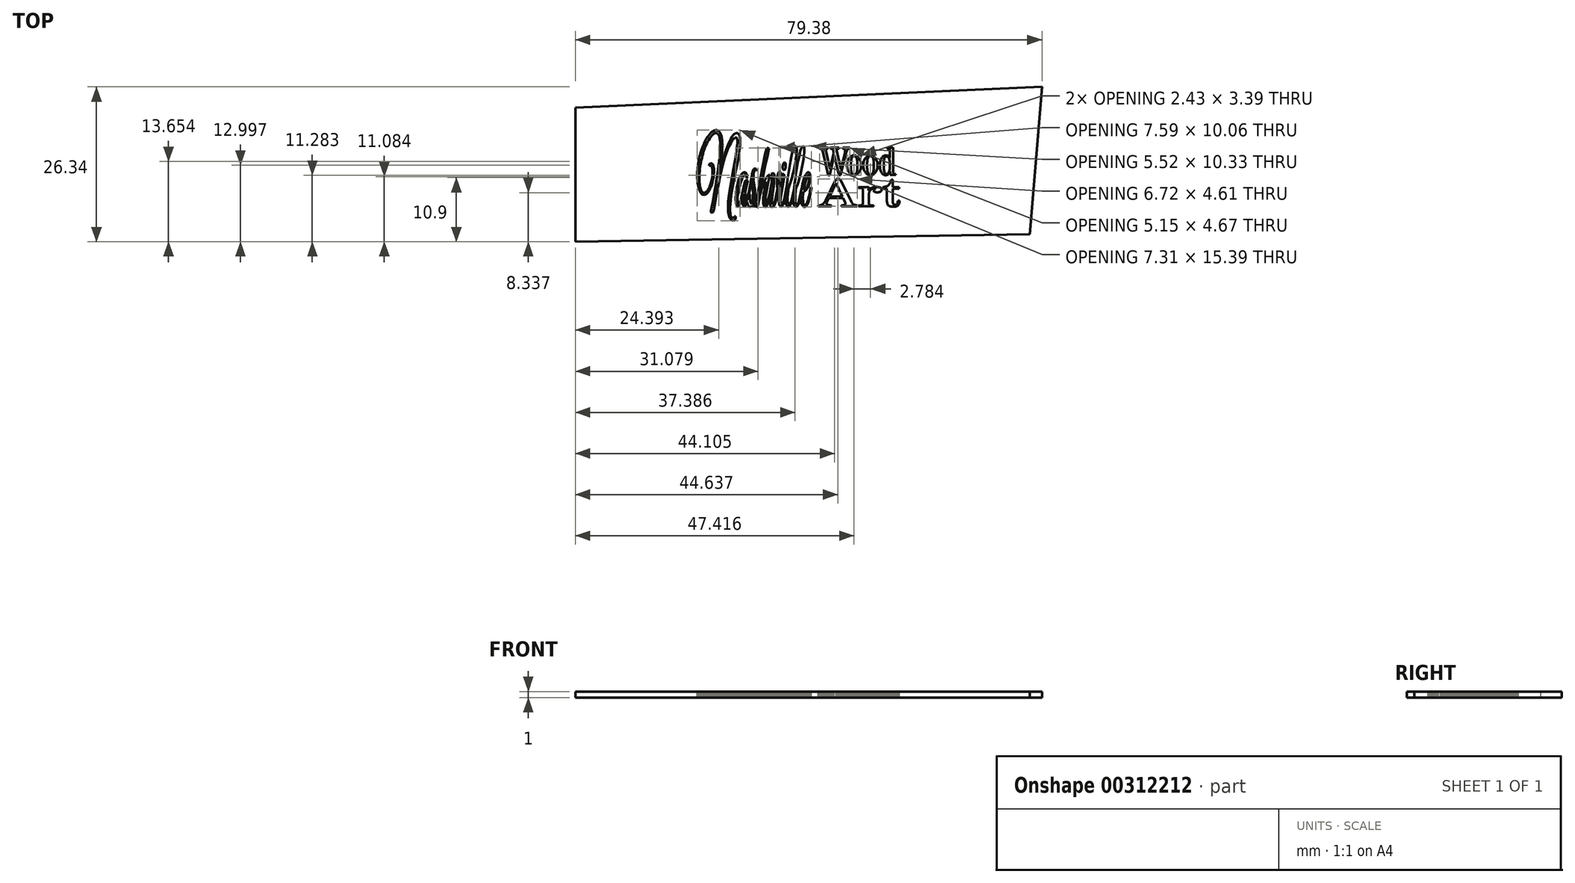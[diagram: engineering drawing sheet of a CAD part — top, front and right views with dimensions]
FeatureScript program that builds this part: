
annotation { "Feature Type Name" : "Feature", "Feature Type Description" : "" }
export const myFeature = defineFeature(function(context is Context, id is Id, definition is map)
    precondition{}
    {
        {
            var Q0;
            Q0=qCreatedBy(makeId("Top.planeOp"),FACE);
            var sketch = newSketch(context, id + "F0", { "sketchPlane" : qUnion([Q0])});
            skLineSegment(sketch, "E0", {"start": v(-39.28, -11.2) * mm, "end": v(-39.32, -11.42) * mm});
            skLineSegment(sketch, "E1", {"start": v(-39.32, -11.42) * mm, "end": v(-39.34, -11.62) * mm});
            skLineSegment(sketch, "E2", {"start": v(-39.34, -11.62) * mm, "end": v(-39.35, -11.79) * mm});
            skLineSegment(sketch, "E3", {"start": v(-39.35, -11.79) * mm, "end": v(-39.35, -11.92) * mm});
            skLineSegment(sketch, "E4", {"start": v(-39.35, -11.92) * mm, "end": v(-39.33, -12.03) * mm});
            skLineSegment(sketch, "E5", {"start": v(-39.33, -12.03) * mm, "end": v(-39.3, -12.1) * mm});
            skLineSegment(sketch, "E6", {"start": v(-39.3, -12.1) * mm, "end": v(-39.28, -12.11) * mm});
            skLineSegment(sketch, "E7", {"start": v(-39.28, -12.11) * mm, "end": v(-39.26, -12.12) * mm});
            skLineSegment(sketch, "E8", {"start": v(-39.26, -12.12) * mm, "end": v(-39.23, -12.12) * mm});
            skLineSegment(sketch, "E9", {"start": v(-39.23, -12.12) * mm, "end": v(-39.2, -12.1) * mm});
            skLineSegment(sketch, "E10", {"start": v(-39.2, -12.1) * mm, "end": v(-38.9, -11.92) * mm});
            skLineSegment(sketch, "E11", {"start": v(-38.9, -11.92) * mm, "end": v(4.95, -11.48) * mm});
            skLineSegment(sketch, "E12", {"start": v(4.95, -11.48) * mm, "end": v(7.55, -11.36) * mm});
            skLineSegment(sketch, "E13", {"start": v(7.55, -11.36) * mm, "end": v(8.8, -11.31) * mm});
            skLineSegment(sketch, "E14", {"start": v(8.8, -11.31) * mm, "end": v(10.27, -11.27) * mm});
            skLineSegment(sketch, "E15", {"start": v(10.27, -11.27) * mm, "end": v(11.78, -11.24) * mm});
            skLineSegment(sketch, "E16", {"start": v(11.78, -11.24) * mm, "end": v(13.15, -11.22) * mm});
            skLineSegment(sketch, "E17", {"start": v(13.15, -11.22) * mm, "end": v(14.14, -11.22) * mm});
            skLineSegment(sketch, "E18", {"start": v(14.14, -11.22) * mm, "end": v(14.54, -11.2) * mm});
            skLineSegment(sketch, "E19", {"start": v(14.54, -11.2) * mm, "end": v(14.89, -11.2) * mm});
            skLineSegment(sketch, "E20", {"start": v(14.89, -11.2) * mm, "end": v(15.18, -11.17) * mm});
            skLineSegment(sketch, "E21", {"start": v(15.18, -11.17) * mm, "end": v(15.42, -11.14) * mm});
            skLineSegment(sketch, "E22", {"start": v(15.42, -11.14) * mm, "end": v(15.62, -11.1) * mm});
            skLineSegment(sketch, "E23", {"start": v(15.62, -11.1) * mm, "end": v(15.78, -11.04) * mm});
            skLineSegment(sketch, "E24", {"start": v(15.78, -11.04) * mm, "end": v(15.85, -11) * mm});
            skLineSegment(sketch, "E25", {"start": v(15.85, -11) * mm, "end": v(15.9, -10.96) * mm});
            skLineSegment(sketch, "E26", {"start": v(15.9, -10.96) * mm, "end": v(15.95, -10.92) * mm});
            skLineSegment(sketch, "E27", {"start": v(15.95, -10.92) * mm, "end": v(16, -10.87) * mm});
            skLineSegment(sketch, "E28", {"start": v(16, -10.87) * mm, "end": v(16.03, -10.82) * mm});
            skLineSegment(sketch, "E29", {"start": v(16.03, -10.82) * mm, "end": v(16.06, -10.76) * mm});
            skLineSegment(sketch, "E30", {"start": v(16.06, -10.76) * mm, "end": v(16.1, -10.62) * mm});
            skLineSegment(sketch, "E31", {"start": v(16.1, -10.62) * mm, "end": v(16.14, -10.46) * mm});
            skLineSegment(sketch, "E32", {"start": v(16.14, -10.46) * mm, "end": v(16.15, -10.28) * mm});
            skLineSegment(sketch, "E33", {"start": v(16.15, -10.28) * mm, "end": v(16.16, -9.82) * mm});
            skLineSegment(sketch, "E34", {"start": v(16.16, -9.82) * mm, "end": v(16.16, -9.4) * mm});
            skLineSegment(sketch, "E35", {"start": v(16.16, -9.4) * mm, "end": v(16.2, -9.08) * mm});
            skLineSegment(sketch, "E36", {"start": v(16.2, -9.08) * mm, "end": v(16.21, -8.93) * mm});
            skLineSegment(sketch, "E37", {"start": v(16.21, -8.93) * mm, "end": v(16.24, -8.8) * mm});
            skLineSegment(sketch, "E38", {"start": v(16.24, -8.8) * mm, "end": v(16.28, -8.68) * mm});
            skLineSegment(sketch, "E39", {"start": v(16.28, -8.68) * mm, "end": v(16.33, -8.57) * mm});
            skLineSegment(sketch, "E40", {"start": v(16.33, -8.57) * mm, "end": v(16.38, -8.47) * mm});
            skLineSegment(sketch, "E41", {"start": v(16.38, -8.47) * mm, "end": v(16.45, -8.38) * mm});
            skLineSegment(sketch, "E42", {"start": v(16.45, -8.38) * mm, "end": v(16.52, -8.29) * mm});
            skLineSegment(sketch, "E43", {"start": v(16.52, -8.29) * mm, "end": v(16.61, -8.2) * mm});
            skLineSegment(sketch, "E44", {"start": v(16.61, -8.2) * mm, "end": v(16.72, -8.12) * mm});
            skLineSegment(sketch, "E45", {"start": v(16.72, -8.12) * mm, "end": v(16.83, -8.04) * mm});
            skLineSegment(sketch, "E46", {"start": v(16.83, -8.04) * mm, "end": v(17.1, -7.86) * mm});
            skLineSegment(sketch, "E47", {"start": v(17.1, -7.86) * mm, "end": v(17.31, -7.73) * mm});
            skLineSegment(sketch, "E48", {"start": v(17.31, -7.73) * mm, "end": v(17.5, -7.57) * mm});
            skLineSegment(sketch, "E49", {"start": v(17.5, -7.57) * mm, "end": v(17.69, -7.39) * mm});
            skLineSegment(sketch, "E50", {"start": v(17.69, -7.39) * mm, "end": v(17.85, -7.2) * mm});
            skLineSegment(sketch, "E51", {"start": v(17.85, -7.2) * mm, "end": v(18, -7) * mm});
            skLineSegment(sketch, "E52", {"start": v(18, -7) * mm, "end": v(18.1, -6.78) * mm});
            skLineSegment(sketch, "E53", {"start": v(18.1, -6.78) * mm, "end": v(18.2, -6.57) * mm});
            skLineSegment(sketch, "E54", {"start": v(18.2, -6.57) * mm, "end": v(18.26, -6.35) * mm});
            skLineSegment(sketch, "E55", {"start": v(18.26, -6.35) * mm, "end": v(18.32, -6.13) * mm});
            skLineSegment(sketch, "E56", {"start": v(18.32, -6.13) * mm, "end": v(18.37, -5.93) * mm});
            skLineSegment(sketch, "E57", {"start": v(18.37, -5.93) * mm, "end": v(18.44, -5.74) * mm});
            skLineSegment(sketch, "E58", {"start": v(18.44, -5.74) * mm, "end": v(18.52, -5.58) * mm});
            skLineSegment(sketch, "E59", {"start": v(18.52, -5.58) * mm, "end": v(18.6, -5.43) * mm});
            skLineSegment(sketch, "E60", {"start": v(18.6, -5.43) * mm, "end": v(18.7, -5.3) * mm});
            skLineSegment(sketch, "E61", {"start": v(18.7, -5.3) * mm, "end": v(18.83, -5.18) * mm});
            skLineSegment(sketch, "E62", {"start": v(18.83, -5.18) * mm, "end": v(18.97, -5.07) * mm});
            skLineSegment(sketch, "E63", {"start": v(18.97, -5.07) * mm, "end": v(19.14, -4.97) * mm});
            skLineSegment(sketch, "E64", {"start": v(19.14, -4.97) * mm, "end": v(19.33, -4.88) * mm});
            skLineSegment(sketch, "E65", {"start": v(19.33, -4.88) * mm, "end": v(19.55, -4.8) * mm});
            skLineSegment(sketch, "E66", {"start": v(19.55, -4.8) * mm, "end": v(19.8, -4.71) * mm});
            skLineSegment(sketch, "E67", {"start": v(19.8, -4.71) * mm, "end": v(20.09, -4.63) * mm});
            skLineSegment(sketch, "E68", {"start": v(20.09, -4.63) * mm, "end": v(20.41, -4.55) * mm});
            skLineSegment(sketch, "E69", {"start": v(20.41, -4.55) * mm, "end": v(21.18, -4.38) * mm});
            skLineSegment(sketch, "E70", {"start": v(21.18, -4.38) * mm, "end": v(21.6, -4.29) * mm});
            skLineSegment(sketch, "E71", {"start": v(21.6, -4.29) * mm, "end": v(22.03, -4.17) * mm});
            skLineSegment(sketch, "E72", {"start": v(22.03, -4.17) * mm, "end": v(22.46, -4.03) * mm});
            skLineSegment(sketch, "E73", {"start": v(22.46, -4.03) * mm, "end": v(22.89, -3.88) * mm});
            skLineSegment(sketch, "E74", {"start": v(22.89, -3.88) * mm, "end": v(23.3, -3.71) * mm});
            skLineSegment(sketch, "E75", {"start": v(23.3, -3.71) * mm, "end": v(23.67, -3.54) * mm});
            skLineSegment(sketch, "E76", {"start": v(23.67, -3.54) * mm, "end": v(24, -3.38) * mm});
            skLineSegment(sketch, "E77", {"start": v(24, -3.38) * mm, "end": v(24.26, -3.21) * mm});
            skLineSegment(sketch, "E78", {"start": v(24.26, -3.21) * mm, "end": v(24.5, -3.06) * mm});
            skLineSegment(sketch, "E79", {"start": v(24.5, -3.06) * mm, "end": v(24.74, -2.91) * mm});
            skLineSegment(sketch, "E80", {"start": v(24.74, -2.91) * mm, "end": v(24.98, -2.78) * mm});
            skLineSegment(sketch, "E81", {"start": v(24.98, -2.78) * mm, "end": v(25.2, -2.67) * mm});
            skLineSegment(sketch, "E82", {"start": v(25.2, -2.67) * mm, "end": v(25.4, -2.57) * mm});
            skLineSegment(sketch, "E83", {"start": v(25.4, -2.57) * mm, "end": v(25.58, -2.5) * mm});
            skLineSegment(sketch, "E84", {"start": v(25.58, -2.5) * mm, "end": v(25.73, -2.45) * mm});
            skLineSegment(sketch, "E85", {"start": v(25.73, -2.45) * mm, "end": v(25.84, -2.44) * mm});
            skLineSegment(sketch, "E86", {"start": v(25.84, -2.44) * mm, "end": v(25.9, -2.43) * mm});
            skLineSegment(sketch, "E87", {"start": v(25.9, -2.43) * mm, "end": v(25.96, -2.4) * mm});
            skLineSegment(sketch, "E88", {"start": v(25.96, -2.4) * mm, "end": v(26.13, -2.32) * mm});
            skLineSegment(sketch, "E89", {"start": v(26.13, -2.32) * mm, "end": v(26.33, -2.19) * mm});
            skLineSegment(sketch, "E90", {"start": v(26.33, -2.19) * mm, "end": v(26.57, -2) * mm});
            skLineSegment(sketch, "E91", {"start": v(26.57, -2) * mm, "end": v(26.84, -1.8) * mm});
            skLineSegment(sketch, "E92", {"start": v(26.84, -1.8) * mm, "end": v(27.12, -1.54) * mm});
            skLineSegment(sketch, "E93", {"start": v(27.12, -1.54) * mm, "end": v(27.41, -1.27) * mm});
            skLineSegment(sketch, "E94", {"start": v(27.41, -1.27) * mm, "end": v(27.7, -0.98) * mm});
            skLineSegment(sketch, "E95", {"start": v(27.7, -0.98) * mm, "end": v(28.08, -0.6) * mm});
            skLineSegment(sketch, "E96", {"start": v(28.08, -0.6) * mm, "end": v(28.41, -0.3) * mm});
            skLineSegment(sketch, "E97", {"start": v(28.41, -0.3) * mm, "end": v(28.73, -0.05) * mm});
            skLineSegment(sketch, "E98", {"start": v(28.73, -0.05) * mm, "end": v(28.87, 0.06) * mm});
            skLineSegment(sketch, "E99", {"start": v(28.87, 0.06) * mm, "end": v(29.02, 0.15) * mm});
            skLineSegment(sketch, "E100", {"start": v(29.02, 0.15) * mm, "end": v(29.15, 0.23) * mm});
            skLineSegment(sketch, "E101", {"start": v(29.15, 0.23) * mm, "end": v(29.29, 0.3) * mm});
            skLineSegment(sketch, "E102", {"start": v(29.29, 0.3) * mm, "end": v(29.42, 0.36) * mm});
            skLineSegment(sketch, "E103", {"start": v(29.42, 0.36) * mm, "end": v(29.55, 0.4) * mm});
            skLineSegment(sketch, "E104", {"start": v(29.55, 0.4) * mm, "end": v(29.68, 0.44) * mm});
            skLineSegment(sketch, "E105", {"start": v(29.68, 0.44) * mm, "end": v(29.8, 0.47) * mm});
            skLineSegment(sketch, "E106", {"start": v(29.8, 0.47) * mm, "end": v(29.93, 0.48) * mm});
            skLineSegment(sketch, "E107", {"start": v(29.93, 0.48) * mm, "end": v(30.06, 0.49) * mm});
            skLineSegment(sketch, "E108", {"start": v(30.06, 0.49) * mm, "end": v(30.3, 0.5) * mm});
            skLineSegment(sketch, "E109", {"start": v(30.3, 0.5) * mm, "end": v(30.52, 0.55) * mm});
            skLineSegment(sketch, "E110", {"start": v(30.52, 0.55) * mm, "end": v(30.75, 0.62) * mm});
            skLineSegment(sketch, "E111", {"start": v(30.75, 0.62) * mm, "end": v(30.98, 0.73) * mm});
            skLineSegment(sketch, "E112", {"start": v(30.98, 0.73) * mm, "end": v(31.2, 0.86) * mm});
            skLineSegment(sketch, "E113", {"start": v(31.2, 0.86) * mm, "end": v(31.42, 1.03) * mm});
            skLineSegment(sketch, "E114", {"start": v(31.42, 1.03) * mm, "end": v(31.64, 1.23) * mm});
            skLineSegment(sketch, "E115", {"start": v(31.64, 1.23) * mm, "end": v(31.86, 1.46) * mm});
            skLineSegment(sketch, "E116", {"start": v(31.86, 1.46) * mm, "end": v(32.07, 1.68) * mm});
            skLineSegment(sketch, "E117", {"start": v(32.07, 1.68) * mm, "end": v(32.29, 1.87) * mm});
            skLineSegment(sketch, "E118", {"start": v(32.29, 1.87) * mm, "end": v(32.5, 2.04) * mm});
            skLineSegment(sketch, "E119", {"start": v(32.5, 2.04) * mm, "end": v(32.73, 2.18) * mm});
            skLineSegment(sketch, "E120", {"start": v(32.73, 2.18) * mm, "end": v(32.95, 2.29) * mm});
            skLineSegment(sketch, "E121", {"start": v(32.95, 2.29) * mm, "end": v(33.17, 2.37) * mm});
            skLineSegment(sketch, "E122", {"start": v(33.17, 2.37) * mm, "end": v(33.38, 2.42) * mm});
            skLineSegment(sketch, "E123", {"start": v(33.38, 2.42) * mm, "end": v(33.49, 2.43) * mm});
            skLineSegment(sketch, "E124", {"start": v(33.49, 2.43) * mm, "end": v(33.59, 2.43) * mm});
            skLineSegment(sketch, "E125", {"start": v(33.59, 2.43) * mm, "end": v(33.7, 2.44) * mm});
            skLineSegment(sketch, "E126", {"start": v(33.7, 2.44) * mm, "end": v(33.81, 2.47) * mm});
            skLineSegment(sketch, "E127", {"start": v(33.81, 2.47) * mm, "end": v(33.94, 2.5) * mm});
            skLineSegment(sketch, "E128", {"start": v(33.94, 2.5) * mm, "end": v(34.07, 2.56) * mm});
            skLineSegment(sketch, "E129", {"start": v(34.07, 2.56) * mm, "end": v(34.21, 2.63) * mm});
            skLineSegment(sketch, "E130", {"start": v(34.21, 2.63) * mm, "end": v(34.36, 2.71) * mm});
            skLineSegment(sketch, "E131", {"start": v(34.36, 2.71) * mm, "end": v(34.66, 2.92) * mm});
            skLineSegment(sketch, "E132", {"start": v(34.66, 2.92) * mm, "end": v(34.99, 3.16) * mm});
            skLineSegment(sketch, "E133", {"start": v(34.99, 3.16) * mm, "end": v(35.32, 3.44) * mm});
            skLineSegment(sketch, "E134", {"start": v(35.32, 3.44) * mm, "end": v(35.66, 3.76) * mm});
            skLineSegment(sketch, "E135", {"start": v(35.66, 3.76) * mm, "end": v(36, 4.1) * mm});
            skLineSegment(sketch, "E136", {"start": v(36, 4.1) * mm, "end": v(36.32, 4.45) * mm});
            skLineSegment(sketch, "E137", {"start": v(36.32, 4.45) * mm, "end": v(36.64, 4.83) * mm});
            skLineSegment(sketch, "E138", {"start": v(36.64, 4.83) * mm, "end": v(36.93, 5.2) * mm});
            skLineSegment(sketch, "E139", {"start": v(36.93, 5.2) * mm, "end": v(37.2, 5.58) * mm});
            skLineSegment(sketch, "E140", {"start": v(37.2, 5.58) * mm, "end": v(37.44, 5.96) * mm});
            skLineSegment(sketch, "E141", {"start": v(37.44, 5.96) * mm, "end": v(37.65, 6.32) * mm});
            skLineSegment(sketch, "E142", {"start": v(37.65, 6.32) * mm, "end": v(37.73, 6.5) * mm});
            skLineSegment(sketch, "E143", {"start": v(37.73, 6.5) * mm, "end": v(37.8, 6.66) * mm});
            skLineSegment(sketch, "E144", {"start": v(37.8, 6.66) * mm, "end": v(37.87, 6.83) * mm});
            skLineSegment(sketch, "E145", {"start": v(37.87, 6.83) * mm, "end": v(37.92, 6.98) * mm});
            skLineSegment(sketch, "E146", {"start": v(37.92, 6.98) * mm, "end": v(38.1, 7.66) * mm});
            skLineSegment(sketch, "E147", {"start": v(38.1, 7.66) * mm, "end": v(38.17, 7.94) * mm});
            skLineSegment(sketch, "E148", {"start": v(38.17, 7.94) * mm, "end": v(38.21, 8.19) * mm});
            skLineSegment(sketch, "E149", {"start": v(38.21, 8.19) * mm, "end": v(38.24, 8.4) * mm});
            skLineSegment(sketch, "E150", {"start": v(38.24, 8.4) * mm, "end": v(38.24, 8.58) * mm});
            skLineSegment(sketch, "E151", {"start": v(38.24, 8.58) * mm, "end": v(38.23, 8.74) * mm});
            skLineSegment(sketch, "E152", {"start": v(38.23, 8.74) * mm, "end": v(38.2, 8.87) * mm});
            skLineSegment(sketch, "E153", {"start": v(38.2, 8.87) * mm, "end": v(38.17, 8.93) * mm});
            skLineSegment(sketch, "E154", {"start": v(38.17, 8.93) * mm, "end": v(38.14, 8.98) * mm});
            skLineSegment(sketch, "E155", {"start": v(38.14, 8.98) * mm, "end": v(38.1, 9.03) * mm});
            skLineSegment(sketch, "E156", {"start": v(38.1, 9.03) * mm, "end": v(38.05, 9.07) * mm});
            skLineSegment(sketch, "E157", {"start": v(38.05, 9.07) * mm, "end": v(37.95, 9.13) * mm});
            skLineSegment(sketch, "E158", {"start": v(37.95, 9.13) * mm, "end": v(37.81, 9.18) * mm});
            skLineSegment(sketch, "E159", {"start": v(37.81, 9.18) * mm, "end": v(37.66, 9.22) * mm});
            skLineSegment(sketch, "E160", {"start": v(37.66, 9.22) * mm, "end": v(37.47, 9.24) * mm});
            skLineSegment(sketch, "E161", {"start": v(37.47, 9.24) * mm, "end": v(37.26, 9.25) * mm});
            skLineSegment(sketch, "E162", {"start": v(37.26, 9.25) * mm, "end": v(37.02, 9.26) * mm});
            skLineSegment(sketch, "E163", {"start": v(37.02, 9.26) * mm, "end": v(36.76, 9.25) * mm});
            skLineSegment(sketch, "E164", {"start": v(36.76, 9.25) * mm, "end": v(36.49, 9.22) * mm});
            skLineSegment(sketch, "E165", {"start": v(36.49, 9.22) * mm, "end": v(36.22, 9.18) * mm});
            skLineSegment(sketch, "E166", {"start": v(36.22, 9.18) * mm, "end": v(35.96, 9.12) * mm});
            skLineSegment(sketch, "E167", {"start": v(35.96, 9.12) * mm, "end": v(35.7, 9.05) * mm});
            skLineSegment(sketch, "E168", {"start": v(35.7, 9.05) * mm, "end": v(35.48, 8.97) * mm});
            skLineSegment(sketch, "E169", {"start": v(35.48, 8.97) * mm, "end": v(35.29, 8.89) * mm});
            skLineSegment(sketch, "E170", {"start": v(35.29, 8.89) * mm, "end": v(35.13, 8.8) * mm});
            skLineSegment(sketch, "E171", {"start": v(35.13, 8.8) * mm, "end": v(34.46, 8.33) * mm});
            skLineSegment(sketch, "E172", {"start": v(34.46, 8.33) * mm, "end": v(14.46, 7.62) * mm});
            skLineSegment(sketch, "E173", {"start": v(14.46, 7.62) * mm, "end": v(-16.17, 7.68) * mm});
            skLineSegment(sketch, "E174", {"start": v(-16.17, 7.68) * mm, "end": v(-17.7, 7.93) * mm});
            skLineSegment(sketch, "E175", {"start": v(-17.7, 7.93) * mm, "end": v(-18.22, 8.01) * mm});
            skLineSegment(sketch, "E176", {"start": v(-18.22, 8.01) * mm, "end": v(-18.6, 8.06) * mm});
            skLineSegment(sketch, "E177", {"start": v(-18.6, 8.06) * mm, "end": v(-18.75, 8.07) * mm});
            skLineSegment(sketch, "E178", {"start": v(-18.75, 8.07) * mm, "end": v(-18.88, 8.06) * mm});
            skLineSegment(sketch, "E179", {"start": v(-18.88, 8.06) * mm, "end": v(-18.98, 8.04) * mm});
            skLineSegment(sketch, "E180", {"start": v(-18.98, 8.04) * mm, "end": v(-19.06, 8.01) * mm});
            skLineSegment(sketch, "E181", {"start": v(-19.06, 8.01) * mm, "end": v(-19.12, 7.97) * mm});
            skLineSegment(sketch, "E182", {"start": v(-19.12, 7.97) * mm, "end": v(-19.17, 7.9) * mm});
            skLineSegment(sketch, "E183", {"start": v(-19.17, 7.9) * mm, "end": v(-19.2, 7.82) * mm});
            skLineSegment(sketch, "E184", {"start": v(-19.2, 7.82) * mm, "end": v(-19.23, 7.72) * mm});
            skLineSegment(sketch, "E185", {"start": v(-19.23, 7.72) * mm, "end": v(-19.24, 7.6) * mm});
            skLineSegment(sketch, "E186", {"start": v(-19.24, 7.6) * mm, "end": v(-19.25, 7.45) * mm});
            skLineSegment(sketch, "E187", {"start": v(-19.25, 7.45) * mm, "end": v(-19.25, 7.1) * mm});
            skLineSegment(sketch, "E188", {"start": v(-19.25, 7.1) * mm, "end": v(-19.26, 6.86) * mm});
            skLineSegment(sketch, "E189", {"start": v(-19.26, 6.86) * mm, "end": v(-19.28, 6.65) * mm});
            skLineSegment(sketch, "E190", {"start": v(-19.28, 6.65) * mm, "end": v(-19.32, 6.47) * mm});
            skLineSegment(sketch, "E191", {"start": v(-19.32, 6.47) * mm, "end": v(-19.36, 6.3) * mm});
            skLineSegment(sketch, "E192", {"start": v(-19.36, 6.3) * mm, "end": v(-19.42, 6.18) * mm});
            skLineSegment(sketch, "E193", {"start": v(-19.42, 6.18) * mm, "end": v(-19.5, 6.08) * mm});
            skLineSegment(sketch, "E194", {"start": v(-19.5, 6.08) * mm, "end": v(-19.53, 6.04) * mm});
            skLineSegment(sketch, "E195", {"start": v(-19.53, 6.04) * mm, "end": v(-19.57, 6.02) * mm});
            skLineSegment(sketch, "E196", {"start": v(-19.57, 6.02) * mm, "end": v(-19.61, 6) * mm});
            skLineSegment(sketch, "E197", {"start": v(-19.61, 6) * mm, "end": v(-19.66, 6) * mm});
            skLineSegment(sketch, "E198", {"start": v(-19.66, 6) * mm, "end": v(-20.06, 5.98) * mm});
            skLineSegment(sketch, "E199", {"start": v(-20.06, 5.98) * mm, "end": v(-23.64, 5.99) * mm});
            skLineSegment(sketch, "E200", {"start": v(-23.64, 5.99) * mm, "end": v(-25.21, 5.98) * mm});
            skLineSegment(sketch, "E201", {"start": v(-25.21, 5.98) * mm, "end": v(-26.86, 5.94) * mm});
            skLineSegment(sketch, "E202", {"start": v(-26.86, 5.94) * mm, "end": v(-28.38, 5.88) * mm});
            skLineSegment(sketch, "E203", {"start": v(-28.38, 5.88) * mm, "end": v(-29.03, 5.84) * mm});
            skLineSegment(sketch, "E204", {"start": v(-29.03, 5.84) * mm, "end": v(-29.58, 5.8) * mm});
            skLineSegment(sketch, "E205", {"start": v(-29.58, 5.8) * mm, "end": v(-30.36, 5.73) * mm});
            skLineSegment(sketch, "E206", {"start": v(-30.36, 5.73) * mm, "end": v(-30.95, 5.67) * mm});
            skLineSegment(sketch, "E207", {"start": v(-30.95, 5.67) * mm, "end": v(-31.2, 5.63) * mm});
            skLineSegment(sketch, "E208", {"start": v(-31.2, 5.63) * mm, "end": v(-31.4, 5.58) * mm});
            skLineSegment(sketch, "E209", {"start": v(-31.4, 5.58) * mm, "end": v(-31.57, 5.53) * mm});
            skLineSegment(sketch, "E210", {"start": v(-31.57, 5.53) * mm, "end": v(-31.72, 5.46) * mm});
            skLineSegment(sketch, "E211", {"start": v(-31.72, 5.46) * mm, "end": v(-31.85, 5.38) * mm});
            skLineSegment(sketch, "E212", {"start": v(-31.85, 5.38) * mm, "end": v(-31.97, 5.28) * mm});
            skLineSegment(sketch, "E213", {"start": v(-31.97, 5.28) * mm, "end": v(-32.07, 5.17) * mm});
            skLineSegment(sketch, "E214", {"start": v(-32.07, 5.17) * mm, "end": v(-32.17, 5.03) * mm});
            skLineSegment(sketch, "E215", {"start": v(-32.17, 5.03) * mm, "end": v(-32.26, 4.88) * mm});
            skLineSegment(sketch, "E216", {"start": v(-32.26, 4.88) * mm, "end": v(-32.35, 4.7) * mm});
            skLineSegment(sketch, "E217", {"start": v(-32.35, 4.7) * mm, "end": v(-32.56, 4.24) * mm});
            skLineSegment(sketch, "E218", {"start": v(-32.56, 4.24) * mm, "end": v(-32.7, 3.93) * mm});
            skLineSegment(sketch, "E219", {"start": v(-32.7, 3.93) * mm, "end": v(-32.82, 3.58) * mm});
            skLineSegment(sketch, "E220", {"start": v(-32.82, 3.58) * mm, "end": v(-32.95, 3.2) * mm});
            skLineSegment(sketch, "E221", {"start": v(-32.95, 3.2) * mm, "end": v(-33.07, 2.79) * mm});
            skLineSegment(sketch, "E222", {"start": v(-33.07, 2.79) * mm, "end": v(-33.17, 2.37) * mm});
            skLineSegment(sketch, "E223", {"start": v(-33.17, 2.37) * mm, "end": v(-33.27, 1.96) * mm});
            skLineSegment(sketch, "E224", {"start": v(-33.27, 1.96) * mm, "end": v(-33.35, 1.57) * mm});
            skLineSegment(sketch, "E225", {"start": v(-33.35, 1.57) * mm, "end": v(-33.4, 1.2) * mm});
            skLineSegment(sketch, "E226", {"start": v(-33.4, 1.2) * mm, "end": v(-33.47, 0.77) * mm});
            skLineSegment(sketch, "E227", {"start": v(-33.47, 0.77) * mm, "end": v(-33.56, 0.37) * mm});
            skLineSegment(sketch, "E228", {"start": v(-33.56, 0.37) * mm, "end": v(-33.66, 0.01) * mm});
            skLineSegment(sketch, "E229", {"start": v(-33.66, 0.01) * mm, "end": v(-33.72, -0.16) * mm});
            skLineSegment(sketch, "E230", {"start": v(-33.72, -0.16) * mm, "end": v(-33.8, -0.32) * mm});
            skLineSegment(sketch, "E231", {"start": v(-33.8, -0.32) * mm, "end": v(-33.86, -0.47) * mm});
            skLineSegment(sketch, "E232", {"start": v(-33.86, -0.47) * mm, "end": v(-33.94, -0.62) * mm});
            skLineSegment(sketch, "E233", {"start": v(-33.94, -0.62) * mm, "end": v(-34.03, -0.77) * mm});
            skLineSegment(sketch, "E234", {"start": v(-34.03, -0.77) * mm, "end": v(-34.12, -0.91) * mm});
            skLineSegment(sketch, "E235", {"start": v(-34.12, -0.91) * mm, "end": v(-34.32, -1.19) * mm});
            skLineSegment(sketch, "E236", {"start": v(-34.32, -1.19) * mm, "end": v(-34.56, -1.46) * mm});
            skLineSegment(sketch, "E237", {"start": v(-34.56, -1.46) * mm, "end": v(-34.75, -1.67) * mm});
            skLineSegment(sketch, "E238", {"start": v(-34.75, -1.67) * mm, "end": v(-34.92, -1.9) * mm});
            skLineSegment(sketch, "E239", {"start": v(-34.92, -1.9) * mm, "end": v(-35.08, -2.13) * mm});
            skLineSegment(sketch, "E240", {"start": v(-35.08, -2.13) * mm, "end": v(-35.22, -2.36) * mm});
            skLineSegment(sketch, "E241", {"start": v(-35.22, -2.36) * mm, "end": v(-35.33, -2.6) * mm});
            skLineSegment(sketch, "E242", {"start": v(-35.33, -2.6) * mm, "end": v(-35.42, -2.8) * mm});
            skLineSegment(sketch, "E243", {"start": v(-35.42, -2.8) * mm, "end": v(-35.48, -3) * mm});
            skLineSegment(sketch, "E244", {"start": v(-35.48, -3) * mm, "end": v(-35.49, -3.1) * mm});
            skLineSegment(sketch, "E245", {"start": v(-35.49, -3.1) * mm, "end": v(-35.5, -3.17) * mm});
            skLineSegment(sketch, "E246", {"start": v(-35.5, -3.17) * mm, "end": v(-35.51, -3.34) * mm});
            skLineSegment(sketch, "E247", {"start": v(-35.51, -3.34) * mm, "end": v(-35.56, -3.55) * mm});
            skLineSegment(sketch, "E248", {"start": v(-35.56, -3.55) * mm, "end": v(-35.63, -3.79) * mm});
            skLineSegment(sketch, "E249", {"start": v(-35.63, -3.79) * mm, "end": v(-35.73, -4.04) * mm});
            skLineSegment(sketch, "E250", {"start": v(-35.73, -4.04) * mm, "end": v(-35.85, -4.3) * mm});
            skLineSegment(sketch, "E251", {"start": v(-35.85, -4.3) * mm, "end": v(-35.98, -4.57) * mm});
            skLineSegment(sketch, "E252", {"start": v(-35.98, -4.57) * mm, "end": v(-36.14, -4.84) * mm});
            skLineSegment(sketch, "E253", {"start": v(-36.14, -4.84) * mm, "end": v(-36.3, -5.1) * mm});
            skLineSegment(sketch, "E254", {"start": v(-36.3, -5.1) * mm, "end": v(-36.47, -5.36) * mm});
            skLineSegment(sketch, "E255", {"start": v(-36.47, -5.36) * mm, "end": v(-36.65, -5.66) * mm});
            skLineSegment(sketch, "E256", {"start": v(-36.65, -5.66) * mm, "end": v(-36.84, -6) * mm});
            skLineSegment(sketch, "E257", {"start": v(-36.84, -6) * mm, "end": v(-37.02, -6.34) * mm});
            skLineSegment(sketch, "E258", {"start": v(-37.02, -6.34) * mm, "end": v(-37.2, -6.7) * mm});
            skLineSegment(sketch, "E259", {"start": v(-37.2, -6.7) * mm, "end": v(-37.37, -7.04) * mm});
            skLineSegment(sketch, "E260", {"start": v(-37.37, -7.04) * mm, "end": v(-37.52, -7.38) * mm});
            skLineSegment(sketch, "E261", {"start": v(-37.52, -7.38) * mm, "end": v(-37.65, -7.68) * mm});
            skLineSegment(sketch, "E262", {"start": v(-37.65, -7.68) * mm, "end": v(-37.76, -7.98) * mm});
            skLineSegment(sketch, "E263", {"start": v(-37.76, -7.98) * mm, "end": v(-37.9, -8.27) * mm});
            skLineSegment(sketch, "E264", {"start": v(-37.9, -8.27) * mm, "end": v(-38.16, -8.83) * mm});
            skLineSegment(sketch, "E265", {"start": v(-38.16, -8.83) * mm, "end": v(-38.3, -9.08) * mm});
            skLineSegment(sketch, "E266", {"start": v(-38.3, -9.08) * mm, "end": v(-38.42, -9.3) * mm});
            skLineSegment(sketch, "E267", {"start": v(-38.42, -9.3) * mm, "end": v(-38.53, -9.47) * mm});
            skLineSegment(sketch, "E268", {"start": v(-38.53, -9.47) * mm, "end": v(-38.63, -9.6) * mm});
            skLineSegment(sketch, "E269", {"start": v(-38.63, -9.6) * mm, "end": v(-38.72, -9.73) * mm});
            skLineSegment(sketch, "E270", {"start": v(-38.72, -9.73) * mm, "end": v(-38.81, -9.89) * mm});
            skLineSegment(sketch, "E271", {"start": v(-38.81, -9.89) * mm, "end": v(-38.9, -10.08) * mm});
            skLineSegment(sketch, "E272", {"start": v(-38.9, -10.08) * mm, "end": v(-39, -10.28) * mm});
            skLineSegment(sketch, "E273", {"start": v(-39, -10.28) * mm, "end": v(-39.08, -10.5) * mm});
            skLineSegment(sketch, "E274", {"start": v(-39.08, -10.5) * mm, "end": v(-39.16, -10.74) * mm});
            skLineSegment(sketch, "E275", {"start": v(-39.16, -10.74) * mm, "end": v(-39.22, -10.97) * mm});
            skLineSegment(sketch, "E276", {"start": v(-39.22, -10.97) * mm, "end": v(-39.28, -11.2) * mm});
            skLineSegment(sketch, "E277", {"start": v(-35.66, -10.48) * mm, "end": v(-8.7, -10.32) * mm});
            skLineSegment(sketch, "E278", {"start": v(-8.7, -10.32) * mm, "end": v(13.4, -9.88) * mm});
            skLineSegment(sketch, "E279", {"start": v(13.4, -9.88) * mm, "end": v(13.98, -9.7) * mm});
            skLineSegment(sketch, "E280", {"start": v(13.98, -9.7) * mm, "end": v(14.04, -9.68) * mm});
            skLineSegment(sketch, "E281", {"start": v(14.04, -9.68) * mm, "end": v(14.1, -9.65) * mm});
            skLineSegment(sketch, "E282", {"start": v(14.1, -9.65) * mm, "end": v(14.22, -9.56) * mm});
            skLineSegment(sketch, "E283", {"start": v(14.22, -9.56) * mm, "end": v(14.33, -9.45) * mm});
            skLineSegment(sketch, "E284", {"start": v(14.33, -9.45) * mm, "end": v(14.44, -9.3) * mm});
            skLineSegment(sketch, "E285", {"start": v(14.44, -9.3) * mm, "end": v(14.54, -9.15) * mm});
            skLineSegment(sketch, "E286", {"start": v(14.54, -9.15) * mm, "end": v(14.63, -8.97) * mm});
            skLineSegment(sketch, "E287", {"start": v(14.63, -8.97) * mm, "end": v(14.7, -8.78) * mm});
            skLineSegment(sketch, "E288", {"start": v(14.7, -8.78) * mm, "end": v(14.75, -8.6) * mm});
            skLineSegment(sketch, "E289", {"start": v(14.75, -8.6) * mm, "end": v(14.77, -8.49) * mm});
            skLineSegment(sketch, "E290", {"start": v(14.77, -8.49) * mm, "end": v(14.8, -8.38) * mm});
            skLineSegment(sketch, "E291", {"start": v(14.8, -8.38) * mm, "end": v(14.9, -8.16) * mm});
            skLineSegment(sketch, "E292", {"start": v(14.9, -8.16) * mm, "end": v(15.03, -7.92) * mm});
            skLineSegment(sketch, "E293", {"start": v(15.03, -7.92) * mm, "end": v(15.2, -7.68) * mm});
            skLineSegment(sketch, "E294", {"start": v(15.2, -7.68) * mm, "end": v(15.38, -7.45) * mm});
            skLineSegment(sketch, "E295", {"start": v(15.38, -7.45) * mm, "end": v(15.58, -7.22) * mm});
            skLineSegment(sketch, "E296", {"start": v(15.58, -7.22) * mm, "end": v(15.8, -7) * mm});
            skLineSegment(sketch, "E297", {"start": v(15.8, -7) * mm, "end": v(16.03, -6.82) * mm});
            skLineSegment(sketch, "E298", {"start": v(16.03, -6.82) * mm, "end": v(16.25, -6.64) * mm});
            skLineSegment(sketch, "E299", {"start": v(16.25, -6.64) * mm, "end": v(16.46, -6.44) * mm});
            skLineSegment(sketch, "E300", {"start": v(16.46, -6.44) * mm, "end": v(16.65, -6.25) * mm});
            skLineSegment(sketch, "E301", {"start": v(16.65, -6.25) * mm, "end": v(16.8, -6.05) * mm});
            skLineSegment(sketch, "E302", {"start": v(16.8, -6.05) * mm, "end": v(16.94, -5.87) * mm});
            skLineSegment(sketch, "E303", {"start": v(16.94, -5.87) * mm, "end": v(17.04, -5.7) * mm});
            skLineSegment(sketch, "E304", {"start": v(17.04, -5.7) * mm, "end": v(17.1, -5.53) * mm});
            skLineSegment(sketch, "E305", {"start": v(17.1, -5.53) * mm, "end": v(17.13, -5.46) * mm});
            skLineSegment(sketch, "E306", {"start": v(17.13, -5.46) * mm, "end": v(17.13, -5.4) * mm});
            skLineSegment(sketch, "E307", {"start": v(17.13, -5.4) * mm, "end": v(17.15, -5.23) * mm});
            skLineSegment(sketch, "E308", {"start": v(17.15, -5.23) * mm, "end": v(17.2, -5.05) * mm});
            skLineSegment(sketch, "E309", {"start": v(17.2, -5.05) * mm, "end": v(17.27, -4.88) * mm});
            skLineSegment(sketch, "E310", {"start": v(17.27, -4.88) * mm, "end": v(17.37, -4.7) * mm});
            skLineSegment(sketch, "E311", {"start": v(17.37, -4.7) * mm, "end": v(17.5, -4.53) * mm});
            skLineSegment(sketch, "E312", {"start": v(17.5, -4.53) * mm, "end": v(17.64, -4.37) * mm});
            skLineSegment(sketch, "E313", {"start": v(17.64, -4.37) * mm, "end": v(17.81, -4.2) * mm});
            skLineSegment(sketch, "E314", {"start": v(17.81, -4.2) * mm, "end": v(18, -4.05) * mm});
            skLineSegment(sketch, "E315", {"start": v(18, -4.05) * mm, "end": v(18.21, -3.9) * mm});
            skLineSegment(sketch, "E316", {"start": v(18.21, -3.9) * mm, "end": v(18.44, -3.77) * mm});
            skLineSegment(sketch, "E317", {"start": v(18.44, -3.77) * mm, "end": v(18.68, -3.64) * mm});
            skLineSegment(sketch, "E318", {"start": v(18.68, -3.64) * mm, "end": v(18.94, -3.53) * mm});
            skLineSegment(sketch, "E319", {"start": v(18.94, -3.53) * mm, "end": v(19.2, -3.43) * mm});
            skLineSegment(sketch, "E320", {"start": v(19.2, -3.43) * mm, "end": v(19.48, -3.34) * mm});
            skLineSegment(sketch, "E321", {"start": v(19.48, -3.34) * mm, "end": v(19.77, -3.27) * mm});
            skLineSegment(sketch, "E322", {"start": v(19.77, -3.27) * mm, "end": v(20.06, -3.21) * mm});
            skLineSegment(sketch, "E323", {"start": v(20.06, -3.21) * mm, "end": v(20.4, -3.14) * mm});
            skLineSegment(sketch, "E324", {"start": v(20.4, -3.14) * mm, "end": v(20.8, -3.03) * mm});
            skLineSegment(sketch, "E325", {"start": v(20.8, -3.03) * mm, "end": v(21.23, -2.89) * mm});
            skLineSegment(sketch, "E326", {"start": v(21.23, -2.89) * mm, "end": v(21.7, -2.71) * mm});
            skLineSegment(sketch, "E327", {"start": v(21.7, -2.71) * mm, "end": v(22.2, -2.5) * mm});
            skLineSegment(sketch, "E328", {"start": v(22.2, -2.5) * mm, "end": v(22.72, -2.28) * mm});
            skLineSegment(sketch, "E329", {"start": v(22.72, -2.28) * mm, "end": v(23.26, -2.03) * mm});
            skLineSegment(sketch, "E330", {"start": v(23.26, -2.03) * mm, "end": v(23.8, -1.77) * mm});
            skLineSegment(sketch, "E331", {"start": v(23.8, -1.77) * mm, "end": v(24.33, -1.5) * mm});
            skLineSegment(sketch, "E332", {"start": v(24.33, -1.5) * mm, "end": v(24.85, -1.22) * mm});
            skLineSegment(sketch, "E333", {"start": v(24.85, -1.22) * mm, "end": v(25.34, -0.94) * mm});
            skLineSegment(sketch, "E334", {"start": v(25.34, -0.94) * mm, "end": v(25.81, -0.66) * mm});
            skLineSegment(sketch, "E335", {"start": v(25.81, -0.66) * mm, "end": v(26.24, -0.39) * mm});
            skLineSegment(sketch, "E336", {"start": v(26.24, -0.39) * mm, "end": v(26.63, -0.12) * mm});
            skLineSegment(sketch, "E337", {"start": v(26.63, -0.12) * mm, "end": v(26.96, 0.13) * mm});
            skLineSegment(sketch, "E338", {"start": v(26.96, 0.13) * mm, "end": v(27.23, 0.36) * mm});
            skLineSegment(sketch, "E339", {"start": v(27.23, 0.36) * mm, "end": v(27.42, 0.53) * mm});
            skLineSegment(sketch, "E340", {"start": v(27.42, 0.53) * mm, "end": v(27.65, 0.7) * mm});
            skLineSegment(sketch, "E341", {"start": v(27.65, 0.7) * mm, "end": v(27.9, 0.86) * mm});
            skLineSegment(sketch, "E342", {"start": v(27.9, 0.86) * mm, "end": v(28.17, 1.02) * mm});
            skLineSegment(sketch, "E343", {"start": v(28.17, 1.02) * mm, "end": v(28.45, 1.17) * mm});
            skLineSegment(sketch, "E344", {"start": v(28.45, 1.17) * mm, "end": v(28.73, 1.3) * mm});
            skLineSegment(sketch, "E345", {"start": v(28.73, 1.3) * mm, "end": v(29, 1.4) * mm});
            skLineSegment(sketch, "E346", {"start": v(29, 1.4) * mm, "end": v(29.25, 1.48) * mm});
            skLineSegment(sketch, "E347", {"start": v(29.25, 1.48) * mm, "end": v(29.5, 1.57) * mm});
            skLineSegment(sketch, "E348", {"start": v(29.5, 1.57) * mm, "end": v(29.78, 1.69) * mm});
            skLineSegment(sketch, "E349", {"start": v(29.78, 1.69) * mm, "end": v(30.07, 1.83) * mm});
            skLineSegment(sketch, "E350", {"start": v(30.07, 1.83) * mm, "end": v(30.36, 2) * mm});
            skLineSegment(sketch, "E351", {"start": v(30.36, 2) * mm, "end": v(30.65, 2.18) * mm});
            skLineSegment(sketch, "E352", {"start": v(30.65, 2.18) * mm, "end": v(30.92, 2.37) * mm});
            skLineSegment(sketch, "E353", {"start": v(30.92, 2.37) * mm, "end": v(31.17, 2.57) * mm});
            skLineSegment(sketch, "E354", {"start": v(31.17, 2.57) * mm, "end": v(31.39, 2.77) * mm});
            skLineSegment(sketch, "E355", {"start": v(31.39, 2.77) * mm, "end": v(31.6, 2.97) * mm});
            skLineSegment(sketch, "E356", {"start": v(31.6, 2.97) * mm, "end": v(31.83, 3.15) * mm});
            skLineSegment(sketch, "E357", {"start": v(31.83, 3.15) * mm, "end": v(32.06, 3.32) * mm});
            skLineSegment(sketch, "E358", {"start": v(32.06, 3.32) * mm, "end": v(32.3, 3.46) * mm});
            skLineSegment(sketch, "E359", {"start": v(32.3, 3.46) * mm, "end": v(32.53, 3.57) * mm});
            skLineSegment(sketch, "E360", {"start": v(32.53, 3.57) * mm, "end": v(32.76, 3.66) * mm});
            skLineSegment(sketch, "E361", {"start": v(32.76, 3.66) * mm, "end": v(32.96, 3.72) * mm});
            skLineSegment(sketch, "E362", {"start": v(32.96, 3.72) * mm, "end": v(33.06, 3.73) * mm});
            skLineSegment(sketch, "E363", {"start": v(33.06, 3.73) * mm, "end": v(33.15, 3.73) * mm});
            skLineSegment(sketch, "E364", {"start": v(33.15, 3.73) * mm, "end": v(33.25, 3.74) * mm});
            skLineSegment(sketch, "E365", {"start": v(33.25, 3.74) * mm, "end": v(33.37, 3.76) * mm});
            skLineSegment(sketch, "E366", {"start": v(33.37, 3.76) * mm, "end": v(33.48, 3.8) * mm});
            skLineSegment(sketch, "E367", {"start": v(33.48, 3.8) * mm, "end": v(33.6, 3.83) * mm});
            skLineSegment(sketch, "E368", {"start": v(33.6, 3.83) * mm, "end": v(33.72, 3.9) * mm});
            skLineSegment(sketch, "E369", {"start": v(33.72, 3.9) * mm, "end": v(33.84, 3.97) * mm});
            skLineSegment(sketch, "E370", {"start": v(33.84, 3.97) * mm, "end": v(33.97, 4.05) * mm});
            skLineSegment(sketch, "E371", {"start": v(33.97, 4.05) * mm, "end": v(34.1, 4.15) * mm});
            skLineSegment(sketch, "E372", {"start": v(34.1, 4.15) * mm, "end": v(34.25, 4.27) * mm});
            skLineSegment(sketch, "E373", {"start": v(34.25, 4.27) * mm, "end": v(34.4, 4.4) * mm});
            skLineSegment(sketch, "E374", {"start": v(34.4, 4.4) * mm, "end": v(34.7, 4.72) * mm});
            skLineSegment(sketch, "E375", {"start": v(34.7, 4.72) * mm, "end": v(35.06, 5.1) * mm});
            skLineSegment(sketch, "E376", {"start": v(35.06, 5.1) * mm, "end": v(35.44, 5.56) * mm});
            skLineSegment(sketch, "E377", {"start": v(35.44, 5.56) * mm, "end": v(35.72, 5.9) * mm});
            skLineSegment(sketch, "E378", {"start": v(35.72, 5.9) * mm, "end": v(35.97, 6.23) * mm});
            skLineSegment(sketch, "E379", {"start": v(35.97, 6.23) * mm, "end": v(36.18, 6.53) * mm});
            skLineSegment(sketch, "E380", {"start": v(36.18, 6.53) * mm, "end": v(36.36, 6.8) * mm});
            skLineSegment(sketch, "E381", {"start": v(36.36, 6.8) * mm, "end": v(36.5, 7.04) * mm});
            skLineSegment(sketch, "E382", {"start": v(36.5, 7.04) * mm, "end": v(36.6, 7.25) * mm});
            skLineSegment(sketch, "E383", {"start": v(36.6, 7.25) * mm, "end": v(36.68, 7.43) * mm});
            skLineSegment(sketch, "E384", {"start": v(36.68, 7.43) * mm, "end": v(36.71, 7.57) * mm});
            skLineSegment(sketch, "E385", {"start": v(36.71, 7.57) * mm, "end": v(36.72, 7.63) * mm});
            skLineSegment(sketch, "E386", {"start": v(36.72, 7.63) * mm, "end": v(36.71, 7.68) * mm});
            skLineSegment(sketch, "E387", {"start": v(36.71, 7.68) * mm, "end": v(36.7, 7.73) * mm});
            skLineSegment(sketch, "E388", {"start": v(36.7, 7.73) * mm, "end": v(36.67, 7.76) * mm});
            skLineSegment(sketch, "E389", {"start": v(36.67, 7.76) * mm, "end": v(36.64, 7.79) * mm});
            skLineSegment(sketch, "E390", {"start": v(36.64, 7.79) * mm, "end": v(36.6, 7.8) * mm});
            skLineSegment(sketch, "E391", {"start": v(36.6, 7.8) * mm, "end": v(36.55, 7.81) * mm});
            skLineSegment(sketch, "E392", {"start": v(36.55, 7.81) * mm, "end": v(36.5, 7.8) * mm});
            skLineSegment(sketch, "E393", {"start": v(36.5, 7.8) * mm, "end": v(36.35, 7.77) * mm});
            skLineSegment(sketch, "E394", {"start": v(36.35, 7.77) * mm, "end": v(36.17, 7.7) * mm});
            skLineSegment(sketch, "E395", {"start": v(36.17, 7.7) * mm, "end": v(35.95, 7.58) * mm});
            skLineSegment(sketch, "E396", {"start": v(35.95, 7.58) * mm, "end": v(35.7, 7.42) * mm});
            skLineSegment(sketch, "E397", {"start": v(35.7, 7.42) * mm, "end": v(34.83, 6.86) * mm});
            skLineSegment(sketch, "E398", {"start": v(34.83, 6.86) * mm, "end": v(23.8, 6.32) * mm});
            skLineSegment(sketch, "E399", {"start": v(23.8, 6.32) * mm, "end": v(-12.6, 6.32) * mm});
            skLineSegment(sketch, "E400", {"start": v(-12.6, 6.32) * mm, "end": v(-14.78, 6.53) * mm});
            skLineSegment(sketch, "E401", {"start": v(-14.78, 6.53) * mm, "end": v(-15.54, 6.6) * mm});
            skLineSegment(sketch, "E402", {"start": v(-15.54, 6.6) * mm, "end": v(-15.85, 6.62) * mm});
            skLineSegment(sketch, "E403", {"start": v(-15.85, 6.62) * mm, "end": v(-16.12, 6.62) * mm});
            skLineSegment(sketch, "E404", {"start": v(-16.12, 6.62) * mm, "end": v(-16.36, 6.62) * mm});
            skLineSegment(sketch, "E405", {"start": v(-16.36, 6.62) * mm, "end": v(-16.56, 6.6) * mm});
            skLineSegment(sketch, "E406", {"start": v(-16.56, 6.6) * mm, "end": v(-16.73, 6.56) * mm});
            skLineSegment(sketch, "E407", {"start": v(-16.73, 6.56) * mm, "end": v(-16.88, 6.5) * mm});
            skLineSegment(sketch, "E408", {"start": v(-16.88, 6.5) * mm, "end": v(-17, 6.43) * mm});
            skLineSegment(sketch, "E409", {"start": v(-17, 6.43) * mm, "end": v(-17.1, 6.33) * mm});
            skLineSegment(sketch, "E410", {"start": v(-17.1, 6.33) * mm, "end": v(-17.18, 6.22) * mm});
            skLineSegment(sketch, "E411", {"start": v(-17.18, 6.22) * mm, "end": v(-17.24, 6.07) * mm});
            skLineSegment(sketch, "E412", {"start": v(-17.24, 6.07) * mm, "end": v(-17.3, 5.9) * mm});
            skLineSegment(sketch, "E413", {"start": v(-17.3, 5.9) * mm, "end": v(-17.35, 5.7) * mm});
            skLineSegment(sketch, "E414", {"start": v(-17.35, 5.7) * mm, "end": v(-17.43, 5.23) * mm});
            skLineSegment(sketch, "E415", {"start": v(-17.43, 5.23) * mm, "end": v(-17.47, 5.02) * mm});
            skLineSegment(sketch, "E416", {"start": v(-17.47, 5.02) * mm, "end": v(-17.53, 4.83) * mm});
            skLineSegment(sketch, "E417", {"start": v(-17.53, 4.83) * mm, "end": v(-17.6, 4.67) * mm});
            skLineSegment(sketch, "E418", {"start": v(-17.6, 4.67) * mm, "end": v(-17.62, 4.61) * mm});
            skLineSegment(sketch, "E419", {"start": v(-17.62, 4.61) * mm, "end": v(-17.66, 4.57) * mm});
            skLineSegment(sketch, "E420", {"start": v(-17.66, 4.57) * mm, "end": v(-17.81, 4.41) * mm});
            skLineSegment(sketch, "E421", {"start": v(-17.81, 4.41) * mm, "end": v(-27.54, 4.29) * mm});
            skLineSegment(sketch, "E422", {"start": v(-27.54, 4.29) * mm, "end": v(-29.16, 4.1) * mm});
            skLineSegment(sketch, "E423", {"start": v(-29.16, 4.1) * mm, "end": v(-29.48, 4.05) * mm});
            skLineSegment(sketch, "E424", {"start": v(-29.48, 4.05) * mm, "end": v(-29.77, 4) * mm});
            skLineSegment(sketch, "E425", {"start": v(-29.77, 4) * mm, "end": v(-30.03, 3.94) * mm});
            skLineSegment(sketch, "E426", {"start": v(-30.03, 3.94) * mm, "end": v(-30.27, 3.87) * mm});
            skLineSegment(sketch, "E427", {"start": v(-30.27, 3.87) * mm, "end": v(-30.48, 3.77) * mm});
            skLineSegment(sketch, "E428", {"start": v(-30.48, 3.77) * mm, "end": v(-30.57, 3.72) * mm});
            skLineSegment(sketch, "E429", {"start": v(-30.57, 3.72) * mm, "end": v(-30.66, 3.66) * mm});
            skLineSegment(sketch, "E430", {"start": v(-30.66, 3.66) * mm, "end": v(-30.75, 3.6) * mm});
            skLineSegment(sketch, "E431", {"start": v(-30.75, 3.6) * mm, "end": v(-30.83, 3.52) * mm});
            skLineSegment(sketch, "E432", {"start": v(-30.83, 3.52) * mm, "end": v(-30.9, 3.43) * mm});
            skLineSegment(sketch, "E433", {"start": v(-30.9, 3.43) * mm, "end": v(-30.98, 3.34) * mm});
            skLineSegment(sketch, "E434", {"start": v(-30.98, 3.34) * mm, "end": v(-31.13, 3.14) * mm});
            skLineSegment(sketch, "E435", {"start": v(-31.13, 3.14) * mm, "end": v(-31.26, 2.89) * mm});
            skLineSegment(sketch, "E436", {"start": v(-31.26, 2.89) * mm, "end": v(-31.39, 2.6) * mm});
            skLineSegment(sketch, "E437", {"start": v(-31.39, 2.6) * mm, "end": v(-31.52, 2.25) * mm});
            skLineSegment(sketch, "E438", {"start": v(-31.52, 2.25) * mm, "end": v(-31.64, 1.86) * mm});
            skLineSegment(sketch, "E439", {"start": v(-31.64, 1.86) * mm, "end": v(-31.78, 1.41) * mm});
            skLineSegment(sketch, "E440", {"start": v(-31.78, 1.41) * mm, "end": v(-32.07, 0.33) * mm});
            skLineSegment(sketch, "E441", {"start": v(-32.07, 0.33) * mm, "end": v(-32.18, -0.07) * mm});
            skLineSegment(sketch, "E442", {"start": v(-32.18, -0.07) * mm, "end": v(-32.31, -0.46) * mm});
            skLineSegment(sketch, "E443", {"start": v(-32.31, -0.46) * mm, "end": v(-32.45, -0.85) * mm});
            skLineSegment(sketch, "E444", {"start": v(-32.45, -0.85) * mm, "end": v(-32.6, -1.22) * mm});
            skLineSegment(sketch, "E445", {"start": v(-32.6, -1.22) * mm, "end": v(-32.75, -1.55) * mm});
            skLineSegment(sketch, "E446", {"start": v(-32.75, -1.55) * mm, "end": v(-32.9, -1.84) * mm});
            skLineSegment(sketch, "E447", {"start": v(-32.9, -1.84) * mm, "end": v(-33.05, -2.08) * mm});
            skLineSegment(sketch, "E448", {"start": v(-33.05, -2.08) * mm, "end": v(-33.12, -2.17) * mm});
            skLineSegment(sketch, "E449", {"start": v(-33.12, -2.17) * mm, "end": v(-33.19, -2.25) * mm});
            skLineSegment(sketch, "E450", {"start": v(-33.19, -2.25) * mm, "end": v(-33.32, -2.41) * mm});
            skLineSegment(sketch, "E451", {"start": v(-33.32, -2.41) * mm, "end": v(-33.45, -2.61) * mm});
            skLineSegment(sketch, "E452", {"start": v(-33.45, -2.61) * mm, "end": v(-33.6, -2.84) * mm});
            skLineSegment(sketch, "E453", {"start": v(-33.6, -2.84) * mm, "end": v(-33.73, -3.1) * mm});
            skLineSegment(sketch, "E454", {"start": v(-33.73, -3.1) * mm, "end": v(-33.85, -3.37) * mm});
            skLineSegment(sketch, "E455", {"start": v(-33.85, -3.37) * mm, "end": v(-33.97, -3.65) * mm});
            skLineSegment(sketch, "E456", {"start": v(-33.97, -3.65) * mm, "end": v(-34.07, -3.92) * mm});
            skLineSegment(sketch, "E457", {"start": v(-34.07, -3.92) * mm, "end": v(-34.15, -4.19) * mm});
            skLineSegment(sketch, "E458", {"start": v(-34.15, -4.19) * mm, "end": v(-34.23, -4.46) * mm});
            skLineSegment(sketch, "E459", {"start": v(-34.23, -4.46) * mm, "end": v(-34.34, -4.74) * mm});
            skLineSegment(sketch, "E460", {"start": v(-34.34, -4.74) * mm, "end": v(-34.46, -5.02) * mm});
            skLineSegment(sketch, "E461", {"start": v(-34.46, -5.02) * mm, "end": v(-34.59, -5.3) * mm});
            skLineSegment(sketch, "E462", {"start": v(-34.59, -5.3) * mm, "end": v(-34.73, -5.55) * mm});
            skLineSegment(sketch, "E463", {"start": v(-34.73, -5.55) * mm, "end": v(-34.87, -5.79) * mm});
            skLineSegment(sketch, "E464", {"start": v(-34.87, -5.79) * mm, "end": v(-35.02, -6) * mm});
            skLineSegment(sketch, "E465", {"start": v(-35.02, -6) * mm, "end": v(-35.16, -6.16) * mm});
            skLineSegment(sketch, "E466", {"start": v(-35.16, -6.16) * mm, "end": v(-35.29, -6.32) * mm});
            skLineSegment(sketch, "E467", {"start": v(-35.29, -6.32) * mm, "end": v(-35.42, -6.53) * mm});
            skLineSegment(sketch, "E468", {"start": v(-35.42, -6.53) * mm, "end": v(-35.56, -6.79) * mm});
            skLineSegment(sketch, "E469", {"start": v(-35.56, -6.79) * mm, "end": v(-35.7, -7.07) * mm});
            skLineSegment(sketch, "E470", {"start": v(-35.7, -7.07) * mm, "end": v(-35.83, -7.39) * mm});
            skLineSegment(sketch, "E471", {"start": v(-35.83, -7.39) * mm, "end": v(-35.97, -7.72) * mm});
            skLineSegment(sketch, "E472", {"start": v(-35.97, -7.72) * mm, "end": v(-36.1, -8.07) * mm});
            skLineSegment(sketch, "E473", {"start": v(-36.1, -8.07) * mm, "end": v(-36.21, -8.42) * mm});
            skLineSegment(sketch, "E474", {"start": v(-36.21, -8.42) * mm, "end": v(-36.32, -8.76) * mm});
            skLineSegment(sketch, "E475", {"start": v(-36.32, -8.76) * mm, "end": v(-36.41, -9.1) * mm});
            skLineSegment(sketch, "E476", {"start": v(-36.41, -9.1) * mm, "end": v(-36.49, -9.4) * mm});
            skLineSegment(sketch, "E477", {"start": v(-36.49, -9.4) * mm, "end": v(-36.54, -9.7) * mm});
            skLineSegment(sketch, "E478", {"start": v(-36.54, -9.7) * mm, "end": v(-36.58, -9.94) * mm});
            skLineSegment(sketch, "E479", {"start": v(-36.58, -9.94) * mm, "end": v(-36.6, -10.14) * mm});
            skLineSegment(sketch, "E480", {"start": v(-36.6, -10.14) * mm, "end": v(-36.59, -10.23) * mm});
            skLineSegment(sketch, "E481", {"start": v(-36.59, -10.23) * mm, "end": v(-36.57, -10.3) * mm});
            skLineSegment(sketch, "E482", {"start": v(-36.57, -10.3) * mm, "end": v(-36.55, -10.35) * mm});
            skLineSegment(sketch, "E483", {"start": v(-36.55, -10.35) * mm, "end": v(-36.53, -10.4) * mm});
            skLineSegment(sketch, "E484", {"start": v(-36.53, -10.4) * mm, "end": v(-36.49, -10.42) * mm});
            skLineSegment(sketch, "E485", {"start": v(-36.49, -10.42) * mm, "end": v(-36.44, -10.45) * mm});
            skLineSegment(sketch, "E486", {"start": v(-36.44, -10.45) * mm, "end": v(-36.3, -10.5) * mm});
            skLineSegment(sketch, "E487", {"start": v(-36.3, -10.5) * mm, "end": v(-36.16, -10.52) * mm});
            skLineSegment(sketch, "E488", {"start": v(-36.16, -10.52) * mm, "end": v(-36, -10.52) * mm});
            skLineSegment(sketch, "E489", {"start": v(-36, -10.52) * mm, "end": v(-35.66, -10.48) * mm});
            skLineSegment(sketch, "E490", {"start": v(-11.64, 3.76) * mm, "end": v(-11.65, 4.17) * mm});
            skLineSegment(sketch, "E491", {"start": v(-11.65, 4.17) * mm, "end": v(-11.67, 4.35) * mm});
            skLineSegment(sketch, "E492", {"start": v(-11.67, 4.35) * mm, "end": v(-11.69, 4.51) * mm});
            skLineSegment(sketch, "E493", {"start": v(-11.69, 4.51) * mm, "end": v(-11.72, 4.66) * mm});
            skLineSegment(sketch, "E494", {"start": v(-11.72, 4.66) * mm, "end": v(-11.75, 4.79) * mm});
            skLineSegment(sketch, "E495", {"start": v(-11.75, 4.79) * mm, "end": v(-11.79, 4.9) * mm});
            skLineSegment(sketch, "E496", {"start": v(-11.79, 4.9) * mm, "end": v(-11.83, 5) * mm});
            skLineSegment(sketch, "E497", {"start": v(-11.83, 5) * mm, "end": v(-11.88, 5.08) * mm});
            skLineSegment(sketch, "E498", {"start": v(-11.88, 5.08) * mm, "end": v(-11.94, 5.15) * mm});
            skLineSegment(sketch, "E499", {"start": v(-11.94, 5.15) * mm, "end": v(-12, 5.21) * mm});
            skLineSegment(sketch, "E500", {"start": v(-12, 5.21) * mm, "end": v(-12.05, 5.26) * mm});
            skLineSegment(sketch, "E501", {"start": v(-12.05, 5.26) * mm, "end": v(-12.11, 5.29) * mm});
            skLineSegment(sketch, "E502", {"start": v(-12.11, 5.29) * mm, "end": v(-12.18, 5.3) * mm});
            skLineSegment(sketch, "E503", {"start": v(-12.18, 5.3) * mm, "end": v(-12.25, 5.3) * mm});
            skLineSegment(sketch, "E504", {"start": v(-12.25, 5.3) * mm, "end": v(-12.32, 5.3) * mm});
            skLineSegment(sketch, "E505", {"start": v(-12.32, 5.3) * mm, "end": v(-12.4, 5.28) * mm});
            skLineSegment(sketch, "E506", {"start": v(-12.4, 5.28) * mm, "end": v(-12.46, 5.25) * mm});
            skLineSegment(sketch, "E507", {"start": v(-12.46, 5.25) * mm, "end": v(-12.54, 5.21) * mm});
            skLineSegment(sketch, "E508", {"start": v(-12.54, 5.21) * mm, "end": v(-12.61, 5.16) * mm});
            skLineSegment(sketch, "E509", {"start": v(-12.61, 5.16) * mm, "end": v(-12.76, 5.04) * mm});
            skLineSegment(sketch, "E510", {"start": v(-12.76, 5.04) * mm, "end": v(-12.9, 4.87) * mm});
            skLineSegment(sketch, "E511", {"start": v(-12.9, 4.87) * mm, "end": v(-13, 4.75) * mm});
            skLineSegment(sketch, "E512", {"start": v(-13, 4.75) * mm, "end": v(-13.09, 4.62) * mm});
            skLineSegment(sketch, "E513", {"start": v(-13.09, 4.62) * mm, "end": v(-13.27, 4.3) * mm});
            skLineSegment(sketch, "E514", {"start": v(-13.27, 4.3) * mm, "end": v(-13.45, 3.94) * mm});
            skLineSegment(sketch, "E515", {"start": v(-13.45, 3.94) * mm, "end": v(-13.64, 3.51) * mm});
            skLineSegment(sketch, "E516", {"start": v(-13.64, 3.51) * mm, "end": v(-13.82, 3.04) * mm});
            skLineSegment(sketch, "E517", {"start": v(-13.82, 3.04) * mm, "end": v(-14, 2.54) * mm});
            skLineSegment(sketch, "E518", {"start": v(-14, 2.54) * mm, "end": v(-14.18, 2.02) * mm});
            skLineSegment(sketch, "E519", {"start": v(-14.18, 2.02) * mm, "end": v(-14.36, 1.46) * mm});
            skLineSegment(sketch, "E520", {"start": v(-14.36, 1.46) * mm, "end": v(-14.59, 0.72) * mm});
            skLineSegment(sketch, "E521", {"start": v(-14.59, 0.72) * mm, "end": v(-14.8, -0.04) * mm});
            skLineSegment(sketch, "E522", {"start": v(-14.8, -0.04) * mm, "end": v(-15, -0.78) * mm});
            skLineSegment(sketch, "E523", {"start": v(-15, -0.78) * mm, "end": v(-15.17, -1.49) * mm});
            skLineSegment(sketch, "E524", {"start": v(-15.17, -1.49) * mm, "end": v(-15.3, -2.06) * mm});
            skLineSegment(sketch, "E525", {"start": v(-15.3, -2.06) * mm, "end": v(-15.35, -2.27) * mm});
            skLineSegment(sketch, "E526", {"start": v(-15.35, -2.27) * mm, "end": v(-15.36, -2.3) * mm});
            skLineSegment(sketch, "E527", {"start": v(-15.36, -2.3) * mm, "end": v(-15.36, -2.28) * mm});
            skLineSegment(sketch, "E528", {"start": v(-15.36, -2.28) * mm, "end": v(-15.2, -1.3) * mm});
            skLineSegment(sketch, "E529", {"start": v(-15.2, -1.3) * mm, "end": v(-15.04, -0.37) * mm});
            skLineSegment(sketch, "E530", {"start": v(-15.04, -0.37) * mm, "end": v(-14.89, 0.6) * mm});
            skLineSegment(sketch, "E531", {"start": v(-14.89, 0.6) * mm, "end": v(-14.82, 1.08) * mm});
            skLineSegment(sketch, "E532", {"start": v(-14.82, 1.08) * mm, "end": v(-14.77, 1.56) * mm});
            skLineSegment(sketch, "E533", {"start": v(-14.77, 1.56) * mm, "end": v(-14.72, 2.04) * mm});
            skLineSegment(sketch, "E534", {"start": v(-14.72, 2.04) * mm, "end": v(-14.7, 2.51) * mm});
            skLineSegment(sketch, "E535", {"start": v(-14.7, 2.51) * mm, "end": v(-14.68, 2.88) * mm});
            skLineSegment(sketch, "E536", {"start": v(-14.68, 2.88) * mm, "end": v(-14.68, 3.22) * mm});
            skLineSegment(sketch, "E537", {"start": v(-14.68, 3.22) * mm, "end": v(-14.69, 3.53) * mm});
            skLineSegment(sketch, "E538", {"start": v(-14.69, 3.53) * mm, "end": v(-14.7, 3.83) * mm});
            skLineSegment(sketch, "E539", {"start": v(-14.7, 3.83) * mm, "end": v(-14.72, 4.1) * mm});
            skLineSegment(sketch, "E540", {"start": v(-14.72, 4.1) * mm, "end": v(-14.76, 4.35) * mm});
            skLineSegment(sketch, "E541", {"start": v(-14.76, 4.35) * mm, "end": v(-14.8, 4.58) * mm});
            skLineSegment(sketch, "E542", {"start": v(-14.8, 4.58) * mm, "end": v(-14.85, 4.78) * mm});
            skLineSegment(sketch, "E543", {"start": v(-14.85, 4.78) * mm, "end": v(-14.9, 4.96) * mm});
            skLineSegment(sketch, "E544", {"start": v(-14.9, 4.96) * mm, "end": v(-14.96, 5.13) * mm});
            skLineSegment(sketch, "E545", {"start": v(-14.96, 5.13) * mm, "end": v(-15.03, 5.28) * mm});
            skLineSegment(sketch, "E546", {"start": v(-15.03, 5.28) * mm, "end": v(-15.1, 5.4) * mm});
            skLineSegment(sketch, "E547", {"start": v(-15.1, 5.4) * mm, "end": v(-15.18, 5.51) * mm});
            skLineSegment(sketch, "E548", {"start": v(-15.18, 5.51) * mm, "end": v(-15.26, 5.6) * mm});
            skLineSegment(sketch, "E549", {"start": v(-15.26, 5.6) * mm, "end": v(-15.35, 5.68) * mm});
            skLineSegment(sketch, "E550", {"start": v(-15.35, 5.68) * mm, "end": v(-15.44, 5.73) * mm});
            skLineSegment(sketch, "E551", {"start": v(-15.44, 5.73) * mm, "end": v(-15.54, 5.77) * mm});
            skLineSegment(sketch, "E552", {"start": v(-15.54, 5.77) * mm, "end": v(-15.63, 5.8) * mm});
            skLineSegment(sketch, "E553", {"start": v(-15.63, 5.8) * mm, "end": v(-15.73, 5.8) * mm});
            skLineSegment(sketch, "E554", {"start": v(-15.73, 5.8) * mm, "end": v(-15.84, 5.8) * mm});
            skLineSegment(sketch, "E555", {"start": v(-15.84, 5.8) * mm, "end": v(-15.94, 5.79) * mm});
            skLineSegment(sketch, "E556", {"start": v(-15.94, 5.79) * mm, "end": v(-16.04, 5.75) * mm});
            skLineSegment(sketch, "E557", {"start": v(-16.04, 5.75) * mm, "end": v(-16.15, 5.7) * mm});
            skLineSegment(sketch, "E558", {"start": v(-16.15, 5.7) * mm, "end": v(-16.26, 5.65) * mm});
            skLineSegment(sketch, "E559", {"start": v(-16.26, 5.65) * mm, "end": v(-16.37, 5.58) * mm});
            skLineSegment(sketch, "E560", {"start": v(-16.37, 5.58) * mm, "end": v(-16.48, 5.5) * mm});
            skLineSegment(sketch, "E561", {"start": v(-16.48, 5.5) * mm, "end": v(-16.58, 5.41) * mm});
            skLineSegment(sketch, "E562", {"start": v(-16.58, 5.41) * mm, "end": v(-16.69, 5.31) * mm});
            skLineSegment(sketch, "E563", {"start": v(-16.69, 5.31) * mm, "end": v(-16.89, 5.09) * mm});
            skLineSegment(sketch, "E564", {"start": v(-16.89, 5.09) * mm, "end": v(-17.09, 4.82) * mm});
            skLineSegment(sketch, "E565", {"start": v(-17.09, 4.82) * mm, "end": v(-17.22, 4.62) * mm});
            skLineSegment(sketch, "E566", {"start": v(-17.22, 4.62) * mm, "end": v(-17.35, 4.4) * mm});
            skLineSegment(sketch, "E567", {"start": v(-17.35, 4.4) * mm, "end": v(-17.48, 4.18) * mm});
            skLineSegment(sketch, "E568", {"start": v(-17.48, 4.18) * mm, "end": v(-17.6, 3.94) * mm});
            skLineSegment(sketch, "E569", {"start": v(-17.6, 3.94) * mm, "end": v(-17.73, 3.69) * mm});
            skLineSegment(sketch, "E570", {"start": v(-17.73, 3.69) * mm, "end": v(-17.85, 3.42) * mm});
            skLineSegment(sketch, "E571", {"start": v(-17.85, 3.42) * mm, "end": v(-18.08, 2.86) * mm});
            skLineSegment(sketch, "E572", {"start": v(-18.08, 2.86) * mm, "end": v(-18.2, 2.56) * mm});
            skLineSegment(sketch, "E573", {"start": v(-18.2, 2.56) * mm, "end": v(-18.3, 2.25) * mm});
            skLineSegment(sketch, "E574", {"start": v(-18.3, 2.25) * mm, "end": v(-18.4, 1.94) * mm});
            skLineSegment(sketch, "E575", {"start": v(-18.4, 1.94) * mm, "end": v(-18.48, 1.62) * mm});
            skLineSegment(sketch, "E576", {"start": v(-18.48, 1.62) * mm, "end": v(-18.56, 1.29) * mm});
            skLineSegment(sketch, "E577", {"start": v(-18.56, 1.29) * mm, "end": v(-18.64, 0.95) * mm});
            skLineSegment(sketch, "E578", {"start": v(-18.64, 0.95) * mm, "end": v(-18.7, 0.6) * mm});
            skLineSegment(sketch, "E579", {"start": v(-18.7, 0.6) * mm, "end": v(-18.77, 0.25) * mm});
            skLineSegment(sketch, "E580", {"start": v(-18.77, 0.25) * mm, "end": v(-18.83, -0.16) * mm});
            skLineSegment(sketch, "E581", {"start": v(-18.83, -0.16) * mm, "end": v(-18.87, -0.56) * mm});
            skLineSegment(sketch, "E582", {"start": v(-18.87, -0.56) * mm, "end": v(-18.9, -0.94) * mm});
            skLineSegment(sketch, "E583", {"start": v(-18.9, -0.94) * mm, "end": v(-18.93, -1.31) * mm});
            skLineSegment(sketch, "E584", {"start": v(-18.93, -1.31) * mm, "end": v(-18.95, -1.67) * mm});
            skLineSegment(sketch, "E585", {"start": v(-18.95, -1.67) * mm, "end": v(-18.95, -2) * mm});
            skLineSegment(sketch, "E586", {"start": v(-18.95, -2) * mm, "end": v(-18.95, -2.33) * mm});
            skLineSegment(sketch, "E587", {"start": v(-18.95, -2.33) * mm, "end": v(-18.93, -2.64) * mm});
            skLineSegment(sketch, "E588", {"start": v(-18.93, -2.64) * mm, "end": v(-18.9, -2.94) * mm});
            skLineSegment(sketch, "E589", {"start": v(-18.9, -2.94) * mm, "end": v(-18.88, -3.22) * mm});
            skLineSegment(sketch, "E590", {"start": v(-18.88, -3.22) * mm, "end": v(-18.84, -3.48) * mm});
            skLineSegment(sketch, "E591", {"start": v(-18.84, -3.48) * mm, "end": v(-18.8, -3.72) * mm});
            skLineSegment(sketch, "E592", {"start": v(-18.8, -3.72) * mm, "end": v(-18.74, -3.95) * mm});
            skLineSegment(sketch, "E593", {"start": v(-18.74, -3.95) * mm, "end": v(-18.68, -4.16) * mm});
            skLineSegment(sketch, "E594", {"start": v(-18.68, -4.16) * mm, "end": v(-18.62, -4.35) * mm});
            skLineSegment(sketch, "E595", {"start": v(-18.62, -4.35) * mm, "end": v(-18.54, -4.52) * mm});
            skLineSegment(sketch, "E596", {"start": v(-18.54, -4.52) * mm, "end": v(-18.47, -4.68) * mm});
            skLineSegment(sketch, "E597", {"start": v(-18.47, -4.68) * mm, "end": v(-18.39, -4.8) * mm});
            skLineSegment(sketch, "E598", {"start": v(-18.39, -4.8) * mm, "end": v(-18.3, -4.92) * mm});
            skLineSegment(sketch, "E599", {"start": v(-18.3, -4.92) * mm, "end": v(-18.22, -5.02) * mm});
            skLineSegment(sketch, "E600", {"start": v(-18.22, -5.02) * mm, "end": v(-18.13, -5.1) * mm});
            skLineSegment(sketch, "E601", {"start": v(-18.13, -5.1) * mm, "end": v(-18.04, -5.14) * mm});
            skLineSegment(sketch, "E602", {"start": v(-18.04, -5.14) * mm, "end": v(-17.94, -5.18) * mm});
            skLineSegment(sketch, "E603", {"start": v(-17.94, -5.18) * mm, "end": v(-17.84, -5.19) * mm});
            skLineSegment(sketch, "E604", {"start": v(-17.84, -5.19) * mm, "end": v(-17.72, -5.17) * mm});
            skLineSegment(sketch, "E605", {"start": v(-17.72, -5.17) * mm, "end": v(-17.6, -5.14) * mm});
            skLineSegment(sketch, "E606", {"start": v(-17.6, -5.14) * mm, "end": v(-17.5, -5.09) * mm});
            skLineSegment(sketch, "E607", {"start": v(-17.5, -5.09) * mm, "end": v(-17.38, -5.02) * mm});
            skLineSegment(sketch, "E608", {"start": v(-17.38, -5.02) * mm, "end": v(-17.27, -4.93) * mm});
            skLineSegment(sketch, "E609", {"start": v(-17.27, -4.93) * mm, "end": v(-17.17, -4.82) * mm});
            skLineSegment(sketch, "E610", {"start": v(-17.17, -4.82) * mm, "end": v(-17.07, -4.7) * mm});
            skLineSegment(sketch, "E611", {"start": v(-17.07, -4.7) * mm, "end": v(-16.98, -4.55) * mm});
            skLineSegment(sketch, "E612", {"start": v(-16.98, -4.55) * mm, "end": v(-16.89, -4.4) * mm});
            skLineSegment(sketch, "E613", {"start": v(-16.89, -4.4) * mm, "end": v(-16.8, -4.23) * mm});
            skLineSegment(sketch, "E614", {"start": v(-16.8, -4.23) * mm, "end": v(-16.72, -4.06) * mm});
            skLineSegment(sketch, "E615", {"start": v(-16.72, -4.06) * mm, "end": v(-16.64, -3.88) * mm});
            skLineSegment(sketch, "E616", {"start": v(-16.64, -3.88) * mm, "end": v(-16.5, -3.5) * mm});
            skLineSegment(sketch, "E617", {"start": v(-16.5, -3.5) * mm, "end": v(-16.38, -3.07) * mm});
            skLineSegment(sketch, "E618", {"start": v(-16.38, -3.07) * mm, "end": v(-16.28, -2.64) * mm});
            skLineSegment(sketch, "E619", {"start": v(-16.28, -2.64) * mm, "end": v(-16.2, -2.22) * mm});
            skLineSegment(sketch, "E620", {"start": v(-16.2, -2.22) * mm, "end": v(-16.15, -1.8) * mm});
            skLineSegment(sketch, "E621", {"start": v(-16.15, -1.8) * mm, "end": v(-16.12, -1.39) * mm});
            skLineSegment(sketch, "E622", {"start": v(-16.12, -1.39) * mm, "end": v(-16.11, -1) * mm});
            skLineSegment(sketch, "E623", {"start": v(-16.11, -1) * mm, "end": v(-16.13, -0.67) * mm});
            skLineSegment(sketch, "E624", {"start": v(-16.13, -0.67) * mm, "end": v(-16.15, -0.51) * mm});
            skLineSegment(sketch, "E625", {"start": v(-16.15, -0.51) * mm, "end": v(-16.18, -0.38) * mm});
            skLineSegment(sketch, "E626", {"start": v(-16.18, -0.38) * mm, "end": v(-16.22, -0.25) * mm});
            skLineSegment(sketch, "E627", {"start": v(-16.22, -0.25) * mm, "end": v(-16.26, -0.13) * mm});
            skLineSegment(sketch, "E628", {"start": v(-16.26, -0.13) * mm, "end": v(-16.3, -0.03) * mm});
            skLineSegment(sketch, "E629", {"start": v(-16.3, -0.03) * mm, "end": v(-16.36, 0.04) * mm});
            skLineSegment(sketch, "E630", {"start": v(-16.36, 0.04) * mm, "end": v(-16.43, 0.1) * mm});
            skLineSegment(sketch, "E631", {"start": v(-16.43, 0.1) * mm, "end": v(-16.5, 0.13) * mm});
            skLineSegment(sketch, "E632", {"start": v(-16.5, 0.13) * mm, "end": v(-16.58, 0.15) * mm});
            skLineSegment(sketch, "E633", {"start": v(-16.58, 0.15) * mm, "end": v(-16.67, 0.14) * mm});
            skLineSegment(sketch, "E634", {"start": v(-16.67, 0.14) * mm, "end": v(-16.77, 0.1) * mm});
            skLineSegment(sketch, "E635", {"start": v(-16.77, 0.1) * mm, "end": v(-16.87, 0.05) * mm});
            skLineSegment(sketch, "E636", {"start": v(-16.87, 0.05) * mm, "end": v(-16.9, 0.03) * mm});
            skLineSegment(sketch, "E637", {"start": v(-16.9, 0.03) * mm, "end": v(-16.91, 0) * mm});
            skLineSegment(sketch, "E638", {"start": v(-16.91, 0) * mm, "end": v(-16.94, -0.1) * mm});
            skLineSegment(sketch, "E639", {"start": v(-16.94, -0.1) * mm, "end": v(-16.94, -0.15) * mm});
            skLineSegment(sketch, "E640", {"start": v(-16.94, -0.15) * mm, "end": v(-16.92, -0.18) * mm});
            skLineSegment(sketch, "E641", {"start": v(-16.92, -0.18) * mm, "end": v(-16.9, -0.2) * mm});
            skLineSegment(sketch, "E642", {"start": v(-16.9, -0.2) * mm, "end": v(-16.86, -0.2) * mm});
            skLineSegment(sketch, "E643", {"start": v(-16.86, -0.2) * mm, "end": v(-16.76, -0.2) * mm});
            skLineSegment(sketch, "E644", {"start": v(-16.76, -0.2) * mm, "end": v(-16.68, -0.2) * mm});
            skLineSegment(sketch, "E645", {"start": v(-16.68, -0.2) * mm, "end": v(-16.6, -0.24) * mm});
            skLineSegment(sketch, "E646", {"start": v(-16.6, -0.24) * mm, "end": v(-16.53, -0.3) * mm});
            skLineSegment(sketch, "E647", {"start": v(-16.53, -0.3) * mm, "end": v(-16.48, -0.38) * mm});
            skLineSegment(sketch, "E648", {"start": v(-16.48, -0.38) * mm, "end": v(-16.43, -0.5) * mm});
            skLineSegment(sketch, "E649", {"start": v(-16.43, -0.5) * mm, "end": v(-16.4, -0.62) * mm});
            skLineSegment(sketch, "E650", {"start": v(-16.4, -0.62) * mm, "end": v(-16.37, -0.78) * mm});
            skLineSegment(sketch, "E651", {"start": v(-16.37, -0.78) * mm, "end": v(-16.35, -0.95) * mm});
            skLineSegment(sketch, "E652", {"start": v(-16.35, -0.95) * mm, "end": v(-16.34, -1.13) * mm});
            skLineSegment(sketch, "E653", {"start": v(-16.34, -1.13) * mm, "end": v(-16.34, -1.32) * mm});
            skLineSegment(sketch, "E654", {"start": v(-16.34, -1.32) * mm, "end": v(-16.34, -1.52) * mm});
            skLineSegment(sketch, "E655", {"start": v(-16.34, -1.52) * mm, "end": v(-16.38, -1.94) * mm});
            skLineSegment(sketch, "E656", {"start": v(-16.38, -1.94) * mm, "end": v(-16.45, -2.4) * mm});
            skLineSegment(sketch, "E657", {"start": v(-16.45, -2.4) * mm, "end": v(-16.54, -2.86) * mm});
            skLineSegment(sketch, "E658", {"start": v(-16.54, -2.86) * mm, "end": v(-16.66, -3.3) * mm});
            skLineSegment(sketch, "E659", {"start": v(-16.66, -3.3) * mm, "end": v(-16.73, -3.5) * mm});
            skLineSegment(sketch, "E660", {"start": v(-16.73, -3.5) * mm, "end": v(-16.8, -3.71) * mm});
            skLineSegment(sketch, "E661", {"start": v(-16.8, -3.71) * mm, "end": v(-16.89, -3.9) * mm});
            skLineSegment(sketch, "E662", {"start": v(-16.89, -3.9) * mm, "end": v(-16.98, -4.1) * mm});
            skLineSegment(sketch, "E663", {"start": v(-16.98, -4.1) * mm, "end": v(-17.07, -4.27) * mm});
            skLineSegment(sketch, "E664", {"start": v(-17.07, -4.27) * mm, "end": v(-17.16, -4.42) * mm});
            skLineSegment(sketch, "E665", {"start": v(-17.16, -4.42) * mm, "end": v(-17.26, -4.55) * mm});
            skLineSegment(sketch, "E666", {"start": v(-17.26, -4.55) * mm, "end": v(-17.37, -4.66) * mm});
            skLineSegment(sketch, "E667", {"start": v(-17.37, -4.66) * mm, "end": v(-17.48, -4.75) * mm});
            skLineSegment(sketch, "E668", {"start": v(-17.48, -4.75) * mm, "end": v(-17.59, -4.81) * mm});
            skLineSegment(sketch, "E669", {"start": v(-17.59, -4.81) * mm, "end": v(-17.7, -4.86) * mm});
            skLineSegment(sketch, "E670", {"start": v(-17.7, -4.86) * mm, "end": v(-17.82, -4.88) * mm});
            skLineSegment(sketch, "E671", {"start": v(-17.82, -4.88) * mm, "end": v(-17.93, -4.85) * mm});
            skLineSegment(sketch, "E672", {"start": v(-17.93, -4.85) * mm, "end": v(-18.04, -4.8) * mm});
            skLineSegment(sketch, "E673", {"start": v(-18.04, -4.8) * mm, "end": v(-18.13, -4.72) * mm});
            skLineSegment(sketch, "E674", {"start": v(-18.13, -4.72) * mm, "end": v(-18.21, -4.61) * mm});
            skLineSegment(sketch, "E675", {"start": v(-18.21, -4.61) * mm, "end": v(-18.29, -4.48) * mm});
            skLineSegment(sketch, "E676", {"start": v(-18.29, -4.48) * mm, "end": v(-18.36, -4.31) * mm});
            skLineSegment(sketch, "E677", {"start": v(-18.36, -4.31) * mm, "end": v(-18.42, -4.12) * mm});
            skLineSegment(sketch, "E678", {"start": v(-18.42, -4.12) * mm, "end": v(-18.47, -3.9) * mm});
            skLineSegment(sketch, "E679", {"start": v(-18.47, -3.9) * mm, "end": v(-18.5, -3.65) * mm});
            skLineSegment(sketch, "E680", {"start": v(-18.5, -3.65) * mm, "end": v(-18.54, -3.39) * mm});
            skLineSegment(sketch, "E681", {"start": v(-18.54, -3.39) * mm, "end": v(-18.57, -3.11) * mm});
            skLineSegment(sketch, "E682", {"start": v(-18.57, -3.11) * mm, "end": v(-18.58, -2.82) * mm});
            skLineSegment(sketch, "E683", {"start": v(-18.58, -2.82) * mm, "end": v(-18.59, -2.52) * mm});
            skLineSegment(sketch, "E684", {"start": v(-18.59, -2.52) * mm, "end": v(-18.59, -2.2) * mm});
            skLineSegment(sketch, "E685", {"start": v(-18.59, -2.2) * mm, "end": v(-18.58, -1.86) * mm});
            skLineSegment(sketch, "E686", {"start": v(-18.58, -1.86) * mm, "end": v(-18.56, -1.5) * mm});
            skLineSegment(sketch, "E687", {"start": v(-18.56, -1.5) * mm, "end": v(-18.53, -1.14) * mm});
            skLineSegment(sketch, "E688", {"start": v(-18.53, -1.14) * mm, "end": v(-18.5, -0.78) * mm});
            skLineSegment(sketch, "E689", {"start": v(-18.5, -0.78) * mm, "end": v(-18.45, -0.41) * mm});
            skLineSegment(sketch, "E690", {"start": v(-18.45, -0.41) * mm, "end": v(-18.4, -0.05) * mm});
            skLineSegment(sketch, "E691", {"start": v(-18.4, -0.05) * mm, "end": v(-18.33, 0.32) * mm});
            skLineSegment(sketch, "E692", {"start": v(-18.33, 0.32) * mm, "end": v(-18.25, 0.7) * mm});
            skLineSegment(sketch, "E693", {"start": v(-18.25, 0.7) * mm, "end": v(-18.17, 1.07) * mm});
            skLineSegment(sketch, "E694", {"start": v(-18.17, 1.07) * mm, "end": v(-18.08, 1.45) * mm});
            skLineSegment(sketch, "E695", {"start": v(-18.08, 1.45) * mm, "end": v(-17.98, 1.82) * mm});
            skLineSegment(sketch, "E696", {"start": v(-17.98, 1.82) * mm, "end": v(-17.87, 2.18) * mm});
            skLineSegment(sketch, "E697", {"start": v(-17.87, 2.18) * mm, "end": v(-17.75, 2.53) * mm});
            skLineSegment(sketch, "E698", {"start": v(-17.75, 2.53) * mm, "end": v(-17.62, 2.87) * mm});
            skLineSegment(sketch, "E699", {"start": v(-17.62, 2.87) * mm, "end": v(-17.49, 3.2) * mm});
            skLineSegment(sketch, "E700", {"start": v(-17.49, 3.2) * mm, "end": v(-17.34, 3.52) * mm});
            skLineSegment(sketch, "E701", {"start": v(-17.34, 3.52) * mm, "end": v(-17.19, 3.82) * mm});
            skLineSegment(sketch, "E702", {"start": v(-17.19, 3.82) * mm, "end": v(-17.02, 4.12) * mm});
            skLineSegment(sketch, "E703", {"start": v(-17.02, 4.12) * mm, "end": v(-16.82, 4.43) * mm});
            skLineSegment(sketch, "E704", {"start": v(-16.82, 4.43) * mm, "end": v(-16.62, 4.7) * mm});
            skLineSegment(sketch, "E705", {"start": v(-16.62, 4.7) * mm, "end": v(-16.42, 4.93) * mm});
            skLineSegment(sketch, "E706", {"start": v(-16.42, 4.93) * mm, "end": v(-16.32, 5.03) * mm});
            skLineSegment(sketch, "E707", {"start": v(-16.32, 5.03) * mm, "end": v(-16.22, 5.12) * mm});
            skLineSegment(sketch, "E708", {"start": v(-16.22, 5.12) * mm, "end": v(-16.13, 5.19) * mm});
            skLineSegment(sketch, "E709", {"start": v(-16.13, 5.19) * mm, "end": v(-16.03, 5.25) * mm});
            skLineSegment(sketch, "E710", {"start": v(-16.03, 5.25) * mm, "end": v(-15.94, 5.3) * mm});
            skLineSegment(sketch, "E711", {"start": v(-15.94, 5.3) * mm, "end": v(-15.85, 5.32) * mm});
            skLineSegment(sketch, "E712", {"start": v(-15.85, 5.32) * mm, "end": v(-15.77, 5.33) * mm});
            skLineSegment(sketch, "E713", {"start": v(-15.77, 5.33) * mm, "end": v(-15.68, 5.33) * mm});
            skLineSegment(sketch, "E714", {"start": v(-15.68, 5.33) * mm, "end": v(-15.6, 5.31) * mm});
            skLineSegment(sketch, "E715", {"start": v(-15.6, 5.31) * mm, "end": v(-15.53, 5.28) * mm});
            skLineSegment(sketch, "E716", {"start": v(-15.53, 5.28) * mm, "end": v(-15.45, 5.23) * mm});
            skLineSegment(sketch, "E717", {"start": v(-15.45, 5.23) * mm, "end": v(-15.39, 5.15) * mm});
            skLineSegment(sketch, "E718", {"start": v(-15.39, 5.15) * mm, "end": v(-15.32, 5.06) * mm});
            skLineSegment(sketch, "E719", {"start": v(-15.32, 5.06) * mm, "end": v(-15.27, 4.95) * mm});
            skLineSegment(sketch, "E720", {"start": v(-15.27, 4.95) * mm, "end": v(-15.22, 4.82) * mm});
            skLineSegment(sketch, "E721", {"start": v(-15.22, 4.82) * mm, "end": v(-15.17, 4.67) * mm});
            skLineSegment(sketch, "E722", {"start": v(-15.17, 4.67) * mm, "end": v(-15.13, 4.5) * mm});
            skLineSegment(sketch, "E723", {"start": v(-15.13, 4.5) * mm, "end": v(-15.1, 4.3) * mm});
            skLineSegment(sketch, "E724", {"start": v(-15.1, 4.3) * mm, "end": v(-15.07, 4.09) * mm});
            skLineSegment(sketch, "E725", {"start": v(-15.07, 4.09) * mm, "end": v(-15.05, 3.85) * mm});
            skLineSegment(sketch, "E726", {"start": v(-15.05, 3.85) * mm, "end": v(-15.03, 3.58) * mm});
            skLineSegment(sketch, "E727", {"start": v(-15.03, 3.58) * mm, "end": v(-15.03, 3.3) * mm});
            skLineSegment(sketch, "E728", {"start": v(-15.03, 3.3) * mm, "end": v(-15.04, 2.64) * mm});
            skLineSegment(sketch, "E729", {"start": v(-15.04, 2.64) * mm, "end": v(-15.1, 1.89) * mm});
            skLineSegment(sketch, "E730", {"start": v(-15.1, 1.89) * mm, "end": v(-15.16, 1.22) * mm});
            skLineSegment(sketch, "E731", {"start": v(-15.16, 1.22) * mm, "end": v(-15.23, 0.52) * mm});
            skLineSegment(sketch, "E732", {"start": v(-15.23, 0.52) * mm, "end": v(-15.32, -0.2) * mm});
            skLineSegment(sketch, "E733", {"start": v(-15.32, -0.2) * mm, "end": v(-15.42, -0.94) * mm});
            skLineSegment(sketch, "E734", {"start": v(-15.42, -0.94) * mm, "end": v(-15.63, -2.42) * mm});
            skLineSegment(sketch, "E735", {"start": v(-15.63, -2.42) * mm, "end": v(-15.87, -3.85) * mm});
            skLineSegment(sketch, "E736", {"start": v(-15.87, -3.85) * mm, "end": v(-16.1, -5.18) * mm});
            skLineSegment(sketch, "E737", {"start": v(-16.1, -5.18) * mm, "end": v(-16.32, -6.34) * mm});
            skLineSegment(sketch, "E738", {"start": v(-16.32, -6.34) * mm, "end": v(-16.5, -7.26) * mm});
            skLineSegment(sketch, "E739", {"start": v(-16.5, -7.26) * mm, "end": v(-16.65, -7.88) * mm});
            skLineSegment(sketch, "E740", {"start": v(-16.65, -7.88) * mm, "end": v(-16.65, -8) * mm});
            skLineSegment(sketch, "E741", {"start": v(-16.65, -8) * mm, "end": v(-16.63, -8.1) * mm});
            skLineSegment(sketch, "E742", {"start": v(-16.63, -8.1) * mm, "end": v(-16.6, -8.16) * mm});
            skLineSegment(sketch, "E743", {"start": v(-16.6, -8.16) * mm, "end": v(-16.56, -8.21) * mm});
            skLineSegment(sketch, "E744", {"start": v(-16.56, -8.21) * mm, "end": v(-16.5, -8.24) * mm});
            skLineSegment(sketch, "E745", {"start": v(-16.5, -8.24) * mm, "end": v(-16.45, -8.24) * mm});
            skLineSegment(sketch, "E746", {"start": v(-16.45, -8.24) * mm, "end": v(-16.39, -8.22) * mm});
            skLineSegment(sketch, "E747", {"start": v(-16.39, -8.22) * mm, "end": v(-16.33, -8.18) * mm});
            skLineSegment(sketch, "E748", {"start": v(-16.33, -8.18) * mm, "end": v(-16.26, -8.12) * mm});
            skLineSegment(sketch, "E749", {"start": v(-16.26, -8.12) * mm, "end": v(-16.21, -8.03) * mm});
            skLineSegment(sketch, "E750", {"start": v(-16.21, -8.03) * mm, "end": v(-16.17, -7.91) * mm});
            skLineSegment(sketch, "E751", {"start": v(-16.17, -7.91) * mm, "end": v(-16.14, -7.78) * mm});
            skLineSegment(sketch, "E752", {"start": v(-16.14, -7.78) * mm, "end": v(-15.66, -5.08) * mm});
            skLineSegment(sketch, "E753", {"start": v(-15.66, -5.08) * mm, "end": v(-15.36, -3.5) * mm});
            skLineSegment(sketch, "E754", {"start": v(-15.36, -3.5) * mm, "end": v(-15.03, -1.88) * mm});
            skLineSegment(sketch, "E755", {"start": v(-15.03, -1.88) * mm, "end": v(-14.84, -1.06) * mm});
            skLineSegment(sketch, "E756", {"start": v(-14.84, -1.06) * mm, "end": v(-14.65, -0.28) * mm});
            skLineSegment(sketch, "E757", {"start": v(-14.65, -0.28) * mm, "end": v(-14.45, 0.47) * mm});
            skLineSegment(sketch, "E758", {"start": v(-14.45, 0.47) * mm, "end": v(-14.24, 1.2) * mm});
            skLineSegment(sketch, "E759", {"start": v(-14.24, 1.2) * mm, "end": v(-14.07, 1.7) * mm});
            skLineSegment(sketch, "E760", {"start": v(-14.07, 1.7) * mm, "end": v(-13.9, 2.17) * mm});
            skLineSegment(sketch, "E761", {"start": v(-13.9, 2.17) * mm, "end": v(-13.74, 2.6) * mm});
            skLineSegment(sketch, "E762", {"start": v(-13.74, 2.6) * mm, "end": v(-13.56, 3) * mm});
            skLineSegment(sketch, "E763", {"start": v(-13.56, 3) * mm, "end": v(-13.4, 3.36) * mm});
            skLineSegment(sketch, "E764", {"start": v(-13.4, 3.36) * mm, "end": v(-13.22, 3.67) * mm});
            skLineSegment(sketch, "E765", {"start": v(-13.22, 3.67) * mm, "end": v(-13.05, 3.95) * mm});
            skLineSegment(sketch, "E766", {"start": v(-13.05, 3.95) * mm, "end": v(-12.87, 4.18) * mm});
            skLineSegment(sketch, "E767", {"start": v(-12.87, 4.18) * mm, "end": v(-12.8, 4.28) * mm});
            skLineSegment(sketch, "E768", {"start": v(-12.8, 4.28) * mm, "end": v(-12.71, 4.37) * mm});
            skLineSegment(sketch, "E769", {"start": v(-12.71, 4.37) * mm, "end": v(-12.64, 4.44) * mm});
            skLineSegment(sketch, "E770", {"start": v(-12.64, 4.44) * mm, "end": v(-12.57, 4.49) * mm});
            skLineSegment(sketch, "E771", {"start": v(-12.57, 4.49) * mm, "end": v(-12.5, 4.52) * mm});
            skLineSegment(sketch, "E772", {"start": v(-12.5, 4.52) * mm, "end": v(-12.43, 4.54) * mm});
            skLineSegment(sketch, "E773", {"start": v(-12.43, 4.54) * mm, "end": v(-12.37, 4.54) * mm});
            skLineSegment(sketch, "E774", {"start": v(-12.37, 4.54) * mm, "end": v(-12.31, 4.52) * mm});
            skLineSegment(sketch, "E775", {"start": v(-12.31, 4.52) * mm, "end": v(-12.26, 4.48) * mm});
            skLineSegment(sketch, "E776", {"start": v(-12.26, 4.48) * mm, "end": v(-12.21, 4.42) * mm});
            skLineSegment(sketch, "E777", {"start": v(-12.21, 4.42) * mm, "end": v(-12.18, 4.34) * mm});
            skLineSegment(sketch, "E778", {"start": v(-12.18, 4.34) * mm, "end": v(-12.15, 4.23) * mm});
            skLineSegment(sketch, "E779", {"start": v(-12.15, 4.23) * mm, "end": v(-12.13, 4.1) * mm});
            skLineSegment(sketch, "E780", {"start": v(-12.13, 4.1) * mm, "end": v(-12.12, 3.95) * mm});
            skLineSegment(sketch, "E781", {"start": v(-12.12, 3.95) * mm, "end": v(-12.12, 3.78) * mm});
            skLineSegment(sketch, "E782", {"start": v(-12.12, 3.78) * mm, "end": v(-12.13, 3.58) * mm});
            skLineSegment(sketch, "E783", {"start": v(-12.13, 3.58) * mm, "end": v(-12.16, 3.21) * mm});
            skLineSegment(sketch, "E784", {"start": v(-12.16, 3.21) * mm, "end": v(-12.2, 2.78) * mm});
            skLineSegment(sketch, "E785", {"start": v(-12.2, 2.78) * mm, "end": v(-12.28, 2.28) * mm});
            skLineSegment(sketch, "E786", {"start": v(-12.28, 2.28) * mm, "end": v(-12.36, 1.71) * mm});
            skLineSegment(sketch, "E787", {"start": v(-12.36, 1.71) * mm, "end": v(-12.57, 0.46) * mm});
            skLineSegment(sketch, "E788", {"start": v(-12.57, 0.46) * mm, "end": v(-12.8, -0.87) * mm});
            skLineSegment(sketch, "E789", {"start": v(-12.8, -0.87) * mm, "end": v(-13.27, -3.46) * mm});
            skLineSegment(sketch, "E790", {"start": v(-13.27, -3.46) * mm, "end": v(-13.45, -4.53) * mm});
            skLineSegment(sketch, "E791", {"start": v(-13.45, -4.53) * mm, "end": v(-13.57, -5.34) * mm});
            skLineSegment(sketch, "E792", {"start": v(-13.57, -5.34) * mm, "end": v(-13.62, -5.82) * mm});
            skLineSegment(sketch, "E793", {"start": v(-13.62, -5.82) * mm, "end": v(-13.67, -6.28) * mm});
            skLineSegment(sketch, "E794", {"start": v(-13.67, -6.28) * mm, "end": v(-13.7, -6.7) * mm});
            skLineSegment(sketch, "E795", {"start": v(-13.7, -6.7) * mm, "end": v(-13.7, -7.1) * mm});
            skLineSegment(sketch, "E796", {"start": v(-13.7, -7.1) * mm, "end": v(-13.71, -7.48) * mm});
            skLineSegment(sketch, "E797", {"start": v(-13.71, -7.48) * mm, "end": v(-13.7, -7.82) * mm});
            skLineSegment(sketch, "E798", {"start": v(-13.7, -7.82) * mm, "end": v(-13.67, -8.13) * mm});
            skLineSegment(sketch, "E799", {"start": v(-13.67, -8.13) * mm, "end": v(-13.63, -8.42) * mm});
            skLineSegment(sketch, "E800", {"start": v(-13.63, -8.42) * mm, "end": v(-13.58, -8.67) * mm});
            skLineSegment(sketch, "E801", {"start": v(-13.58, -8.67) * mm, "end": v(-13.51, -8.9) * mm});
            skLineSegment(sketch, "E802", {"start": v(-13.51, -8.9) * mm, "end": v(-13.43, -9.09) * mm});
            skLineSegment(sketch, "E803", {"start": v(-13.43, -9.09) * mm, "end": v(-13.34, -9.25) * mm});
            skLineSegment(sketch, "E804", {"start": v(-13.34, -9.25) * mm, "end": v(-13.28, -9.32) * mm});
            skLineSegment(sketch, "E805", {"start": v(-13.28, -9.32) * mm, "end": v(-13.23, -9.38) * mm});
            skLineSegment(sketch, "E806", {"start": v(-13.23, -9.38) * mm, "end": v(-13.17, -9.43) * mm});
            skLineSegment(sketch, "E807", {"start": v(-13.17, -9.43) * mm, "end": v(-13.1, -9.48) * mm});
            skLineSegment(sketch, "E808", {"start": v(-13.1, -9.48) * mm, "end": v(-13.04, -9.51) * mm});
            skLineSegment(sketch, "E809", {"start": v(-13.04, -9.51) * mm, "end": v(-12.97, -9.54) * mm});
            skLineSegment(sketch, "E810", {"start": v(-12.97, -9.54) * mm, "end": v(-12.9, -9.57) * mm});
            skLineSegment(sketch, "E811", {"start": v(-12.9, -9.57) * mm, "end": v(-12.82, -9.58) * mm});
            skLineSegment(sketch, "E812", {"start": v(-12.82, -9.58) * mm, "end": v(-12.76, -9.57) * mm});
            skLineSegment(sketch, "E813", {"start": v(-12.76, -9.57) * mm, "end": v(-12.71, -9.56) * mm});
            skLineSegment(sketch, "E814", {"start": v(-12.71, -9.56) * mm, "end": v(-12.67, -9.54) * mm});
            skLineSegment(sketch, "E815", {"start": v(-12.67, -9.54) * mm, "end": v(-12.62, -9.51) * mm});
            skLineSegment(sketch, "E816", {"start": v(-12.62, -9.51) * mm, "end": v(-12.59, -9.48) * mm});
            skLineSegment(sketch, "E817", {"start": v(-12.59, -9.48) * mm, "end": v(-12.55, -9.43) * mm});
            skLineSegment(sketch, "E818", {"start": v(-12.55, -9.43) * mm, "end": v(-12.5, -9.32) * mm});
            skLineSegment(sketch, "E819", {"start": v(-12.5, -9.32) * mm, "end": v(-12.45, -9.2) * mm});
            skLineSegment(sketch, "E820", {"start": v(-12.45, -9.2) * mm, "end": v(-12.42, -9.1) * mm});
            skLineSegment(sketch, "E821", {"start": v(-12.42, -9.1) * mm, "end": v(-12.42, -8.99) * mm});
            skLineSegment(sketch, "E822", {"start": v(-12.42, -8.99) * mm, "end": v(-12.43, -8.9) * mm});
            skLineSegment(sketch, "E823", {"start": v(-12.43, -8.9) * mm, "end": v(-12.44, -8.86) * mm});
            skLineSegment(sketch, "E824", {"start": v(-12.44, -8.86) * mm, "end": v(-12.46, -8.83) * mm});
            skLineSegment(sketch, "E825", {"start": v(-12.46, -8.83) * mm, "end": v(-12.49, -8.82) * mm});
            skLineSegment(sketch, "E826", {"start": v(-12.49, -8.82) * mm, "end": v(-12.52, -8.82) * mm});
            skLineSegment(sketch, "E827", {"start": v(-12.52, -8.82) * mm, "end": v(-12.55, -8.84) * mm});
            skLineSegment(sketch, "E828", {"start": v(-12.55, -8.84) * mm, "end": v(-12.59, -8.87) * mm});
            skLineSegment(sketch, "E829", {"start": v(-12.59, -8.87) * mm, "end": v(-12.68, -8.96) * mm});
            skLineSegment(sketch, "E830", {"start": v(-12.68, -8.96) * mm, "end": v(-12.77, -9.05) * mm});
            skLineSegment(sketch, "E831", {"start": v(-12.77, -9.05) * mm, "end": v(-12.85, -9.11) * mm});
            skLineSegment(sketch, "E832", {"start": v(-12.85, -9.11) * mm, "end": v(-12.93, -9.15) * mm});
            skLineSegment(sketch, "E833", {"start": v(-12.93, -9.15) * mm, "end": v(-13, -9.16) * mm});
            skLineSegment(sketch, "E834", {"start": v(-13, -9.16) * mm, "end": v(-13.06, -9.14) * mm});
            skLineSegment(sketch, "E835", {"start": v(-13.06, -9.14) * mm, "end": v(-13.12, -9.1) * mm});
            skLineSegment(sketch, "E836", {"start": v(-13.12, -9.1) * mm, "end": v(-13.17, -9.02) * mm});
            skLineSegment(sketch, "E837", {"start": v(-13.17, -9.02) * mm, "end": v(-13.21, -8.92) * mm});
            skLineSegment(sketch, "E838", {"start": v(-13.21, -8.92) * mm, "end": v(-13.26, -8.8) * mm});
            skLineSegment(sketch, "E839", {"start": v(-13.26, -8.8) * mm, "end": v(-13.29, -8.66) * mm});
            skLineSegment(sketch, "E840", {"start": v(-13.29, -8.66) * mm, "end": v(-13.32, -8.49) * mm});
            skLineSegment(sketch, "E841", {"start": v(-13.32, -8.49) * mm, "end": v(-13.34, -8.3) * mm});
            skLineSegment(sketch, "E842", {"start": v(-13.34, -8.3) * mm, "end": v(-13.35, -8.1) * mm});
            skLineSegment(sketch, "E843", {"start": v(-13.35, -8.1) * mm, "end": v(-13.36, -7.86) * mm});
            skLineSegment(sketch, "E844", {"start": v(-13.36, -7.86) * mm, "end": v(-13.35, -7.33) * mm});
            skLineSegment(sketch, "E845", {"start": v(-13.35, -7.33) * mm, "end": v(-13.32, -6.73) * mm});
            skLineSegment(sketch, "E846", {"start": v(-13.32, -6.73) * mm, "end": v(-13.26, -6.07) * mm});
            skLineSegment(sketch, "E847", {"start": v(-13.26, -6.07) * mm, "end": v(-13.16, -5.34) * mm});
            skLineSegment(sketch, "E848", {"start": v(-13.16, -5.34) * mm, "end": v(-13.04, -4.55) * mm});
            skLineSegment(sketch, "E849", {"start": v(-13.04, -4.55) * mm, "end": v(-12.73, -2.84) * mm});
            skLineSegment(sketch, "E850", {"start": v(-12.73, -2.84) * mm, "end": v(-12.41, -1.26) * mm});
            skLineSegment(sketch, "E851", {"start": v(-12.41, -1.26) * mm, "end": v(-12.12, 0.2) * mm});
            skLineSegment(sketch, "E852", {"start": v(-12.12, 0.2) * mm, "end": v(-11.87, 1.52) * mm});
            skLineSegment(sketch, "E853", {"start": v(-11.87, 1.52) * mm, "end": v(-11.78, 2.14) * mm});
            skLineSegment(sketch, "E854", {"start": v(-11.78, 2.14) * mm, "end": v(-11.7, 2.71) * mm});
            skLineSegment(sketch, "E855", {"start": v(-11.7, 2.71) * mm, "end": v(-11.66, 3.25) * mm});
            skLineSegment(sketch, "E856", {"start": v(-11.66, 3.25) * mm, "end": v(-11.64, 3.76) * mm});
            skLineSegment(sketch, "E857", {"start": v(-9.47, -5.06) * mm, "end": v(-9.48, -5.37) * mm});
            skLineSegment(sketch, "E858", {"start": v(-9.48, -5.37) * mm, "end": v(-9.5, -5.65) * mm});
            skLineSegment(sketch, "E859", {"start": v(-9.5, -5.65) * mm, "end": v(-9.53, -5.9) * mm});
            skLineSegment(sketch, "E860", {"start": v(-9.53, -5.9) * mm, "end": v(-9.56, -6.13) * mm});
            skLineSegment(sketch, "E861", {"start": v(-9.56, -6.13) * mm, "end": v(-9.6, -6.33) * mm});
            skLineSegment(sketch, "E862", {"start": v(-9.6, -6.33) * mm, "end": v(-9.65, -6.5) * mm});
            skLineSegment(sketch, "E863", {"start": v(-9.65, -6.5) * mm, "end": v(-9.7, -6.64) * mm});
            skLineSegment(sketch, "E864", {"start": v(-9.7, -6.64) * mm, "end": v(-9.74, -6.76) * mm});
            skLineSegment(sketch, "E865", {"start": v(-9.74, -6.76) * mm, "end": v(-9.8, -6.68) * mm});
            skLineSegment(sketch, "E866", {"start": v(-9.8, -6.68) * mm, "end": v(-9.84, -6.57) * mm});
            skLineSegment(sketch, "E867", {"start": v(-9.84, -6.57) * mm, "end": v(-9.89, -6.45) * mm});
            skLineSegment(sketch, "E868", {"start": v(-9.89, -6.45) * mm, "end": v(-9.93, -6.3) * mm});
            skLineSegment(sketch, "E869", {"start": v(-9.93, -6.3) * mm, "end": v(-9.96, -6.12) * mm});
            skLineSegment(sketch, "E870", {"start": v(-9.96, -6.12) * mm, "end": v(-9.99, -5.93) * mm});
            skLineSegment(sketch, "E871", {"start": v(-9.99, -5.93) * mm, "end": v(-10, -5.72) * mm});
            skLineSegment(sketch, "E872", {"start": v(-10, -5.72) * mm, "end": v(-10, -5.5) * mm});
            skLineSegment(sketch, "E873", {"start": v(-10, -5.5) * mm, "end": v(-10, -5.32) * mm});
            skLineSegment(sketch, "E874", {"start": v(-10, -5.32) * mm, "end": v(-10.02, -5.19) * mm});
            skLineSegment(sketch, "E875", {"start": v(-10.02, -5.19) * mm, "end": v(-10.04, -5.1) * mm});
            skLineSegment(sketch, "E876", {"start": v(-10.04, -5.1) * mm, "end": v(-10.06, -5.03) * mm});
            skLineSegment(sketch, "E877", {"start": v(-10.06, -5.03) * mm, "end": v(-10.1, -4.98) * mm});
            skLineSegment(sketch, "E878", {"start": v(-10.1, -4.98) * mm, "end": v(-10.12, -4.97) * mm});
            skLineSegment(sketch, "E879", {"start": v(-10.12, -4.97) * mm, "end": v(-10.13, -4.97) * mm});
            skLineSegment(sketch, "E880", {"start": v(-10.13, -4.97) * mm, "end": v(-9.85, -3.52) * mm});
            skLineSegment(sketch, "E881", {"start": v(-9.85, -3.52) * mm, "end": v(-9.55, -1.94) * mm});
            skLineSegment(sketch, "E882", {"start": v(-9.55, -1.94) * mm, "end": v(-9.56, -2.25) * mm});
            skLineSegment(sketch, "E883", {"start": v(-9.56, -2.25) * mm, "end": v(-9.56, -2.6) * mm});
            skLineSegment(sketch, "E884", {"start": v(-9.56, -2.6) * mm, "end": v(-9.55, -2.97) * mm});
            skLineSegment(sketch, "E885", {"start": v(-9.55, -2.97) * mm, "end": v(-9.52, -3.39) * mm});
            skLineSegment(sketch, "E886", {"start": v(-9.52, -3.39) * mm, "end": v(-9.48, -4.24) * mm});
            skLineSegment(sketch, "E887", {"start": v(-9.48, -4.24) * mm, "end": v(-9.47, -5.06) * mm});
            skLineSegment(sketch, "E888", {"start": v(-9.85, -6.9) * mm, "end": v(-9.88, -6.94) * mm});
            skLineSegment(sketch, "E889", {"start": v(-9.88, -6.94) * mm, "end": v(-9.9, -6.96) * mm});
            skLineSegment(sketch, "E890", {"start": v(-9.9, -6.96) * mm, "end": v(-9.94, -6.97) * mm});
            skLineSegment(sketch, "E891", {"start": v(-9.94, -6.97) * mm, "end": v(-9.97, -6.97) * mm});
            skLineSegment(sketch, "E892", {"start": v(-9.97, -6.97) * mm, "end": v(-10.01, -6.96) * mm});
            skLineSegment(sketch, "E893", {"start": v(-10.01, -6.96) * mm, "end": v(-10.05, -6.93) * mm});
            skLineSegment(sketch, "E894", {"start": v(-10.05, -6.93) * mm, "end": v(-10.09, -6.9) * mm});
            skLineSegment(sketch, "E895", {"start": v(-10.09, -6.9) * mm, "end": v(-10.12, -6.84) * mm});
            skLineSegment(sketch, "E896", {"start": v(-10.12, -6.84) * mm, "end": v(-10.14, -6.78) * mm});
            skLineSegment(sketch, "E897", {"start": v(-10.14, -6.78) * mm, "end": v(-10.16, -6.7) * mm});
            skLineSegment(sketch, "E898", {"start": v(-10.16, -6.7) * mm, "end": v(-10.2, -6.52) * mm});
            skLineSegment(sketch, "E899", {"start": v(-10.2, -6.52) * mm, "end": v(-10.2, -6.31) * mm});
            skLineSegment(sketch, "E900", {"start": v(-10.2, -6.31) * mm, "end": v(-10.19, -6.1) * mm});
            skLineSegment(sketch, "E901", {"start": v(-10.19, -6.1) * mm, "end": v(-10.15, -5.9) * mm});
            skLineSegment(sketch, "E902", {"start": v(-10.15, -5.9) * mm, "end": v(-10.1, -5.68) * mm});
            skLineSegment(sketch, "E903", {"start": v(-10.1, -5.68) * mm, "end": v(-10.08, -5.9) * mm});
            skLineSegment(sketch, "E904", {"start": v(-10.08, -5.9) * mm, "end": v(-10.07, -6.1) * mm});
            skLineSegment(sketch, "E905", {"start": v(-10.07, -6.1) * mm, "end": v(-10.04, -6.29) * mm});
            skLineSegment(sketch, "E906", {"start": v(-10.04, -6.29) * mm, "end": v(-10.01, -6.45) * mm});
            skLineSegment(sketch, "E907", {"start": v(-10.01, -6.45) * mm, "end": v(-9.98, -6.59) * mm});
            skLineSegment(sketch, "E908", {"start": v(-9.98, -6.59) * mm, "end": v(-9.94, -6.71) * mm});
            skLineSegment(sketch, "E909", {"start": v(-9.94, -6.71) * mm, "end": v(-9.9, -6.82) * mm});
            skLineSegment(sketch, "E910", {"start": v(-9.9, -6.82) * mm, "end": v(-9.85, -6.9) * mm});
            skLineSegment(sketch, "E911", {"start": v(-3.9, -0.34) * mm, "end": v(-3.89, -0.2) * mm});
            skLineSegment(sketch, "E912", {"start": v(-3.89, -0.2) * mm, "end": v(-3.9, -0.08) * mm});
            skLineSegment(sketch, "E913", {"start": v(-3.9, -0.08) * mm, "end": v(-3.9, 0.04) * mm});
            skLineSegment(sketch, "E914", {"start": v(-3.9, 0.04) * mm, "end": v(-3.94, 0.14) * mm});
            skLineSegment(sketch, "E915", {"start": v(-3.94, 0.14) * mm, "end": v(-3.97, 0.22) * mm});
            skLineSegment(sketch, "E916", {"start": v(-3.97, 0.22) * mm, "end": v(-4, 0.28) * mm});
            skLineSegment(sketch, "E917", {"start": v(-4, 0.28) * mm, "end": v(-4.05, 0.32) * mm});
            skLineSegment(sketch, "E918", {"start": v(-4.05, 0.32) * mm, "end": v(-4.1, 0.33) * mm});
            skLineSegment(sketch, "E919", {"start": v(-4.1, 0.33) * mm, "end": v(-4.16, 0.32) * mm});
            skLineSegment(sketch, "E920", {"start": v(-4.16, 0.32) * mm, "end": v(-4.2, 0.28) * mm});
            skLineSegment(sketch, "E921", {"start": v(-4.2, 0.28) * mm, "end": v(-4.25, 0.22) * mm});
            skLineSegment(sketch, "E922", {"start": v(-4.25, 0.22) * mm, "end": v(-4.3, 0.14) * mm});
            skLineSegment(sketch, "E923", {"start": v(-4.3, 0.14) * mm, "end": v(-4.33, 0.04) * mm});
            skLineSegment(sketch, "E924", {"start": v(-4.33, 0.04) * mm, "end": v(-4.36, -0.08) * mm});
            skLineSegment(sketch, "E925", {"start": v(-4.36, -0.08) * mm, "end": v(-4.39, -0.2) * mm});
            skLineSegment(sketch, "E926", {"start": v(-4.39, -0.2) * mm, "end": v(-4.4, -0.34) * mm});
            skLineSegment(sketch, "E927", {"start": v(-4.4, -0.34) * mm, "end": v(-4.4, -0.48) * mm});
            skLineSegment(sketch, "E928", {"start": v(-4.4, -0.48) * mm, "end": v(-4.4, -0.6) * mm});
            skLineSegment(sketch, "E929", {"start": v(-4.4, -0.6) * mm, "end": v(-4.38, -0.72) * mm});
            skLineSegment(sketch, "E930", {"start": v(-4.38, -0.72) * mm, "end": v(-4.35, -0.82) * mm});
            skLineSegment(sketch, "E931", {"start": v(-4.35, -0.82) * mm, "end": v(-4.32, -0.9) * mm});
            skLineSegment(sketch, "E932", {"start": v(-4.32, -0.9) * mm, "end": v(-4.28, -0.96) * mm});
            skLineSegment(sketch, "E933", {"start": v(-4.28, -0.96) * mm, "end": v(-4.24, -1) * mm});
            skLineSegment(sketch, "E934", {"start": v(-4.24, -1) * mm, "end": v(-4.19, -1.01) * mm});
            skLineSegment(sketch, "E935", {"start": v(-4.19, -1.01) * mm, "end": v(-4.13, -1) * mm});
            skLineSegment(sketch, "E936", {"start": v(-4.13, -1) * mm, "end": v(-4.08, -0.96) * mm});
            skLineSegment(sketch, "E937", {"start": v(-4.08, -0.96) * mm, "end": v(-4.04, -0.9) * mm});
            skLineSegment(sketch, "E938", {"start": v(-4.04, -0.9) * mm, "end": v(-4, -0.82) * mm});
            skLineSegment(sketch, "E939", {"start": v(-4, -0.82) * mm, "end": v(-3.96, -0.72) * mm});
            skLineSegment(sketch, "E940", {"start": v(-3.96, -0.72) * mm, "end": v(-3.93, -0.6) * mm});
            skLineSegment(sketch, "E941", {"start": v(-3.93, -0.6) * mm, "end": v(-3.9, -0.48) * mm});
            skLineSegment(sketch, "E942", {"start": v(-3.9, -0.48) * mm, "end": v(-3.9, -0.34) * mm});
            skLineSegment(sketch, "E943", {"start": v(-2.26, 1.14) * mm, "end": v(-2.36, 0.54) * mm});
            skLineSegment(sketch, "E944", {"start": v(-2.36, 0.54) * mm, "end": v(-2.48, -0.06) * mm});
            skLineSegment(sketch, "E945", {"start": v(-2.48, -0.06) * mm, "end": v(-2.6, -0.68) * mm});
            skLineSegment(sketch, "E946", {"start": v(-2.6, -0.68) * mm, "end": v(-2.75, -1.31) * mm});
            skLineSegment(sketch, "E947", {"start": v(-2.75, -1.31) * mm, "end": v(-2.9, -1.92) * mm});
            skLineSegment(sketch, "E948", {"start": v(-2.9, -1.92) * mm, "end": v(-3.06, -2.5) * mm});
            skLineSegment(sketch, "E949", {"start": v(-3.06, -2.5) * mm, "end": v(-3.22, -3.02) * mm});
            skLineSegment(sketch, "E950", {"start": v(-3.22, -3.02) * mm, "end": v(-3.38, -3.5) * mm});
            skLineSegment(sketch, "E951", {"start": v(-3.38, -3.5) * mm, "end": v(-3.26, -2.72) * mm});
            skLineSegment(sketch, "E952", {"start": v(-3.26, -2.72) * mm, "end": v(-3.11, -1.78) * mm});
            skLineSegment(sketch, "E953", {"start": v(-3.11, -1.78) * mm, "end": v(-2.94, -0.74) * mm});
            skLineSegment(sketch, "E954", {"start": v(-2.94, -0.74) * mm, "end": v(-2.75, 0.27) * mm});
            skLineSegment(sketch, "E955", {"start": v(-2.75, 0.27) * mm, "end": v(-2.57, 1.17) * mm});
            skLineSegment(sketch, "E956", {"start": v(-2.57, 1.17) * mm, "end": v(-2.41, 1.87) * mm});
            skLineSegment(sketch, "E957", {"start": v(-2.41, 1.87) * mm, "end": v(-2.34, 2.13) * mm});
            skLineSegment(sketch, "E958", {"start": v(-2.34, 2.13) * mm, "end": v(-2.28, 2.31) * mm});
            skLineSegment(sketch, "E959", {"start": v(-2.28, 2.31) * mm, "end": v(-2.23, 2.4) * mm});
            skLineSegment(sketch, "E960", {"start": v(-2.23, 2.4) * mm, "end": v(-2.21, 2.42) * mm});
            skLineSegment(sketch, "E961", {"start": v(-2.21, 2.42) * mm, "end": v(-2.2, 2.41) * mm});
            skLineSegment(sketch, "E962", {"start": v(-2.2, 2.41) * mm, "end": v(-2.18, 2.36) * mm});
            skLineSegment(sketch, "E963", {"start": v(-2.18, 2.36) * mm, "end": v(-2.17, 2.26) * mm});
            skLineSegment(sketch, "E964", {"start": v(-2.17, 2.26) * mm, "end": v(-2.16, 2.12) * mm});
            skLineSegment(sketch, "E965", {"start": v(-2.16, 2.12) * mm, "end": v(-2.17, 1.94) * mm});
            skLineSegment(sketch, "E966", {"start": v(-2.17, 1.94) * mm, "end": v(-2.2, 1.54) * mm});
            skLineSegment(sketch, "E967", {"start": v(-2.2, 1.54) * mm, "end": v(-2.26, 1.14) * mm});
            skLineSegment(sketch, "E968", {"start": v(-0.96, 1.14) * mm, "end": v(-1.06, 0.54) * mm});
            skLineSegment(sketch, "E969", {"start": v(-1.06, 0.54) * mm, "end": v(-1.18, -0.06) * mm});
            skLineSegment(sketch, "E970", {"start": v(-1.18, -0.06) * mm, "end": v(-1.3, -0.68) * mm});
            skLineSegment(sketch, "E971", {"start": v(-1.3, -0.68) * mm, "end": v(-1.45, -1.31) * mm});
            skLineSegment(sketch, "E972", {"start": v(-1.45, -1.31) * mm, "end": v(-1.6, -1.92) * mm});
            skLineSegment(sketch, "E973", {"start": v(-1.6, -1.92) * mm, "end": v(-1.75, -2.5) * mm});
            skLineSegment(sketch, "E974", {"start": v(-1.75, -2.5) * mm, "end": v(-1.91, -3.02) * mm});
            skLineSegment(sketch, "E975", {"start": v(-1.91, -3.02) * mm, "end": v(-2.08, -3.5) * mm});
            skLineSegment(sketch, "E976", {"start": v(-2.08, -3.5) * mm, "end": v(-1.96, -2.72) * mm});
            skLineSegment(sketch, "E977", {"start": v(-1.96, -2.72) * mm, "end": v(-1.8, -1.78) * mm});
            skLineSegment(sketch, "E978", {"start": v(-1.8, -1.78) * mm, "end": v(-1.63, -0.74) * mm});
            skLineSegment(sketch, "E979", {"start": v(-1.63, -0.74) * mm, "end": v(-1.45, 0.27) * mm});
            skLineSegment(sketch, "E980", {"start": v(-1.45, 0.27) * mm, "end": v(-1.27, 1.17) * mm});
            skLineSegment(sketch, "E981", {"start": v(-1.27, 1.17) * mm, "end": v(-1.1, 1.87) * mm});
            skLineSegment(sketch, "E982", {"start": v(-1.1, 1.87) * mm, "end": v(-1.03, 2.13) * mm});
            skLineSegment(sketch, "E983", {"start": v(-1.03, 2.13) * mm, "end": v(-0.97, 2.31) * mm});
            skLineSegment(sketch, "E984", {"start": v(-0.97, 2.31) * mm, "end": v(-0.93, 2.4) * mm});
            skLineSegment(sketch, "E985", {"start": v(-0.93, 2.4) * mm, "end": v(-0.9, 2.42) * mm});
            skLineSegment(sketch, "E986", {"start": v(-0.9, 2.42) * mm, "end": v(-0.9, 2.41) * mm});
            skLineSegment(sketch, "E987", {"start": v(-0.9, 2.41) * mm, "end": v(-0.88, 2.36) * mm});
            skLineSegment(sketch, "E988", {"start": v(-0.88, 2.36) * mm, "end": v(-0.86, 2.26) * mm});
            skLineSegment(sketch, "E989", {"start": v(-0.86, 2.26) * mm, "end": v(-0.86, 2.12) * mm});
            skLineSegment(sketch, "E990", {"start": v(-0.86, 2.12) * mm, "end": v(-0.87, 1.94) * mm});
            skLineSegment(sketch, "E991", {"start": v(-0.87, 1.94) * mm, "end": v(-0.9, 1.54) * mm});
            skLineSegment(sketch, "E992", {"start": v(-0.9, 1.54) * mm, "end": v(-0.96, 1.14) * mm});
            skLineSegment(sketch, "E993", {"start": v(-0.2, -3.66) * mm, "end": v(-0.29, -3.84) * mm});
            skLineSegment(sketch, "E994", {"start": v(-0.29, -3.84) * mm, "end": v(-0.38, -3.98) * mm});
            skLineSegment(sketch, "E995", {"start": v(-0.38, -3.98) * mm, "end": v(-0.47, -4.1) * mm});
            skLineSegment(sketch, "E996", {"start": v(-0.47, -4.1) * mm, "end": v(-0.57, -4.2) * mm});
            skLineSegment(sketch, "E997", {"start": v(-0.57, -4.2) * mm, "end": v(-0.66, -4.29) * mm});
            skLineSegment(sketch, "E998", {"start": v(-0.66, -4.29) * mm, "end": v(-0.73, -4.34) * mm});
            skLineSegment(sketch, "E999", {"start": v(-0.73, -4.34) * mm, "end": v(-0.8, -4.37) * mm});
            skLineSegment(sketch, "E1000", {"start": v(-0.8, -4.37) * mm, "end": v(-0.85, -4.38) * mm});
            skLineSegment(sketch, "E1001", {"start": v(-0.85, -4.38) * mm, "end": v(-0.7, -3.7) * mm});
            skLineSegment(sketch, "E1002", {"start": v(-0.7, -3.7) * mm, "end": v(-0.6, -3.26) * mm});
            skLineSegment(sketch, "E1003", {"start": v(-0.6, -3.26) * mm, "end": v(-0.48, -2.84) * mm});
            skLineSegment(sketch, "E1004", {"start": v(-0.48, -2.84) * mm, "end": v(-0.35, -2.44) * mm});
            skLineSegment(sketch, "E1005", {"start": v(-0.35, -2.44) * mm, "end": v(-0.23, -2.13) * mm});
            skLineSegment(sketch, "E1006", {"start": v(-0.23, -2.13) * mm, "end": v(-0.13, -1.91) * mm});
            skLineSegment(sketch, "E1007", {"start": v(-0.13, -1.91) * mm, "end": v(-0.09, -1.84) * mm});
            skLineSegment(sketch, "E1008", {"start": v(-0.09, -1.84) * mm, "end": v(-0.05, -1.78) * mm});
            skLineSegment(sketch, "E1009", {"start": v(-0.05, -1.78) * mm, "end": v(-0.01, -1.75) * mm});
            skLineSegment(sketch, "E1010", {"start": v(-0.01, -1.75) * mm, "end": v(0.02, -1.73) * mm});
            skLineSegment(sketch, "E1011", {"start": v(0.02, -1.73) * mm, "end": v(0.05, -1.72) * mm});
            skLineSegment(sketch, "E1012", {"start": v(0.05, -1.72) * mm, "end": v(0.07, -1.73) * mm});
            skLineSegment(sketch, "E1013", {"start": v(0.07, -1.73) * mm, "end": v(0.1, -1.76) * mm});
            skLineSegment(sketch, "E1014", {"start": v(0.1, -1.76) * mm, "end": v(0.1, -1.8) * mm});
            skLineSegment(sketch, "E1015", {"start": v(0.1, -1.8) * mm, "end": v(0.13, -1.91) * mm});
            skLineSegment(sketch, "E1016", {"start": v(0.13, -1.91) * mm, "end": v(0.14, -2.08) * mm});
            skLineSegment(sketch, "E1017", {"start": v(0.14, -2.08) * mm, "end": v(0.13, -2.26) * mm});
            skLineSegment(sketch, "E1018", {"start": v(0.13, -2.26) * mm, "end": v(0.11, -2.48) * mm});
            skLineSegment(sketch, "E1019", {"start": v(0.11, -2.48) * mm, "end": v(0.08, -2.72) * mm});
            skLineSegment(sketch, "E1020", {"start": v(0.08, -2.72) * mm, "end": v(0.03, -2.96) * mm});
            skLineSegment(sketch, "E1021", {"start": v(0.03, -2.96) * mm, "end": v(-0.04, -3.2) * mm});
            skLineSegment(sketch, "E1022", {"start": v(-0.04, -3.2) * mm, "end": v(-0.11, -3.44) * mm});
            skLineSegment(sketch, "E1023", {"start": v(-0.11, -3.44) * mm, "end": v(-0.2, -3.66) * mm});
            skLineSegment(sketch, "E1024", {"start": v(-10.45, -6.35) * mm, "end": v(-10.53, -6.62) * mm});
            skLineSegment(sketch, "E1025", {"start": v(-10.53, -6.62) * mm, "end": v(-10.62, -6.85) * mm});
            skLineSegment(sketch, "E1026", {"start": v(-10.62, -6.85) * mm, "end": v(-10.71, -7.04) * mm});
            skLineSegment(sketch, "E1027", {"start": v(-10.71, -7.04) * mm, "end": v(-10.76, -7.1) * mm});
            skLineSegment(sketch, "E1028", {"start": v(-10.76, -7.1) * mm, "end": v(-10.8, -7.16) * mm});
            skLineSegment(sketch, "E1029", {"start": v(-10.8, -7.16) * mm, "end": v(-10.85, -7.2) * mm});
            skLineSegment(sketch, "E1030", {"start": v(-10.85, -7.2) * mm, "end": v(-10.9, -7.22) * mm});
            skLineSegment(sketch, "E1031", {"start": v(-10.9, -7.22) * mm, "end": v(-10.95, -7.22) * mm});
            skLineSegment(sketch, "E1032", {"start": v(-10.95, -7.22) * mm, "end": v(-11, -7.2) * mm});
            skLineSegment(sketch, "E1033", {"start": v(-11, -7.2) * mm, "end": v(-11.06, -7.14) * mm});
            skLineSegment(sketch, "E1034", {"start": v(-11.06, -7.14) * mm, "end": v(-11.1, -7.07) * mm});
            skLineSegment(sketch, "E1035", {"start": v(-11.1, -7.07) * mm, "end": v(-11.16, -6.96) * mm});
            skLineSegment(sketch, "E1036", {"start": v(-11.16, -6.96) * mm, "end": v(-11.2, -6.82) * mm});
            skLineSegment(sketch, "E1037", {"start": v(-11.2, -6.82) * mm, "end": v(-11.23, -6.64) * mm});
            skLineSegment(sketch, "E1038", {"start": v(-11.23, -6.64) * mm, "end": v(-11.25, -6.43) * mm});
            skLineSegment(sketch, "E1039", {"start": v(-11.25, -6.43) * mm, "end": v(-11.26, -6.17) * mm});
            skLineSegment(sketch, "E1040", {"start": v(-11.26, -6.17) * mm, "end": v(-11.26, -5.86) * mm});
            skLineSegment(sketch, "E1041", {"start": v(-11.26, -5.86) * mm, "end": v(-11.24, -5.5) * mm});
            skLineSegment(sketch, "E1042", {"start": v(-11.24, -5.5) * mm, "end": v(-11.2, -5.1) * mm});
            skLineSegment(sketch, "E1043", {"start": v(-11.2, -5.1) * mm, "end": v(-11.29, -5.46) * mm});
            skLineSegment(sketch, "E1044", {"start": v(-11.29, -5.46) * mm, "end": v(-11.4, -5.86) * mm});
            skLineSegment(sketch, "E1045", {"start": v(-11.4, -5.86) * mm, "end": v(-11.52, -6.27) * mm});
            skLineSegment(sketch, "E1046", {"start": v(-11.52, -6.27) * mm, "end": v(-11.65, -6.65) * mm});
            skLineSegment(sketch, "E1047", {"start": v(-11.65, -6.65) * mm, "end": v(-11.71, -6.8) * mm});
            skLineSegment(sketch, "E1048", {"start": v(-11.71, -6.8) * mm, "end": v(-11.78, -6.93) * mm});
            skLineSegment(sketch, "E1049", {"start": v(-11.78, -6.93) * mm, "end": v(-11.84, -7.03) * mm});
            skLineSegment(sketch, "E1050", {"start": v(-11.84, -7.03) * mm, "end": v(-11.9, -7.11) * mm});
            skLineSegment(sketch, "E1051", {"start": v(-11.9, -7.11) * mm, "end": v(-11.96, -7.17) * mm});
            skLineSegment(sketch, "E1052", {"start": v(-11.96, -7.17) * mm, "end": v(-12.01, -7.2) * mm});
            skLineSegment(sketch, "E1053", {"start": v(-12.01, -7.2) * mm, "end": v(-12.06, -7.2) * mm});
            skLineSegment(sketch, "E1054", {"start": v(-12.06, -7.2) * mm, "end": v(-12.11, -7.2) * mm});
            skLineSegment(sketch, "E1055", {"start": v(-12.11, -7.2) * mm, "end": v(-12.16, -7.16) * mm});
            skLineSegment(sketch, "E1056", {"start": v(-12.16, -7.16) * mm, "end": v(-12.2, -7.1) * mm});
            skLineSegment(sketch, "E1057", {"start": v(-12.2, -7.1) * mm, "end": v(-12.24, -7.03) * mm});
            skLineSegment(sketch, "E1058", {"start": v(-12.24, -7.03) * mm, "end": v(-12.28, -6.95) * mm});
            skLineSegment(sketch, "E1059", {"start": v(-12.28, -6.95) * mm, "end": v(-12.31, -6.84) * mm});
            skLineSegment(sketch, "E1060", {"start": v(-12.31, -6.84) * mm, "end": v(-12.34, -6.72) * mm});
            skLineSegment(sketch, "E1061", {"start": v(-12.34, -6.72) * mm, "end": v(-12.38, -6.42) * mm});
            skLineSegment(sketch, "E1062", {"start": v(-12.38, -6.42) * mm, "end": v(-12.4, -6.07) * mm});
            skLineSegment(sketch, "E1063", {"start": v(-12.4, -6.07) * mm, "end": v(-12.4, -5.67) * mm});
            skLineSegment(sketch, "E1064", {"start": v(-12.4, -5.67) * mm, "end": v(-12.39, -5.23) * mm});
            skLineSegment(sketch, "E1065", {"start": v(-12.39, -5.23) * mm, "end": v(-12.34, -4.75) * mm});
            skLineSegment(sketch, "E1066", {"start": v(-12.34, -4.75) * mm, "end": v(-12.28, -4.24) * mm});
            skLineSegment(sketch, "E1067", {"start": v(-12.28, -4.24) * mm, "end": v(-12.18, -3.71) * mm});
            skLineSegment(sketch, "E1068", {"start": v(-12.18, -3.71) * mm, "end": v(-12.05, -3.17) * mm});
            skLineSegment(sketch, "E1069", {"start": v(-12.05, -3.17) * mm, "end": v(-11.9, -2.62) * mm});
            skLineSegment(sketch, "E1070", {"start": v(-11.9, -2.62) * mm, "end": v(-11.8, -2.34) * mm});
            skLineSegment(sketch, "E1071", {"start": v(-11.8, -2.34) * mm, "end": v(-11.68, -2.09) * mm});
            skLineSegment(sketch, "E1072", {"start": v(-11.68, -2.09) * mm, "end": v(-11.56, -1.87) * mm});
            skLineSegment(sketch, "E1073", {"start": v(-11.56, -1.87) * mm, "end": v(-11.44, -1.68) * mm});
            skLineSegment(sketch, "E1074", {"start": v(-11.44, -1.68) * mm, "end": v(-11.3, -1.53) * mm});
            skLineSegment(sketch, "E1075", {"start": v(-11.3, -1.53) * mm, "end": v(-11.24, -1.47) * mm});
            skLineSegment(sketch, "E1076", {"start": v(-11.24, -1.47) * mm, "end": v(-11.17, -1.42) * mm});
            skLineSegment(sketch, "E1077", {"start": v(-11.17, -1.42) * mm, "end": v(-11.1, -1.39) * mm});
            skLineSegment(sketch, "E1078", {"start": v(-11.1, -1.39) * mm, "end": v(-11.04, -1.36) * mm});
            skLineSegment(sketch, "E1079", {"start": v(-11.04, -1.36) * mm, "end": v(-10.98, -1.35) * mm});
            skLineSegment(sketch, "E1080", {"start": v(-10.98, -1.35) * mm, "end": v(-10.91, -1.35) * mm});
            skLineSegment(sketch, "E1081", {"start": v(-10.91, -1.35) * mm, "end": v(-10.85, -1.36) * mm});
            skLineSegment(sketch, "E1082", {"start": v(-10.85, -1.36) * mm, "end": v(-10.78, -1.39) * mm});
            skLineSegment(sketch, "E1083", {"start": v(-10.78, -1.39) * mm, "end": v(-10.73, -1.43) * mm});
            skLineSegment(sketch, "E1084", {"start": v(-10.73, -1.43) * mm, "end": v(-10.67, -1.48) * mm});
            skLineSegment(sketch, "E1085", {"start": v(-10.67, -1.48) * mm, "end": v(-10.61, -1.56) * mm});
            skLineSegment(sketch, "E1086", {"start": v(-10.61, -1.56) * mm, "end": v(-10.56, -1.64) * mm});
            skLineSegment(sketch, "E1087", {"start": v(-10.56, -1.64) * mm, "end": v(-10.51, -1.75) * mm});
            skLineSegment(sketch, "E1088", {"start": v(-10.51, -1.75) * mm, "end": v(-10.47, -1.86) * mm});
            skLineSegment(sketch, "E1089", {"start": v(-10.47, -1.86) * mm, "end": v(-10.44, -1.96) * mm});
            skLineSegment(sketch, "E1090", {"start": v(-10.44, -1.96) * mm, "end": v(-10.43, -2.05) * mm});
            skLineSegment(sketch, "E1091", {"start": v(-10.43, -2.05) * mm, "end": v(-10.42, -2.13) * mm});
            skLineSegment(sketch, "E1092", {"start": v(-10.42, -2.13) * mm, "end": v(-10.43, -2.21) * mm});
            skLineSegment(sketch, "E1093", {"start": v(-10.43, -2.21) * mm, "end": v(-10.45, -2.28) * mm});
            skLineSegment(sketch, "E1094", {"start": v(-10.45, -2.28) * mm, "end": v(-10.47, -2.32) * mm});
            skLineSegment(sketch, "E1095", {"start": v(-10.47, -2.32) * mm, "end": v(-10.5, -2.34) * mm});
            skLineSegment(sketch, "E1096", {"start": v(-10.5, -2.34) * mm, "end": v(-10.53, -2.34) * mm});
            skLineSegment(sketch, "E1097", {"start": v(-10.53, -2.34) * mm, "end": v(-10.57, -2.13) * mm});
            skLineSegment(sketch, "E1098", {"start": v(-10.57, -2.13) * mm, "end": v(-10.61, -1.97) * mm});
            skLineSegment(sketch, "E1099", {"start": v(-10.61, -1.97) * mm, "end": v(-10.67, -1.85) * mm});
            skLineSegment(sketch, "E1100", {"start": v(-10.67, -1.85) * mm, "end": v(-10.7, -1.81) * mm});
            skLineSegment(sketch, "E1101", {"start": v(-10.7, -1.81) * mm, "end": v(-10.74, -1.78) * mm});
            skLineSegment(sketch, "E1102", {"start": v(-10.74, -1.78) * mm, "end": v(-10.77, -1.76) * mm});
            skLineSegment(sketch, "E1103", {"start": v(-10.77, -1.76) * mm, "end": v(-10.81, -1.75) * mm});
            skLineSegment(sketch, "E1104", {"start": v(-10.81, -1.75) * mm, "end": v(-10.85, -1.76) * mm});
            skLineSegment(sketch, "E1105", {"start": v(-10.85, -1.76) * mm, "end": v(-10.89, -1.77) * mm});
            skLineSegment(sketch, "E1106", {"start": v(-10.89, -1.77) * mm, "end": v(-10.93, -1.8) * mm});
            skLineSegment(sketch, "E1107", {"start": v(-10.93, -1.8) * mm, "end": v(-10.97, -1.83) * mm});
            skLineSegment(sketch, "E1108", {"start": v(-10.97, -1.83) * mm, "end": v(-11.06, -1.93) * mm});
            skLineSegment(sketch, "E1109", {"start": v(-11.06, -1.93) * mm, "end": v(-11.16, -2.1) * mm});
            skLineSegment(sketch, "E1110", {"start": v(-11.16, -2.1) * mm, "end": v(-11.27, -2.33) * mm});
            skLineSegment(sketch, "E1111", {"start": v(-11.27, -2.33) * mm, "end": v(-11.38, -2.6) * mm});
            skLineSegment(sketch, "E1112", {"start": v(-11.38, -2.6) * mm, "end": v(-11.49, -2.9) * mm});
            skLineSegment(sketch, "E1113", {"start": v(-11.49, -2.9) * mm, "end": v(-11.6, -3.22) * mm});
            skLineSegment(sketch, "E1114", {"start": v(-11.6, -3.22) * mm, "end": v(-11.7, -3.55) * mm});
            skLineSegment(sketch, "E1115", {"start": v(-11.7, -3.55) * mm, "end": v(-11.79, -3.9) * mm});
            skLineSegment(sketch, "E1116", {"start": v(-11.79, -3.9) * mm, "end": v(-11.87, -4.27) * mm});
            skLineSegment(sketch, "E1117", {"start": v(-11.87, -4.27) * mm, "end": v(-12, -4.95) * mm});
            skLineSegment(sketch, "E1118", {"start": v(-12, -4.95) * mm, "end": v(-12.08, -5.44) * mm});
            skLineSegment(sketch, "E1119", {"start": v(-12.08, -5.44) * mm, "end": v(-12.13, -5.93) * mm});
            skLineSegment(sketch, "E1120", {"start": v(-12.13, -5.93) * mm, "end": v(-12.13, -6.3) * mm});
            skLineSegment(sketch, "E1121", {"start": v(-12.13, -6.3) * mm, "end": v(-12.12, -6.44) * mm});
            skLineSegment(sketch, "E1122", {"start": v(-12.12, -6.44) * mm, "end": v(-12.1, -6.55) * mm});
            skLineSegment(sketch, "E1123", {"start": v(-12.1, -6.55) * mm, "end": v(-12.08, -6.64) * mm});
            skLineSegment(sketch, "E1124", {"start": v(-12.08, -6.64) * mm, "end": v(-12.05, -6.7) * mm});
            skLineSegment(sketch, "E1125", {"start": v(-12.05, -6.7) * mm, "end": v(-12.02, -6.74) * mm});
            skLineSegment(sketch, "E1126", {"start": v(-12.02, -6.74) * mm, "end": v(-11.97, -6.75) * mm});
            skLineSegment(sketch, "E1127", {"start": v(-11.97, -6.75) * mm, "end": v(-11.93, -6.73) * mm});
            skLineSegment(sketch, "E1128", {"start": v(-11.93, -6.73) * mm, "end": v(-11.88, -6.7) * mm});
            skLineSegment(sketch, "E1129", {"start": v(-11.88, -6.7) * mm, "end": v(-11.83, -6.64) * mm});
            skLineSegment(sketch, "E1130", {"start": v(-11.83, -6.64) * mm, "end": v(-11.78, -6.56) * mm});
            skLineSegment(sketch, "E1131", {"start": v(-11.78, -6.56) * mm, "end": v(-11.73, -6.46) * mm});
            skLineSegment(sketch, "E1132", {"start": v(-11.73, -6.46) * mm, "end": v(-11.67, -6.33) * mm});
            skLineSegment(sketch, "E1133", {"start": v(-11.67, -6.33) * mm, "end": v(-11.56, -6.02) * mm});
            skLineSegment(sketch, "E1134", {"start": v(-11.56, -6.02) * mm, "end": v(-11.4, -5.49) * mm});
            skLineSegment(sketch, "E1135", {"start": v(-11.4, -5.49) * mm, "end": v(-11.27, -4.92) * mm});
            skLineSegment(sketch, "E1136", {"start": v(-11.27, -4.92) * mm, "end": v(-11.14, -4.33) * mm});
            skLineSegment(sketch, "E1137", {"start": v(-11.14, -4.33) * mm, "end": v(-11.01, -3.73) * mm});
            skLineSegment(sketch, "E1138", {"start": v(-11.01, -3.73) * mm, "end": v(-10.92, -3.27) * mm});
            skLineSegment(sketch, "E1139", {"start": v(-10.92, -3.27) * mm, "end": v(-10.83, -2.94) * mm});
            skLineSegment(sketch, "E1140", {"start": v(-10.83, -2.94) * mm, "end": v(-10.78, -2.82) * mm});
            skLineSegment(sketch, "E1141", {"start": v(-10.78, -2.82) * mm, "end": v(-10.73, -2.73) * mm});
            skLineSegment(sketch, "E1142", {"start": v(-10.73, -2.73) * mm, "end": v(-10.7, -2.7) * mm});
            skLineSegment(sketch, "E1143", {"start": v(-10.7, -2.7) * mm, "end": v(-10.66, -2.69) * mm});
            skLineSegment(sketch, "E1144", {"start": v(-10.66, -2.69) * mm, "end": v(-10.63, -2.68) * mm});
            skLineSegment(sketch, "E1145", {"start": v(-10.63, -2.68) * mm, "end": v(-10.6, -2.68) * mm});
            skLineSegment(sketch, "E1146", {"start": v(-10.6, -2.68) * mm, "end": v(-10.47, -2.74) * mm});
            skLineSegment(sketch, "E1147", {"start": v(-10.47, -2.74) * mm, "end": v(-10.44, -2.75) * mm});
            skLineSegment(sketch, "E1148", {"start": v(-10.44, -2.75) * mm, "end": v(-10.4, -2.76) * mm});
            skLineSegment(sketch, "E1149", {"start": v(-10.4, -2.76) * mm, "end": v(-10.37, -2.76) * mm});
            skLineSegment(sketch, "E1150", {"start": v(-10.37, -2.76) * mm, "end": v(-10.34, -2.75) * mm});
            skLineSegment(sketch, "E1151", {"start": v(-10.34, -2.75) * mm, "end": v(-10.42, -3.02) * mm});
            skLineSegment(sketch, "E1152", {"start": v(-10.42, -3.02) * mm, "end": v(-10.53, -3.47) * mm});
            skLineSegment(sketch, "E1153", {"start": v(-10.53, -3.47) * mm, "end": v(-10.64, -4.03) * mm});
            skLineSegment(sketch, "E1154", {"start": v(-10.64, -4.03) * mm, "end": v(-10.75, -4.65) * mm});
            skLineSegment(sketch, "E1155", {"start": v(-10.75, -4.65) * mm, "end": v(-10.85, -5.26) * mm});
            skLineSegment(sketch, "E1156", {"start": v(-10.85, -5.26) * mm, "end": v(-10.9, -5.81) * mm});
            skLineSegment(sketch, "E1157", {"start": v(-10.9, -5.81) * mm, "end": v(-10.93, -6.25) * mm});
            skLineSegment(sketch, "E1158", {"start": v(-10.93, -6.25) * mm, "end": v(-10.93, -6.55) * mm});
            skLineSegment(sketch, "E1159", {"start": v(-10.93, -6.55) * mm, "end": v(-10.92, -6.66) * mm});
            skLineSegment(sketch, "E1160", {"start": v(-10.92, -6.66) * mm, "end": v(-10.9, -6.73) * mm});
            skLineSegment(sketch, "E1161", {"start": v(-10.9, -6.73) * mm, "end": v(-10.88, -6.78) * mm});
            skLineSegment(sketch, "E1162", {"start": v(-10.88, -6.78) * mm, "end": v(-10.85, -6.8) * mm});
            skLineSegment(sketch, "E1163", {"start": v(-10.85, -6.8) * mm, "end": v(-10.81, -6.78) * mm});
            skLineSegment(sketch, "E1164", {"start": v(-10.81, -6.78) * mm, "end": v(-10.78, -6.75) * mm});
            skLineSegment(sketch, "E1165", {"start": v(-10.78, -6.75) * mm, "end": v(-10.74, -6.71) * mm});
            skLineSegment(sketch, "E1166", {"start": v(-10.74, -6.71) * mm, "end": v(-10.7, -6.65) * mm});
            skLineSegment(sketch, "E1167", {"start": v(-10.7, -6.65) * mm, "end": v(-10.63, -6.48) * mm});
            skLineSegment(sketch, "E1168", {"start": v(-10.63, -6.48) * mm, "end": v(-10.56, -6.25) * mm});
            skLineSegment(sketch, "E1169", {"start": v(-10.56, -6.25) * mm, "end": v(-10.47, -5.93) * mm});
            skLineSegment(sketch, "E1170", {"start": v(-10.47, -5.93) * mm, "end": v(-10.46, -5.6) * mm});
            skLineSegment(sketch, "E1171", {"start": v(-10.46, -5.6) * mm, "end": v(-10.44, -5.46) * mm});
            skLineSegment(sketch, "E1172", {"start": v(-10.44, -5.46) * mm, "end": v(-10.41, -5.32) * mm});
            skLineSegment(sketch, "E1173", {"start": v(-10.41, -5.32) * mm, "end": v(-10.38, -5.16) * mm});
            skLineSegment(sketch, "E1174", {"start": v(-10.38, -5.16) * mm, "end": v(-10.34, -5.05) * mm});
            skLineSegment(sketch, "E1175", {"start": v(-10.34, -5.05) * mm, "end": v(-10.29, -4.98) * mm});
            skLineSegment(sketch, "E1176", {"start": v(-10.29, -4.98) * mm, "end": v(-10.26, -4.95) * mm});
            skLineSegment(sketch, "E1177", {"start": v(-10.26, -4.95) * mm, "end": v(-10.23, -4.94) * mm});
            skLineSegment(sketch, "E1178", {"start": v(-10.23, -4.94) * mm, "end": v(-9.97, -3.56) * mm});
            skLineSegment(sketch, "E1179", {"start": v(-9.97, -3.56) * mm, "end": v(-9.7, -2.1) * mm});
            skLineSegment(sketch, "E1180", {"start": v(-9.7, -2.1) * mm, "end": v(-9.66, -1.86) * mm});
            skLineSegment(sketch, "E1181", {"start": v(-9.66, -1.86) * mm, "end": v(-9.6, -1.63) * mm});
            skLineSegment(sketch, "E1182", {"start": v(-9.6, -1.63) * mm, "end": v(-9.55, -1.4) * mm});
            skLineSegment(sketch, "E1183", {"start": v(-9.55, -1.4) * mm, "end": v(-9.49, -1.2) * mm});
            skLineSegment(sketch, "E1184", {"start": v(-9.49, -1.2) * mm, "end": v(-9.42, -1) * mm});
            skLineSegment(sketch, "E1185", {"start": v(-9.42, -1) * mm, "end": v(-9.35, -0.86) * mm});
            skLineSegment(sketch, "E1186", {"start": v(-9.35, -0.86) * mm, "end": v(-9.28, -0.76) * mm});
            skLineSegment(sketch, "E1187", {"start": v(-9.28, -0.76) * mm, "end": v(-9.24, -0.72) * mm});
            skLineSegment(sketch, "E1188", {"start": v(-9.24, -0.72) * mm, "end": v(-9.2, -0.7) * mm});
            skLineSegment(sketch, "E1189", {"start": v(-9.2, -0.7) * mm, "end": v(-9.13, -0.69) * mm});
            skLineSegment(sketch, "E1190", {"start": v(-9.13, -0.69) * mm, "end": v(-9.07, -0.7) * mm});
            skLineSegment(sketch, "E1191", {"start": v(-9.07, -0.7) * mm, "end": v(-9.02, -0.73) * mm});
            skLineSegment(sketch, "E1192", {"start": v(-9.02, -0.73) * mm, "end": v(-8.97, -0.78) * mm});
            skLineSegment(sketch, "E1193", {"start": v(-8.97, -0.78) * mm, "end": v(-8.93, -0.84) * mm});
            skLineSegment(sketch, "E1194", {"start": v(-8.93, -0.84) * mm, "end": v(-8.91, -0.9) * mm});
            skLineSegment(sketch, "E1195", {"start": v(-8.91, -0.9) * mm, "end": v(-8.9, -0.97) * mm});
            skLineSegment(sketch, "E1196", {"start": v(-8.9, -0.97) * mm, "end": v(-8.9, -1.03) * mm});
            skLineSegment(sketch, "E1197", {"start": v(-8.9, -1.03) * mm, "end": v(-8.9, -1.08) * mm});
            skLineSegment(sketch, "E1198", {"start": v(-8.9, -1.08) * mm, "end": v(-8.93, -1.1) * mm});
            skLineSegment(sketch, "E1199", {"start": v(-8.93, -1.1) * mm, "end": v(-8.96, -1.1) * mm});
            skLineSegment(sketch, "E1200", {"start": v(-8.96, -1.1) * mm, "end": v(-9, -1.06) * mm});
            skLineSegment(sketch, "E1201", {"start": v(-9, -1.06) * mm, "end": v(-9.04, -1.02) * mm});
            skLineSegment(sketch, "E1202", {"start": v(-9.04, -1.02) * mm, "end": v(-9.1, -1) * mm});
            skLineSegment(sketch, "E1203", {"start": v(-9.1, -1) * mm, "end": v(-9.12, -1) * mm});
            skLineSegment(sketch, "E1204", {"start": v(-9.12, -1) * mm, "end": v(-9.14, -1) * mm});
            skLineSegment(sketch, "E1205", {"start": v(-9.14, -1) * mm, "end": v(-9.2, -1.04) * mm});
            skLineSegment(sketch, "E1206", {"start": v(-9.2, -1.04) * mm, "end": v(-9.24, -1.12) * mm});
            skLineSegment(sketch, "E1207", {"start": v(-9.24, -1.12) * mm, "end": v(-9.28, -1.22) * mm});
            skLineSegment(sketch, "E1208", {"start": v(-9.28, -1.22) * mm, "end": v(-9.31, -1.32) * mm});
            skLineSegment(sketch, "E1209", {"start": v(-9.31, -1.32) * mm, "end": v(-9.34, -1.44) * mm});
            skLineSegment(sketch, "E1210", {"start": v(-9.34, -1.44) * mm, "end": v(-9.36, -1.56) * mm});
            skLineSegment(sketch, "E1211", {"start": v(-9.36, -1.56) * mm, "end": v(-9.38, -1.7) * mm});
            skLineSegment(sketch, "E1212", {"start": v(-9.38, -1.7) * mm, "end": v(-9.4, -2) * mm});
            skLineSegment(sketch, "E1213", {"start": v(-9.4, -2) * mm, "end": v(-9.4, -2.3) * mm});
            skLineSegment(sketch, "E1214", {"start": v(-9.4, -2.3) * mm, "end": v(-9.38, -2.6) * mm});
            skLineSegment(sketch, "E1215", {"start": v(-9.38, -2.6) * mm, "end": v(-9.35, -2.87) * mm});
            skLineSegment(sketch, "E1216", {"start": v(-9.35, -2.87) * mm, "end": v(-9.32, -3.12) * mm});
            skLineSegment(sketch, "E1217", {"start": v(-9.32, -3.12) * mm, "end": v(-9.17, -4.05) * mm});
            skLineSegment(sketch, "E1218", {"start": v(-9.17, -4.05) * mm, "end": v(-9.14, -4.3) * mm});
            skLineSegment(sketch, "E1219", {"start": v(-9.14, -4.3) * mm, "end": v(-9.11, -4.54) * mm});
            skLineSegment(sketch, "E1220", {"start": v(-9.11, -4.54) * mm, "end": v(-9.1, -4.8) * mm});
            skLineSegment(sketch, "E1221", {"start": v(-9.1, -4.8) * mm, "end": v(-9.1, -5.06) * mm});
            skLineSegment(sketch, "E1222", {"start": v(-9.1, -5.06) * mm, "end": v(-9.11, -5.3) * mm});
            skLineSegment(sketch, "E1223", {"start": v(-9.11, -5.3) * mm, "end": v(-9.14, -5.55) * mm});
            skLineSegment(sketch, "E1224", {"start": v(-9.14, -5.55) * mm, "end": v(-9.18, -5.8) * mm});
            skLineSegment(sketch, "E1225", {"start": v(-9.18, -5.8) * mm, "end": v(-9.23, -6.05) * mm});
            skLineSegment(sketch, "E1226", {"start": v(-9.23, -6.05) * mm, "end": v(-9.3, -6.28) * mm});
            skLineSegment(sketch, "E1227", {"start": v(-9.3, -6.28) * mm, "end": v(-9.37, -6.5) * mm});
            skLineSegment(sketch, "E1228", {"start": v(-9.37, -6.5) * mm, "end": v(-9.45, -6.7) * mm});
            skLineSegment(sketch, "E1229", {"start": v(-9.45, -6.7) * mm, "end": v(-9.53, -6.87) * mm});
            skLineSegment(sketch, "E1230", {"start": v(-9.53, -6.87) * mm, "end": v(-9.5, -6.9) * mm});
            skLineSegment(sketch, "E1231", {"start": v(-9.5, -6.9) * mm, "end": v(-9.45, -6.9) * mm});
            skLineSegment(sketch, "E1232", {"start": v(-9.45, -6.9) * mm, "end": v(-9.41, -6.9) * mm});
            skLineSegment(sketch, "E1233", {"start": v(-9.41, -6.9) * mm, "end": v(-9.38, -6.9) * mm});
            skLineSegment(sketch, "E1234", {"start": v(-9.38, -6.9) * mm, "end": v(-9.34, -6.88) * mm});
            skLineSegment(sketch, "E1235", {"start": v(-9.34, -6.88) * mm, "end": v(-9.26, -6.82) * mm});
            skLineSegment(sketch, "E1236", {"start": v(-9.26, -6.82) * mm, "end": v(-9.2, -6.73) * mm});
            skLineSegment(sketch, "E1237", {"start": v(-9.2, -6.73) * mm, "end": v(-9.13, -6.61) * mm});
            skLineSegment(sketch, "E1238", {"start": v(-9.13, -6.61) * mm, "end": v(-9.06, -6.47) * mm});
            skLineSegment(sketch, "E1239", {"start": v(-9.06, -6.47) * mm, "end": v(-9, -6.32) * mm});
            skLineSegment(sketch, "E1240", {"start": v(-9, -6.32) * mm, "end": v(-8.94, -6.14) * mm});
            skLineSegment(sketch, "E1241", {"start": v(-8.94, -6.14) * mm, "end": v(-8.83, -5.7) * mm});
            skLineSegment(sketch, "E1242", {"start": v(-8.83, -5.7) * mm, "end": v(-8.7, -5.14) * mm});
            skLineSegment(sketch, "E1243", {"start": v(-8.7, -5.14) * mm, "end": v(-8.49, -4.04) * mm});
            skLineSegment(sketch, "E1244", {"start": v(-8.49, -4.04) * mm, "end": v(-8.27, -2.85) * mm});
            skLineSegment(sketch, "E1245", {"start": v(-8.27, -2.85) * mm, "end": v(-7.84, -0.53) * mm});
            skLineSegment(sketch, "E1246", {"start": v(-7.84, -0.53) * mm, "end": v(-7.4, 1.73) * mm});
            skLineSegment(sketch, "E1247", {"start": v(-7.4, 1.73) * mm, "end": v(-7.3, 2.18) * mm});
            skLineSegment(sketch, "E1248", {"start": v(-7.3, 2.18) * mm, "end": v(-7.24, 2.36) * mm});
            skLineSegment(sketch, "E1249", {"start": v(-7.24, 2.36) * mm, "end": v(-7.2, 2.51) * mm});
            skLineSegment(sketch, "E1250", {"start": v(-7.2, 2.51) * mm, "end": v(-7.14, 2.63) * mm});
            skLineSegment(sketch, "E1251", {"start": v(-7.14, 2.63) * mm, "end": v(-7.09, 2.7) * mm});
            skLineSegment(sketch, "E1252", {"start": v(-7.09, 2.7) * mm, "end": v(-7.06, 2.73) * mm});
            skLineSegment(sketch, "E1253", {"start": v(-7.06, 2.73) * mm, "end": v(-7.02, 2.75) * mm});
            skLineSegment(sketch, "E1254", {"start": v(-7.02, 2.75) * mm, "end": v(-6.99, 2.76) * mm});
            skLineSegment(sketch, "E1255", {"start": v(-6.99, 2.76) * mm, "end": v(-6.95, 2.76) * mm});
            skLineSegment(sketch, "E1256", {"start": v(-6.95, 2.76) * mm, "end": v(-6.83, 2.7) * mm});
            skLineSegment(sketch, "E1257", {"start": v(-6.83, 2.7) * mm, "end": v(-6.76, 2.69) * mm});
            skLineSegment(sketch, "E1258", {"start": v(-6.76, 2.69) * mm, "end": v(-6.7, 2.7) * mm});
            skLineSegment(sketch, "E1259", {"start": v(-6.7, 2.7) * mm, "end": v(-6.75, 2.51) * mm});
            skLineSegment(sketch, "E1260", {"start": v(-6.75, 2.51) * mm, "end": v(-6.82, 2.27) * mm});
            skLineSegment(sketch, "E1261", {"start": v(-6.82, 2.27) * mm, "end": v(-6.99, 1.6) * mm});
            skLineSegment(sketch, "E1262", {"start": v(-6.99, 1.6) * mm, "end": v(-7.18, 0.72) * mm});
            skLineSegment(sketch, "E1263", {"start": v(-7.18, 0.72) * mm, "end": v(-7.4, -0.3) * mm});
            skLineSegment(sketch, "E1264", {"start": v(-7.4, -0.3) * mm, "end": v(-7.85, -2.57) * mm});
            skLineSegment(sketch, "E1265", {"start": v(-7.85, -2.57) * mm, "end": v(-8.27, -4.8) * mm});
            skLineSegment(sketch, "E1266", {"start": v(-8.27, -4.8) * mm, "end": v(-8.14, -4.39) * mm});
            skLineSegment(sketch, "E1267", {"start": v(-8.14, -4.39) * mm, "end": v(-8.02, -4) * mm});
            skLineSegment(sketch, "E1268", {"start": v(-8.02, -4) * mm, "end": v(-7.9, -3.66) * mm});
            skLineSegment(sketch, "E1269", {"start": v(-7.9, -3.66) * mm, "end": v(-7.77, -3.35) * mm});
            skLineSegment(sketch, "E1270", {"start": v(-7.77, -3.35) * mm, "end": v(-7.6, -2.98) * mm});
            skLineSegment(sketch, "E1271", {"start": v(-7.6, -2.98) * mm, "end": v(-7.4, -2.6) * mm});
            skLineSegment(sketch, "E1272", {"start": v(-7.4, -2.6) * mm, "end": v(-7.28, -2.41) * mm});
            skLineSegment(sketch, "E1273", {"start": v(-7.28, -2.41) * mm, "end": v(-7.17, -2.24) * mm});
            skLineSegment(sketch, "E1274", {"start": v(-7.17, -2.24) * mm, "end": v(-7.06, -2.1) * mm});
            skLineSegment(sketch, "E1275", {"start": v(-7.06, -2.1) * mm, "end": v(-6.96, -1.97) * mm});
            skLineSegment(sketch, "E1276", {"start": v(-6.96, -1.97) * mm, "end": v(-6.86, -1.87) * mm});
            skLineSegment(sketch, "E1277", {"start": v(-6.86, -1.87) * mm, "end": v(-6.77, -1.8) * mm});
            skLineSegment(sketch, "E1278", {"start": v(-6.77, -1.8) * mm, "end": v(-6.73, -1.8) * mm});
            skLineSegment(sketch, "E1279", {"start": v(-6.73, -1.8) * mm, "end": v(-6.7, -1.8) * mm});
            skLineSegment(sketch, "E1280", {"start": v(-6.7, -1.8) * mm, "end": v(-6.66, -1.8) * mm});
            skLineSegment(sketch, "E1281", {"start": v(-6.66, -1.8) * mm, "end": v(-6.64, -1.81) * mm});
            skLineSegment(sketch, "E1282", {"start": v(-6.64, -1.81) * mm, "end": v(-6.74, -2.31) * mm});
            skLineSegment(sketch, "E1283", {"start": v(-6.74, -2.31) * mm, "end": v(-6.97, -3.5) * mm});
            skLineSegment(sketch, "E1284", {"start": v(-6.97, -3.5) * mm, "end": v(-7.1, -4.2) * mm});
            skLineSegment(sketch, "E1285", {"start": v(-7.1, -4.2) * mm, "end": v(-7.22, -4.9) * mm});
            skLineSegment(sketch, "E1286", {"start": v(-7.22, -4.9) * mm, "end": v(-7.32, -5.53) * mm});
            skLineSegment(sketch, "E1287", {"start": v(-7.32, -5.53) * mm, "end": v(-7.37, -6.04) * mm});
            skLineSegment(sketch, "E1288", {"start": v(-7.37, -6.04) * mm, "end": v(-7.39, -6.46) * mm});
            skLineSegment(sketch, "E1289", {"start": v(-7.39, -6.46) * mm, "end": v(-7.39, -6.6) * mm});
            skLineSegment(sketch, "E1290", {"start": v(-7.39, -6.6) * mm, "end": v(-7.37, -6.72) * mm});
            skLineSegment(sketch, "E1291", {"start": v(-7.37, -6.72) * mm, "end": v(-7.36, -6.8) * mm});
            skLineSegment(sketch, "E1292", {"start": v(-7.36, -6.8) * mm, "end": v(-7.34, -6.86) * mm});
            skLineSegment(sketch, "E1293", {"start": v(-7.34, -6.86) * mm, "end": v(-7.3, -6.9) * mm});
            skLineSegment(sketch, "E1294", {"start": v(-7.3, -6.9) * mm, "end": v(-7.28, -6.9) * mm});
            skLineSegment(sketch, "E1295", {"start": v(-7.28, -6.9) * mm, "end": v(-7.24, -6.9) * mm});
            skLineSegment(sketch, "E1296", {"start": v(-7.24, -6.9) * mm, "end": v(-7.2, -6.87) * mm});
            skLineSegment(sketch, "E1297", {"start": v(-7.2, -6.87) * mm, "end": v(-7.17, -6.82) * mm});
            skLineSegment(sketch, "E1298", {"start": v(-7.17, -6.82) * mm, "end": v(-7.13, -6.76) * mm});
            skLineSegment(sketch, "E1299", {"start": v(-7.13, -6.76) * mm, "end": v(-7.05, -6.58) * mm});
            skLineSegment(sketch, "E1300", {"start": v(-7.05, -6.58) * mm, "end": v(-6.97, -6.34) * mm});
            skLineSegment(sketch, "E1301", {"start": v(-6.97, -6.34) * mm, "end": v(-6.8, -5.75) * mm});
            skLineSegment(sketch, "E1302", {"start": v(-6.8, -5.75) * mm, "end": v(-6.66, -5.1) * mm});
            skLineSegment(sketch, "E1303", {"start": v(-6.66, -5.1) * mm, "end": v(-6.45, -4.02) * mm});
            skLineSegment(sketch, "E1304", {"start": v(-6.45, -4.02) * mm, "end": v(-6.44, -4) * mm});
            skLineSegment(sketch, "E1305", {"start": v(-6.44, -4) * mm, "end": v(-6.39, -3.73) * mm});
            skLineSegment(sketch, "E1306", {"start": v(-6.39, -3.73) * mm, "end": v(-6.33, -3.37) * mm});
            skLineSegment(sketch, "E1307", {"start": v(-6.33, -3.37) * mm, "end": v(-6.3, -2.94) * mm});
            skLineSegment(sketch, "E1308", {"start": v(-6.3, -2.94) * mm, "end": v(-6.27, -2.52) * mm});
            skLineSegment(sketch, "E1309", {"start": v(-6.27, -2.52) * mm, "end": v(-6.28, -2.13) * mm});
            skLineSegment(sketch, "E1310", {"start": v(-6.28, -2.13) * mm, "end": v(-6.29, -1.97) * mm});
            skLineSegment(sketch, "E1311", {"start": v(-6.29, -1.97) * mm, "end": v(-6.3, -1.84) * mm});
            skLineSegment(sketch, "E1312", {"start": v(-6.3, -1.84) * mm, "end": v(-6.33, -1.75) * mm});
            skLineSegment(sketch, "E1313", {"start": v(-6.33, -1.75) * mm, "end": v(-6.37, -1.7) * mm});
            skLineSegment(sketch, "E1314", {"start": v(-6.37, -1.7) * mm, "end": v(-6.24, -1.64) * mm});
            skLineSegment(sketch, "E1315", {"start": v(-6.24, -1.64) * mm, "end": v(-6.07, -1.57) * mm});
            skLineSegment(sketch, "E1316", {"start": v(-6.07, -1.57) * mm, "end": v(-6, -1.54) * mm});
            skLineSegment(sketch, "E1317", {"start": v(-6, -1.54) * mm, "end": v(-5.96, -1.54) * mm});
            skLineSegment(sketch, "E1318", {"start": v(-5.96, -1.54) * mm, "end": v(-5.92, -1.55) * mm});
            skLineSegment(sketch, "E1319", {"start": v(-5.92, -1.55) * mm, "end": v(-5.89, -1.58) * mm});
            skLineSegment(sketch, "E1320", {"start": v(-5.89, -1.58) * mm, "end": v(-5.87, -1.66) * mm});
            skLineSegment(sketch, "E1321", {"start": v(-5.87, -1.66) * mm, "end": v(-5.85, -1.79) * mm});
            skLineSegment(sketch, "E1322", {"start": v(-5.85, -1.79) * mm, "end": v(-5.85, -1.98) * mm});
            skLineSegment(sketch, "E1323", {"start": v(-5.85, -1.98) * mm, "end": v(-5.85, -2.24) * mm});
            skLineSegment(sketch, "E1324", {"start": v(-5.85, -2.24) * mm, "end": v(-5.87, -2.7) * mm});
            skLineSegment(sketch, "E1325", {"start": v(-5.87, -2.7) * mm, "end": v(-5.91, -3.23) * mm});
            skLineSegment(sketch, "E1326", {"start": v(-5.91, -3.23) * mm, "end": v(-5.97, -3.76) * mm});
            skLineSegment(sketch, "E1327", {"start": v(-5.97, -3.76) * mm, "end": v(-6.03, -4.22) * mm});
            skLineSegment(sketch, "E1328", {"start": v(-6.03, -4.22) * mm, "end": v(-6.14, -5.04) * mm});
            skLineSegment(sketch, "E1329", {"start": v(-6.14, -5.04) * mm, "end": v(-6.22, -5.8) * mm});
            skLineSegment(sketch, "E1330", {"start": v(-6.22, -5.8) * mm, "end": v(-6.24, -6.13) * mm});
            skLineSegment(sketch, "E1331", {"start": v(-6.24, -6.13) * mm, "end": v(-6.24, -6.4) * mm});
            skLineSegment(sketch, "E1332", {"start": v(-6.24, -6.4) * mm, "end": v(-6.22, -6.59) * mm});
            skLineSegment(sketch, "E1333", {"start": v(-6.22, -6.59) * mm, "end": v(-6.2, -6.66) * mm});
            skLineSegment(sketch, "E1334", {"start": v(-6.2, -6.66) * mm, "end": v(-6.17, -6.71) * mm});
            skLineSegment(sketch, "E1335", {"start": v(-6.17, -6.71) * mm, "end": v(-6.14, -6.74) * mm});
            skLineSegment(sketch, "E1336", {"start": v(-6.14, -6.74) * mm, "end": v(-6.1, -6.76) * mm});
            skLineSegment(sketch, "E1337", {"start": v(-6.1, -6.76) * mm, "end": v(-6.06, -6.76) * mm});
            skLineSegment(sketch, "E1338", {"start": v(-6.06, -6.76) * mm, "end": v(-6.02, -6.75) * mm});
            skLineSegment(sketch, "E1339", {"start": v(-6.02, -6.75) * mm, "end": v(-5.99, -6.72) * mm});
            skLineSegment(sketch, "E1340", {"start": v(-5.99, -6.72) * mm, "end": v(-5.95, -6.67) * mm});
            skLineSegment(sketch, "E1341", {"start": v(-5.95, -6.67) * mm, "end": v(-5.87, -6.54) * mm});
            skLineSegment(sketch, "E1342", {"start": v(-5.87, -6.54) * mm, "end": v(-5.8, -6.35) * mm});
            skLineSegment(sketch, "E1343", {"start": v(-5.8, -6.35) * mm, "end": v(-5.72, -6.12) * mm});
            skLineSegment(sketch, "E1344", {"start": v(-5.72, -6.12) * mm, "end": v(-5.65, -5.85) * mm});
            skLineSegment(sketch, "E1345", {"start": v(-5.65, -5.85) * mm, "end": v(-5.57, -5.54) * mm});
            skLineSegment(sketch, "E1346", {"start": v(-5.57, -5.54) * mm, "end": v(-5.43, -4.84) * mm});
            skLineSegment(sketch, "E1347", {"start": v(-5.43, -4.84) * mm, "end": v(-5.3, -4.06) * mm});
            skLineSegment(sketch, "E1348", {"start": v(-5.3, -4.06) * mm, "end": v(-5.35, -3.65) * mm});
            skLineSegment(sketch, "E1349", {"start": v(-5.35, -3.65) * mm, "end": v(-5.38, -3.21) * mm});
            skLineSegment(sketch, "E1350", {"start": v(-5.38, -3.21) * mm, "end": v(-5.38, -2.8) * mm});
            skLineSegment(sketch, "E1351", {"start": v(-5.38, -2.8) * mm, "end": v(-5.37, -2.6) * mm});
            skLineSegment(sketch, "E1352", {"start": v(-5.37, -2.6) * mm, "end": v(-5.35, -2.42) * mm});
            skLineSegment(sketch, "E1353", {"start": v(-5.35, -2.42) * mm, "end": v(-5.3, -2.09) * mm});
            skLineSegment(sketch, "E1354", {"start": v(-5.3, -2.09) * mm, "end": v(-5.25, -1.8) * mm});
            skLineSegment(sketch, "E1355", {"start": v(-5.25, -1.8) * mm, "end": v(-5.18, -1.59) * mm});
            skLineSegment(sketch, "E1356", {"start": v(-5.18, -1.59) * mm, "end": v(-5.11, -1.42) * mm});
            skLineSegment(sketch, "E1357", {"start": v(-5.11, -1.42) * mm, "end": v(-5.05, -1.3) * mm});
            skLineSegment(sketch, "E1358", {"start": v(-5.05, -1.3) * mm, "end": v(-4.98, -1.23) * mm});
            skLineSegment(sketch, "E1359", {"start": v(-4.98, -1.23) * mm, "end": v(-4.95, -1.22) * mm});
            skLineSegment(sketch, "E1360", {"start": v(-4.95, -1.22) * mm, "end": v(-4.93, -1.2) * mm});
            skLineSegment(sketch, "E1361", {"start": v(-4.93, -1.2) * mm, "end": v(-4.9, -1.21) * mm});
            skLineSegment(sketch, "E1362", {"start": v(-4.9, -1.21) * mm, "end": v(-4.88, -1.23) * mm});
            skLineSegment(sketch, "E1363", {"start": v(-4.88, -1.23) * mm, "end": v(-4.85, -1.25) * mm});
            skLineSegment(sketch, "E1364", {"start": v(-4.85, -1.25) * mm, "end": v(-4.84, -1.29) * mm});
            skLineSegment(sketch, "E1365", {"start": v(-4.84, -1.29) * mm, "end": v(-4.82, -1.38) * mm});
            skLineSegment(sketch, "E1366", {"start": v(-4.82, -1.38) * mm, "end": v(-4.81, -1.52) * mm});
            skLineSegment(sketch, "E1367", {"start": v(-4.81, -1.52) * mm, "end": v(-4.83, -1.68) * mm});
            skLineSegment(sketch, "E1368", {"start": v(-4.83, -1.68) * mm, "end": v(-4.84, -1.76) * mm});
            skLineSegment(sketch, "E1369", {"start": v(-4.84, -1.76) * mm, "end": v(-5.02, -3.19) * mm});
            skLineSegment(sketch, "E1370", {"start": v(-5.02, -3.19) * mm, "end": v(-5.16, -4.15) * mm});
            skLineSegment(sketch, "E1371", {"start": v(-5.16, -4.15) * mm, "end": v(-5.33, -5.13) * mm});
            skLineSegment(sketch, "E1372", {"start": v(-5.33, -5.13) * mm, "end": v(-5.43, -5.6) * mm});
            skLineSegment(sketch, "E1373", {"start": v(-5.43, -5.6) * mm, "end": v(-5.54, -6.04) * mm});
            skLineSegment(sketch, "E1374", {"start": v(-5.54, -6.04) * mm, "end": v(-5.65, -6.43) * mm});
            skLineSegment(sketch, "E1375", {"start": v(-5.65, -6.43) * mm, "end": v(-5.77, -6.77) * mm});
            skLineSegment(sketch, "E1376", {"start": v(-5.77, -6.77) * mm, "end": v(-5.84, -6.92) * mm});
            skLineSegment(sketch, "E1377", {"start": v(-5.84, -6.92) * mm, "end": v(-5.9, -7.04) * mm});
            skLineSegment(sketch, "E1378", {"start": v(-5.9, -7.04) * mm, "end": v(-5.97, -7.14) * mm});
            skLineSegment(sketch, "E1379", {"start": v(-5.97, -7.14) * mm, "end": v(-6.04, -7.21) * mm});
            skLineSegment(sketch, "E1380", {"start": v(-6.04, -7.21) * mm, "end": v(-6.12, -7.26) * mm});
            skLineSegment(sketch, "E1381", {"start": v(-6.12, -7.26) * mm, "end": v(-6.2, -7.29) * mm});
            skLineSegment(sketch, "E1382", {"start": v(-6.2, -7.29) * mm, "end": v(-6.27, -7.3) * mm});
            skLineSegment(sketch, "E1383", {"start": v(-6.27, -7.3) * mm, "end": v(-6.35, -7.27) * mm});
            skLineSegment(sketch, "E1384", {"start": v(-6.35, -7.27) * mm, "end": v(-6.39, -7.24) * mm});
            skLineSegment(sketch, "E1385", {"start": v(-6.39, -7.24) * mm, "end": v(-6.43, -7.2) * mm});
            skLineSegment(sketch, "E1386", {"start": v(-6.43, -7.2) * mm, "end": v(-6.46, -7.14) * mm});
            skLineSegment(sketch, "E1387", {"start": v(-6.46, -7.14) * mm, "end": v(-6.49, -7.07) * mm});
            skLineSegment(sketch, "E1388", {"start": v(-6.49, -7.07) * mm, "end": v(-6.53, -6.9) * mm});
            skLineSegment(sketch, "E1389", {"start": v(-6.53, -6.9) * mm, "end": v(-6.56, -6.7) * mm});
            skLineSegment(sketch, "E1390", {"start": v(-6.56, -6.7) * mm, "end": v(-6.57, -6.46) * mm});
            skLineSegment(sketch, "E1391", {"start": v(-6.57, -6.46) * mm, "end": v(-6.57, -6.2) * mm});
            skLineSegment(sketch, "E1392", {"start": v(-6.57, -6.2) * mm, "end": v(-6.56, -5.92) * mm});
            skLineSegment(sketch, "E1393", {"start": v(-6.56, -5.92) * mm, "end": v(-6.54, -5.61) * mm});
            skLineSegment(sketch, "E1394", {"start": v(-6.54, -5.61) * mm, "end": v(-6.47, -4.98) * mm});
            skLineSegment(sketch, "E1395", {"start": v(-6.47, -4.98) * mm, "end": v(-6.39, -4.34) * mm});
            skLineSegment(sketch, "E1396", {"start": v(-6.39, -4.34) * mm, "end": v(-6.4, -4.36) * mm});
            skLineSegment(sketch, "E1397", {"start": v(-6.4, -4.36) * mm, "end": v(-6.5, -4.9) * mm});
            skLineSegment(sketch, "E1398", {"start": v(-6.5, -4.9) * mm, "end": v(-6.61, -5.48) * mm});
            skLineSegment(sketch, "E1399", {"start": v(-6.61, -5.48) * mm, "end": v(-6.69, -5.83) * mm});
            skLineSegment(sketch, "E1400", {"start": v(-6.69, -5.83) * mm, "end": v(-6.77, -6.14) * mm});
            skLineSegment(sketch, "E1401", {"start": v(-6.77, -6.14) * mm, "end": v(-6.85, -6.44) * mm});
            skLineSegment(sketch, "E1402", {"start": v(-6.85, -6.44) * mm, "end": v(-6.95, -6.7) * mm});
            skLineSegment(sketch, "E1403", {"start": v(-6.95, -6.7) * mm, "end": v(-7.04, -6.94) * mm});
            skLineSegment(sketch, "E1404", {"start": v(-7.04, -6.94) * mm, "end": v(-7.1, -7.03) * mm});
            skLineSegment(sketch, "E1405", {"start": v(-7.1, -7.03) * mm, "end": v(-7.14, -7.1) * mm});
            skLineSegment(sketch, "E1406", {"start": v(-7.14, -7.1) * mm, "end": v(-7.2, -7.16) * mm});
            skLineSegment(sketch, "E1407", {"start": v(-7.2, -7.16) * mm, "end": v(-7.25, -7.2) * mm});
            skLineSegment(sketch, "E1408", {"start": v(-7.25, -7.2) * mm, "end": v(-7.3, -7.24) * mm});
            skLineSegment(sketch, "E1409", {"start": v(-7.3, -7.24) * mm, "end": v(-7.36, -7.25) * mm});
            skLineSegment(sketch, "E1410", {"start": v(-7.36, -7.25) * mm, "end": v(-7.42, -7.24) * mm});
            skLineSegment(sketch, "E1411", {"start": v(-7.42, -7.24) * mm, "end": v(-7.47, -7.22) * mm});
            skLineSegment(sketch, "E1412", {"start": v(-7.47, -7.22) * mm, "end": v(-7.53, -7.17) * mm});
            skLineSegment(sketch, "E1413", {"start": v(-7.53, -7.17) * mm, "end": v(-7.58, -7.1) * mm});
            skLineSegment(sketch, "E1414", {"start": v(-7.58, -7.1) * mm, "end": v(-7.63, -7) * mm});
            skLineSegment(sketch, "E1415", {"start": v(-7.63, -7) * mm, "end": v(-7.67, -6.86) * mm});
            skLineSegment(sketch, "E1416", {"start": v(-7.67, -6.86) * mm, "end": v(-7.7, -6.7) * mm});
            skLineSegment(sketch, "E1417", {"start": v(-7.7, -6.7) * mm, "end": v(-7.73, -6.5) * mm});
            skLineSegment(sketch, "E1418", {"start": v(-7.73, -6.5) * mm, "end": v(-7.74, -6.28) * mm});
            skLineSegment(sketch, "E1419", {"start": v(-7.74, -6.28) * mm, "end": v(-7.74, -6) * mm});
            skLineSegment(sketch, "E1420", {"start": v(-7.74, -6) * mm, "end": v(-7.72, -5.7) * mm});
            skLineSegment(sketch, "E1421", {"start": v(-7.72, -5.7) * mm, "end": v(-7.69, -5.33) * mm});
            skLineSegment(sketch, "E1422", {"start": v(-7.69, -5.33) * mm, "end": v(-7.64, -4.99) * mm});
            skLineSegment(sketch, "E1423", {"start": v(-7.64, -4.99) * mm, "end": v(-7.56, -4.6) * mm});
            skLineSegment(sketch, "E1424", {"start": v(-7.56, -4.6) * mm, "end": v(-7.47, -4.13) * mm});
            skLineSegment(sketch, "E1425", {"start": v(-7.47, -4.13) * mm, "end": v(-7.35, -3.61) * mm});
            skLineSegment(sketch, "E1426", {"start": v(-7.35, -3.61) * mm, "end": v(-7.32, -3.46) * mm});
            skLineSegment(sketch, "E1427", {"start": v(-7.32, -3.46) * mm, "end": v(-7.3, -3.32) * mm});
            skLineSegment(sketch, "E1428", {"start": v(-7.3, -3.32) * mm, "end": v(-7.29, -3.2) * mm});
            skLineSegment(sketch, "E1429", {"start": v(-7.29, -3.2) * mm, "end": v(-7.3, -3.1) * mm});
            skLineSegment(sketch, "E1430", {"start": v(-7.3, -3.1) * mm, "end": v(-7.3, -3.02) * mm});
            skLineSegment(sketch, "E1431", {"start": v(-7.3, -3.02) * mm, "end": v(-7.32, -3) * mm});
            skLineSegment(sketch, "E1432", {"start": v(-7.32, -3) * mm, "end": v(-7.33, -2.98) * mm});
            skLineSegment(sketch, "E1433", {"start": v(-7.33, -2.98) * mm, "end": v(-7.35, -2.98) * mm});
            skLineSegment(sketch, "E1434", {"start": v(-7.35, -2.98) * mm, "end": v(-7.37, -2.98) * mm});
            skLineSegment(sketch, "E1435", {"start": v(-7.37, -2.98) * mm, "end": v(-7.43, -3.02) * mm});
            skLineSegment(sketch, "E1436", {"start": v(-7.43, -3.02) * mm, "end": v(-7.5, -3.1) * mm});
            skLineSegment(sketch, "E1437", {"start": v(-7.5, -3.1) * mm, "end": v(-7.58, -3.25) * mm});
            skLineSegment(sketch, "E1438", {"start": v(-7.58, -3.25) * mm, "end": v(-7.67, -3.45) * mm});
            skLineSegment(sketch, "E1439", {"start": v(-7.67, -3.45) * mm, "end": v(-7.78, -3.71) * mm});
            skLineSegment(sketch, "E1440", {"start": v(-7.78, -3.71) * mm, "end": v(-7.87, -3.92) * mm});
            skLineSegment(sketch, "E1441", {"start": v(-7.87, -3.92) * mm, "end": v(-7.96, -4.18) * mm});
            skLineSegment(sketch, "E1442", {"start": v(-7.96, -4.18) * mm, "end": v(-8.16, -4.84) * mm});
            skLineSegment(sketch, "E1443", {"start": v(-8.16, -4.84) * mm, "end": v(-8.27, -5.26) * mm});
            skLineSegment(sketch, "E1444", {"start": v(-8.27, -5.26) * mm, "end": v(-8.4, -5.75) * mm});
            skLineSegment(sketch, "E1445", {"start": v(-8.4, -5.75) * mm, "end": v(-8.51, -6.32) * mm});
            skLineSegment(sketch, "E1446", {"start": v(-8.51, -6.32) * mm, "end": v(-8.64, -6.96) * mm});
            skLineSegment(sketch, "E1447", {"start": v(-8.64, -6.96) * mm, "end": v(-8.68, -7.1) * mm});
            skLineSegment(sketch, "E1448", {"start": v(-8.68, -7.1) * mm, "end": v(-8.7, -7.14) * mm});
            skLineSegment(sketch, "E1449", {"start": v(-8.7, -7.14) * mm, "end": v(-8.72, -7.16) * mm});
            skLineSegment(sketch, "E1450", {"start": v(-8.72, -7.16) * mm, "end": v(-8.75, -7.18) * mm});
            skLineSegment(sketch, "E1451", {"start": v(-8.75, -7.18) * mm, "end": v(-8.79, -7.19) * mm});
            skLineSegment(sketch, "E1452", {"start": v(-8.79, -7.19) * mm, "end": v(-8.87, -7.19) * mm});
            skLineSegment(sketch, "E1453", {"start": v(-8.87, -7.19) * mm, "end": v(-8.99, -7.2) * mm});
            skLineSegment(sketch, "E1454", {"start": v(-8.99, -7.2) * mm, "end": v(-9.03, -7.24) * mm});
            skLineSegment(sketch, "E1455", {"start": v(-9.03, -7.24) * mm, "end": v(-9.08, -7.3) * mm});
            skLineSegment(sketch, "E1456", {"start": v(-9.08, -7.3) * mm, "end": v(-8.94, -6.54) * mm});
            skLineSegment(sketch, "E1457", {"start": v(-8.94, -6.54) * mm, "end": v(-9, -6.7) * mm});
            skLineSegment(sketch, "E1458", {"start": v(-9, -6.7) * mm, "end": v(-9.08, -6.86) * mm});
            skLineSegment(sketch, "E1459", {"start": v(-9.08, -6.86) * mm, "end": v(-9.15, -6.97) * mm});
            skLineSegment(sketch, "E1460", {"start": v(-9.15, -6.97) * mm, "end": v(-9.21, -7.05) * mm});
            skLineSegment(sketch, "E1461", {"start": v(-9.21, -7.05) * mm, "end": v(-9.28, -7.11) * mm});
            skLineSegment(sketch, "E1462", {"start": v(-9.28, -7.11) * mm, "end": v(-9.35, -7.15) * mm});
            skLineSegment(sketch, "E1463", {"start": v(-9.35, -7.15) * mm, "end": v(-9.43, -7.17) * mm});
            skLineSegment(sketch, "E1464", {"start": v(-9.43, -7.17) * mm, "end": v(-9.5, -7.17) * mm});
            skLineSegment(sketch, "E1465", {"start": v(-9.5, -7.17) * mm, "end": v(-9.6, -7.14) * mm});
            skLineSegment(sketch, "E1466", {"start": v(-9.6, -7.14) * mm, "end": v(-9.67, -7.09) * mm});
            skLineSegment(sketch, "E1467", {"start": v(-9.67, -7.09) * mm, "end": v(-9.74, -7.16) * mm});
            skLineSegment(sketch, "E1468", {"start": v(-9.74, -7.16) * mm, "end": v(-9.8, -7.2) * mm});
            skLineSegment(sketch, "E1469", {"start": v(-9.8, -7.2) * mm, "end": v(-9.87, -7.24) * mm});
            skLineSegment(sketch, "E1470", {"start": v(-9.87, -7.24) * mm, "end": v(-9.93, -7.25) * mm});
            skLineSegment(sketch, "E1471", {"start": v(-9.93, -7.25) * mm, "end": v(-10, -7.24) * mm});
            skLineSegment(sketch, "E1472", {"start": v(-10, -7.24) * mm, "end": v(-10.06, -7.22) * mm});
            skLineSegment(sketch, "E1473", {"start": v(-10.06, -7.22) * mm, "end": v(-10.11, -7.2) * mm});
            skLineSegment(sketch, "E1474", {"start": v(-10.11, -7.2) * mm, "end": v(-10.17, -7.15) * mm});
            skLineSegment(sketch, "E1475", {"start": v(-10.17, -7.15) * mm, "end": v(-10.21, -7.1) * mm});
            skLineSegment(sketch, "E1476", {"start": v(-10.21, -7.1) * mm, "end": v(-10.26, -7.04) * mm});
            skLineSegment(sketch, "E1477", {"start": v(-10.26, -7.04) * mm, "end": v(-10.3, -6.98) * mm});
            skLineSegment(sketch, "E1478", {"start": v(-10.3, -6.98) * mm, "end": v(-10.33, -6.9) * mm});
            skLineSegment(sketch, "E1479", {"start": v(-10.33, -6.9) * mm, "end": v(-10.37, -6.77) * mm});
            skLineSegment(sketch, "E1480", {"start": v(-10.37, -6.77) * mm, "end": v(-10.4, -6.64) * mm});
            skLineSegment(sketch, "E1481", {"start": v(-10.4, -6.64) * mm, "end": v(-10.43, -6.5) * mm});
            skLineSegment(sketch, "E1482", {"start": v(-10.43, -6.5) * mm, "end": v(-10.45, -6.35) * mm});
            skLineSegment(sketch, "E1483", {"start": v(-9.96, -4.12) * mm, "end": v(-9.97, -4.17) * mm});
            skLineSegment(sketch, "E1484", {"start": v(-9.97, -4.17) * mm, "end": v(-10.12, -4.98) * mm});
            skLineSegment(sketch, "E1485", {"start": v(3.3, -1.85) * mm, "end": v(2.4, 2.06) * mm});
            skLineSegment(sketch, "E1486", {"start": v(2.4, 2.06) * mm, "end": v(2.36, 2.21) * mm});
            skLineSegment(sketch, "E1487", {"start": v(2.36, 2.21) * mm, "end": v(2.31, 2.34) * mm});
            skLineSegment(sketch, "E1488", {"start": v(2.31, 2.34) * mm, "end": v(2.26, 2.45) * mm});
            skLineSegment(sketch, "E1489", {"start": v(2.26, 2.45) * mm, "end": v(2.2, 2.53) * mm});
            skLineSegment(sketch, "E1490", {"start": v(2.2, 2.53) * mm, "end": v(2.13, 2.59) * mm});
            skLineSegment(sketch, "E1491", {"start": v(2.13, 2.59) * mm, "end": v(2.05, 2.63) * mm});
            skLineSegment(sketch, "E1492", {"start": v(2.05, 2.63) * mm, "end": v(1.95, 2.66) * mm});
            skLineSegment(sketch, "E1493", {"start": v(1.95, 2.66) * mm, "end": v(1.84, 2.68) * mm});
            skLineSegment(sketch, "E1494", {"start": v(1.84, 2.68) * mm, "end": v(1.84, 2.82) * mm});
            skLineSegment(sketch, "E1495", {"start": v(1.84, 2.82) * mm, "end": v(3.29, 2.82) * mm});
            skLineSegment(sketch, "E1496", {"start": v(3.29, 2.82) * mm, "end": v(3.29, 2.68) * mm});
            skLineSegment(sketch, "E1497", {"start": v(3.29, 2.68) * mm, "end": v(3.1, 2.66) * mm});
            skLineSegment(sketch, "E1498", {"start": v(3.1, 2.66) * mm, "end": v(3.04, 2.64) * mm});
            skLineSegment(sketch, "E1499", {"start": v(3.04, 2.64) * mm, "end": v(3, 2.62) * mm});
            skLineSegment(sketch, "E1500", {"start": v(3, 2.62) * mm, "end": v(2.96, 2.59) * mm});
            skLineSegment(sketch, "E1501", {"start": v(2.96, 2.59) * mm, "end": v(2.93, 2.55) * mm});
            skLineSegment(sketch, "E1502", {"start": v(2.93, 2.55) * mm, "end": v(2.92, 2.5) * mm});
            skLineSegment(sketch, "E1503", {"start": v(2.92, 2.5) * mm, "end": v(2.91, 2.44) * mm});
            skLineSegment(sketch, "E1504", {"start": v(2.91, 2.44) * mm, "end": v(2.93, 2.3) * mm});
            skLineSegment(sketch, "E1505", {"start": v(2.93, 2.3) * mm, "end": v(2.94, 2.27) * mm});
            skLineSegment(sketch, "E1506", {"start": v(2.94, 2.27) * mm, "end": v(3.62, -0.79) * mm});
            skLineSegment(sketch, "E1507", {"start": v(3.62, -0.79) * mm, "end": v(4.27, 1.96) * mm});
            skLineSegment(sketch, "E1508", {"start": v(4.27, 1.96) * mm, "end": v(4.23, 2.15) * mm});
            skLineSegment(sketch, "E1509", {"start": v(4.23, 2.15) * mm, "end": v(4.18, 2.31) * mm});
            skLineSegment(sketch, "E1510", {"start": v(4.18, 2.31) * mm, "end": v(4.13, 2.43) * mm});
            skLineSegment(sketch, "E1511", {"start": v(4.13, 2.43) * mm, "end": v(4.07, 2.53) * mm});
            skLineSegment(sketch, "E1512", {"start": v(4.07, 2.53) * mm, "end": v(4, 2.6) * mm});
            skLineSegment(sketch, "E1513", {"start": v(4, 2.6) * mm, "end": v(3.92, 2.64) * mm});
            skLineSegment(sketch, "E1514", {"start": v(3.92, 2.64) * mm, "end": v(3.82, 2.67) * mm});
            skLineSegment(sketch, "E1515", {"start": v(3.82, 2.67) * mm, "end": v(3.7, 2.68) * mm});
            skLineSegment(sketch, "E1516", {"start": v(3.7, 2.68) * mm, "end": v(3.7, 2.68) * mm});
            skLineSegment(sketch, "E1517", {"start": v(3.7, 2.68) * mm, "end": v(3.7, 2.82) * mm});
            skLineSegment(sketch, "E1518", {"start": v(3.7, 2.82) * mm, "end": v(5.15, 2.82) * mm});
            skLineSegment(sketch, "E1519", {"start": v(5.15, 2.82) * mm, "end": v(5.15, 2.68) * mm});
            skLineSegment(sketch, "E1520", {"start": v(5.15, 2.68) * mm, "end": v(5.04, 2.67) * mm});
            skLineSegment(sketch, "E1521", {"start": v(5.04, 2.67) * mm, "end": v(4.96, 2.66) * mm});
            skLineSegment(sketch, "E1522", {"start": v(4.96, 2.66) * mm, "end": v(4.89, 2.65) * mm});
            skLineSegment(sketch, "E1523", {"start": v(4.89, 2.65) * mm, "end": v(4.84, 2.62) * mm});
            skLineSegment(sketch, "E1524", {"start": v(4.84, 2.62) * mm, "end": v(4.8, 2.6) * mm});
            skLineSegment(sketch, "E1525", {"start": v(4.8, 2.6) * mm, "end": v(4.78, 2.55) * mm});
            skLineSegment(sketch, "E1526", {"start": v(4.78, 2.55) * mm, "end": v(4.77, 2.5) * mm});
            skLineSegment(sketch, "E1527", {"start": v(4.77, 2.5) * mm, "end": v(4.77, 2.44) * mm});
            skLineSegment(sketch, "E1528", {"start": v(4.77, 2.44) * mm, "end": v(4.77, 2.34) * mm});
            skLineSegment(sketch, "E1529", {"start": v(4.77, 2.34) * mm, "end": v(4.78, 2.29) * mm});
            skLineSegment(sketch, "E1530", {"start": v(4.78, 2.29) * mm, "end": v(5.5, -0.83) * mm});
            skLineSegment(sketch, "E1531", {"start": v(5.5, -0.83) * mm, "end": v(6.15, 1.94) * mm});
            skLineSegment(sketch, "E1532", {"start": v(6.15, 1.94) * mm, "end": v(6.2, 2.17) * mm});
            skLineSegment(sketch, "E1533", {"start": v(6.2, 2.17) * mm, "end": v(6.22, 2.34) * mm});
            skLineSegment(sketch, "E1534", {"start": v(6.22, 2.34) * mm, "end": v(6.21, 2.42) * mm});
            skLineSegment(sketch, "E1535", {"start": v(6.21, 2.42) * mm, "end": v(6.2, 2.49) * mm});
            skLineSegment(sketch, "E1536", {"start": v(6.2, 2.49) * mm, "end": v(6.16, 2.54) * mm});
            skLineSegment(sketch, "E1537", {"start": v(6.16, 2.54) * mm, "end": v(6.11, 2.6) * mm});
            skLineSegment(sketch, "E1538", {"start": v(6.11, 2.6) * mm, "end": v(6.05, 2.63) * mm});
            skLineSegment(sketch, "E1539", {"start": v(6.05, 2.63) * mm, "end": v(5.98, 2.65) * mm});
            skLineSegment(sketch, "E1540", {"start": v(5.98, 2.65) * mm, "end": v(5.9, 2.67) * mm});
            skLineSegment(sketch, "E1541", {"start": v(5.9, 2.67) * mm, "end": v(5.8, 2.68) * mm});
            skLineSegment(sketch, "E1542", {"start": v(5.8, 2.68) * mm, "end": v(5.78, 2.68) * mm});
            skLineSegment(sketch, "E1543", {"start": v(5.78, 2.68) * mm, "end": v(5.78, 2.82) * mm});
            skLineSegment(sketch, "E1544", {"start": v(5.78, 2.82) * mm, "end": v(6.99, 2.82) * mm});
            skLineSegment(sketch, "E1545", {"start": v(6.99, 2.82) * mm, "end": v(6.99, 2.68) * mm});
            skLineSegment(sketch, "E1546", {"start": v(6.99, 2.68) * mm, "end": v(6.98, 2.68) * mm});
            skLineSegment(sketch, "E1547", {"start": v(6.98, 2.68) * mm, "end": v(6.87, 2.66) * mm});
            skLineSegment(sketch, "E1548", {"start": v(6.87, 2.66) * mm, "end": v(6.77, 2.63) * mm});
            skLineSegment(sketch, "E1549", {"start": v(6.77, 2.63) * mm, "end": v(6.68, 2.58) * mm});
            skLineSegment(sketch, "E1550", {"start": v(6.68, 2.58) * mm, "end": v(6.6, 2.51) * mm});
            skLineSegment(sketch, "E1551", {"start": v(6.6, 2.51) * mm, "end": v(6.53, 2.42) * mm});
            skLineSegment(sketch, "E1552", {"start": v(6.53, 2.42) * mm, "end": v(6.47, 2.3) * mm});
            skLineSegment(sketch, "E1553", {"start": v(6.47, 2.3) * mm, "end": v(6.42, 2.16) * mm});
            skLineSegment(sketch, "E1554", {"start": v(6.42, 2.16) * mm, "end": v(6.37, 2) * mm});
            skLineSegment(sketch, "E1555", {"start": v(6.37, 2) * mm, "end": v(5.45, -1.85) * mm});
            skLineSegment(sketch, "E1556", {"start": v(5.45, -1.85) * mm, "end": v(5.18, -1.85) * mm});
            skLineSegment(sketch, "E1557", {"start": v(5.18, -1.85) * mm, "end": v(4.36, 1.57) * mm});
            skLineSegment(sketch, "E1558", {"start": v(4.36, 1.57) * mm, "end": v(3.55, -1.85) * mm});
            skLineSegment(sketch, "E1559", {"start": v(3.55, -1.85) * mm, "end": v(3.3, -1.85) * mm});
            skLineSegment(sketch, "E1560", {"start": v(7.73, 1.38) * mm, "end": v(7.65, 1.38) * mm});
            skLineSegment(sketch, "E1561", {"start": v(7.65, 1.38) * mm, "end": v(7.58, 1.36) * mm});
            skLineSegment(sketch, "E1562", {"start": v(7.58, 1.36) * mm, "end": v(7.52, 1.34) * mm});
            skLineSegment(sketch, "E1563", {"start": v(7.52, 1.34) * mm, "end": v(7.46, 1.3) * mm});
            skLineSegment(sketch, "E1564", {"start": v(7.46, 1.3) * mm, "end": v(7.41, 1.25) * mm});
            skLineSegment(sketch, "E1565", {"start": v(7.41, 1.25) * mm, "end": v(7.37, 1.2) * mm});
            skLineSegment(sketch, "E1566", {"start": v(7.37, 1.2) * mm, "end": v(7.33, 1.13) * mm});
            skLineSegment(sketch, "E1567", {"start": v(7.33, 1.13) * mm, "end": v(7.3, 1.05) * mm});
            skLineSegment(sketch, "E1568", {"start": v(7.3, 1.05) * mm, "end": v(7.26, 0.95) * mm});
            skLineSegment(sketch, "E1569", {"start": v(7.26, 0.95) * mm, "end": v(7.24, 0.84) * mm});
            skLineSegment(sketch, "E1570", {"start": v(7.24, 0.84) * mm, "end": v(7.2, 0.57) * mm});
            skLineSegment(sketch, "E1571", {"start": v(7.2, 0.57) * mm, "end": v(7.17, 0.24) * mm});
            skLineSegment(sketch, "E1572", {"start": v(7.17, 0.24) * mm, "end": v(7.17, -0.17) * mm});
            skLineSegment(sketch, "E1573", {"start": v(7.17, -0.17) * mm, "end": v(7.17, -0.58) * mm});
            skLineSegment(sketch, "E1574", {"start": v(7.17, -0.58) * mm, "end": v(7.2, -0.91) * mm});
            skLineSegment(sketch, "E1575", {"start": v(7.2, -0.91) * mm, "end": v(7.24, -1.19) * mm});
            skLineSegment(sketch, "E1576", {"start": v(7.24, -1.19) * mm, "end": v(7.26, -1.3) * mm});
            skLineSegment(sketch, "E1577", {"start": v(7.26, -1.3) * mm, "end": v(7.3, -1.39) * mm});
            skLineSegment(sketch, "E1578", {"start": v(7.3, -1.39) * mm, "end": v(7.33, -1.47) * mm});
            skLineSegment(sketch, "E1579", {"start": v(7.33, -1.47) * mm, "end": v(7.37, -1.54) * mm});
            skLineSegment(sketch, "E1580", {"start": v(7.37, -1.54) * mm, "end": v(7.41, -1.6) * mm});
            skLineSegment(sketch, "E1581", {"start": v(7.41, -1.6) * mm, "end": v(7.46, -1.65) * mm});
            skLineSegment(sketch, "E1582", {"start": v(7.46, -1.65) * mm, "end": v(7.52, -1.68) * mm});
            skLineSegment(sketch, "E1583", {"start": v(7.52, -1.68) * mm, "end": v(7.58, -1.7) * mm});
            skLineSegment(sketch, "E1584", {"start": v(7.58, -1.7) * mm, "end": v(7.65, -1.73) * mm});
            skLineSegment(sketch, "E1585", {"start": v(7.65, -1.73) * mm, "end": v(7.73, -1.73) * mm});
            skLineSegment(sketch, "E1586", {"start": v(7.73, -1.73) * mm, "end": v(7.8, -1.72) * mm});
            skLineSegment(sketch, "E1587", {"start": v(7.8, -1.72) * mm, "end": v(7.87, -1.7) * mm});
            skLineSegment(sketch, "E1588", {"start": v(7.87, -1.7) * mm, "end": v(7.93, -1.68) * mm});
            skLineSegment(sketch, "E1589", {"start": v(7.93, -1.68) * mm, "end": v(8, -1.64) * mm});
            skLineSegment(sketch, "E1590", {"start": v(8, -1.64) * mm, "end": v(8.04, -1.6) * mm});
            skLineSegment(sketch, "E1591", {"start": v(8.04, -1.6) * mm, "end": v(8.09, -1.54) * mm});
            skLineSegment(sketch, "E1592", {"start": v(8.09, -1.54) * mm, "end": v(8.13, -1.47) * mm});
            skLineSegment(sketch, "E1593", {"start": v(8.13, -1.47) * mm, "end": v(8.16, -1.39) * mm});
            skLineSegment(sketch, "E1594", {"start": v(8.16, -1.39) * mm, "end": v(8.2, -1.3) * mm});
            skLineSegment(sketch, "E1595", {"start": v(8.2, -1.3) * mm, "end": v(8.22, -1.18) * mm});
            skLineSegment(sketch, "E1596", {"start": v(8.22, -1.18) * mm, "end": v(8.26, -0.91) * mm});
            skLineSegment(sketch, "E1597", {"start": v(8.26, -0.91) * mm, "end": v(8.29, -0.57) * mm});
            skLineSegment(sketch, "E1598", {"start": v(8.29, -0.57) * mm, "end": v(8.3, -0.17) * mm});
            skLineSegment(sketch, "E1599", {"start": v(8.3, -0.17) * mm, "end": v(8.29, 0.23) * mm});
            skLineSegment(sketch, "E1600", {"start": v(8.29, 0.23) * mm, "end": v(8.26, 0.57) * mm});
            skLineSegment(sketch, "E1601", {"start": v(8.26, 0.57) * mm, "end": v(8.22, 0.84) * mm});
            skLineSegment(sketch, "E1602", {"start": v(8.22, 0.84) * mm, "end": v(8.2, 0.95) * mm});
            skLineSegment(sketch, "E1603", {"start": v(8.2, 0.95) * mm, "end": v(8.16, 1.04) * mm});
            skLineSegment(sketch, "E1604", {"start": v(8.16, 1.04) * mm, "end": v(8.13, 1.12) * mm});
            skLineSegment(sketch, "E1605", {"start": v(8.13, 1.12) * mm, "end": v(8.09, 1.2) * mm});
            skLineSegment(sketch, "E1606", {"start": v(8.09, 1.2) * mm, "end": v(8.04, 1.25) * mm});
            skLineSegment(sketch, "E1607", {"start": v(8.04, 1.25) * mm, "end": v(8, 1.3) * mm});
            skLineSegment(sketch, "E1608", {"start": v(8, 1.3) * mm, "end": v(7.93, 1.34) * mm});
            skLineSegment(sketch, "E1609", {"start": v(7.93, 1.34) * mm, "end": v(7.87, 1.36) * mm});
            skLineSegment(sketch, "E1610", {"start": v(7.87, 1.36) * mm, "end": v(7.8, 1.38) * mm});
            skLineSegment(sketch, "E1611", {"start": v(7.8, 1.38) * mm, "end": v(7.73, 1.38) * mm});
            skLineSegment(sketch, "E1612", {"start": v(7.73, 1.52) * mm, "end": v(7.85, 1.51) * mm});
            skLineSegment(sketch, "E1613", {"start": v(7.85, 1.51) * mm, "end": v(7.96, 1.5) * mm});
            skLineSegment(sketch, "E1614", {"start": v(7.96, 1.5) * mm, "end": v(8.08, 1.45) * mm});
            skLineSegment(sketch, "E1615", {"start": v(8.08, 1.45) * mm, "end": v(8.19, 1.4) * mm});
            skLineSegment(sketch, "E1616", {"start": v(8.19, 1.4) * mm, "end": v(8.3, 1.33) * mm});
            skLineSegment(sketch, "E1617", {"start": v(8.3, 1.33) * mm, "end": v(8.4, 1.25) * mm});
            skLineSegment(sketch, "E1618", {"start": v(8.4, 1.25) * mm, "end": v(8.49, 1.15) * mm});
            skLineSegment(sketch, "E1619", {"start": v(8.49, 1.15) * mm, "end": v(8.58, 1.03) * mm});
            skLineSegment(sketch, "E1620", {"start": v(8.58, 1.03) * mm, "end": v(8.67, 0.9) * mm});
            skLineSegment(sketch, "E1621", {"start": v(8.67, 0.9) * mm, "end": v(8.74, 0.77) * mm});
            skLineSegment(sketch, "E1622", {"start": v(8.74, 0.77) * mm, "end": v(8.8, 0.63) * mm});
            skLineSegment(sketch, "E1623", {"start": v(8.8, 0.63) * mm, "end": v(8.85, 0.48) * mm});
            skLineSegment(sketch, "E1624", {"start": v(8.85, 0.48) * mm, "end": v(8.9, 0.33) * mm});
            skLineSegment(sketch, "E1625", {"start": v(8.9, 0.33) * mm, "end": v(8.92, 0.17) * mm});
            skLineSegment(sketch, "E1626", {"start": v(8.92, 0.17) * mm, "end": v(8.94, 0) * mm});
            skLineSegment(sketch, "E1627", {"start": v(8.94, 0) * mm, "end": v(8.94, -0.17) * mm});
            skLineSegment(sketch, "E1628", {"start": v(8.94, -0.17) * mm, "end": v(8.94, -0.34) * mm});
            skLineSegment(sketch, "E1629", {"start": v(8.94, -0.34) * mm, "end": v(8.92, -0.51) * mm});
            skLineSegment(sketch, "E1630", {"start": v(8.92, -0.51) * mm, "end": v(8.9, -0.67) * mm});
            skLineSegment(sketch, "E1631", {"start": v(8.9, -0.67) * mm, "end": v(8.85, -0.82) * mm});
            skLineSegment(sketch, "E1632", {"start": v(8.85, -0.82) * mm, "end": v(8.8, -0.97) * mm});
            skLineSegment(sketch, "E1633", {"start": v(8.8, -0.97) * mm, "end": v(8.74, -1.11) * mm});
            skLineSegment(sketch, "E1634", {"start": v(8.74, -1.11) * mm, "end": v(8.67, -1.25) * mm});
            skLineSegment(sketch, "E1635", {"start": v(8.67, -1.25) * mm, "end": v(8.58, -1.37) * mm});
            skLineSegment(sketch, "E1636", {"start": v(8.58, -1.37) * mm, "end": v(8.49, -1.49) * mm});
            skLineSegment(sketch, "E1637", {"start": v(8.49, -1.49) * mm, "end": v(8.4, -1.6) * mm});
            skLineSegment(sketch, "E1638", {"start": v(8.4, -1.6) * mm, "end": v(8.3, -1.68) * mm});
            skLineSegment(sketch, "E1639", {"start": v(8.3, -1.68) * mm, "end": v(8.19, -1.74) * mm});
            skLineSegment(sketch, "E1640", {"start": v(8.19, -1.74) * mm, "end": v(8.08, -1.8) * mm});
            skLineSegment(sketch, "E1641", {"start": v(8.08, -1.8) * mm, "end": v(7.96, -1.84) * mm});
            skLineSegment(sketch, "E1642", {"start": v(7.96, -1.84) * mm, "end": v(7.85, -1.86) * mm});
            skLineSegment(sketch, "E1643", {"start": v(7.85, -1.86) * mm, "end": v(7.73, -1.87) * mm});
            skLineSegment(sketch, "E1644", {"start": v(7.73, -1.87) * mm, "end": v(7.6, -1.86) * mm});
            skLineSegment(sketch, "E1645", {"start": v(7.6, -1.86) * mm, "end": v(7.49, -1.84) * mm});
            skLineSegment(sketch, "E1646", {"start": v(7.49, -1.84) * mm, "end": v(7.38, -1.8) * mm});
            skLineSegment(sketch, "E1647", {"start": v(7.38, -1.8) * mm, "end": v(7.27, -1.74) * mm});
            skLineSegment(sketch, "E1648", {"start": v(7.27, -1.74) * mm, "end": v(7.16, -1.68) * mm});
            skLineSegment(sketch, "E1649", {"start": v(7.16, -1.68) * mm, "end": v(7.06, -1.6) * mm});
            skLineSegment(sketch, "E1650", {"start": v(7.06, -1.6) * mm, "end": v(6.96, -1.49) * mm});
            skLineSegment(sketch, "E1651", {"start": v(6.96, -1.49) * mm, "end": v(6.87, -1.37) * mm});
            skLineSegment(sketch, "E1652", {"start": v(6.87, -1.37) * mm, "end": v(6.79, -1.25) * mm});
            skLineSegment(sketch, "E1653", {"start": v(6.79, -1.25) * mm, "end": v(6.71, -1.11) * mm});
            skLineSegment(sketch, "E1654", {"start": v(6.71, -1.11) * mm, "end": v(6.65, -0.97) * mm});
            skLineSegment(sketch, "E1655", {"start": v(6.65, -0.97) * mm, "end": v(6.6, -0.82) * mm});
            skLineSegment(sketch, "E1656", {"start": v(6.6, -0.82) * mm, "end": v(6.56, -0.67) * mm});
            skLineSegment(sketch, "E1657", {"start": v(6.56, -0.67) * mm, "end": v(6.53, -0.51) * mm});
            skLineSegment(sketch, "E1658", {"start": v(6.53, -0.51) * mm, "end": v(6.52, -0.34) * mm});
            skLineSegment(sketch, "E1659", {"start": v(6.52, -0.34) * mm, "end": v(6.51, -0.17) * mm});
            skLineSegment(sketch, "E1660", {"start": v(6.51, -0.17) * mm, "end": v(6.52, 0) * mm});
            skLineSegment(sketch, "E1661", {"start": v(6.52, 0) * mm, "end": v(6.53, 0.17) * mm});
            skLineSegment(sketch, "E1662", {"start": v(6.53, 0.17) * mm, "end": v(6.56, 0.33) * mm});
            skLineSegment(sketch, "E1663", {"start": v(6.56, 0.33) * mm, "end": v(6.6, 0.48) * mm});
            skLineSegment(sketch, "E1664", {"start": v(6.6, 0.48) * mm, "end": v(6.65, 0.63) * mm});
            skLineSegment(sketch, "E1665", {"start": v(6.65, 0.63) * mm, "end": v(6.71, 0.77) * mm});
            skLineSegment(sketch, "E1666", {"start": v(6.71, 0.77) * mm, "end": v(6.79, 0.9) * mm});
            skLineSegment(sketch, "E1667", {"start": v(6.79, 0.9) * mm, "end": v(6.87, 1.03) * mm});
            skLineSegment(sketch, "E1668", {"start": v(6.87, 1.03) * mm, "end": v(6.96, 1.15) * mm});
            skLineSegment(sketch, "E1669", {"start": v(6.96, 1.15) * mm, "end": v(7.06, 1.25) * mm});
            skLineSegment(sketch, "E1670", {"start": v(7.06, 1.25) * mm, "end": v(7.16, 1.33) * mm});
            skLineSegment(sketch, "E1671", {"start": v(7.16, 1.33) * mm, "end": v(7.27, 1.4) * mm});
            skLineSegment(sketch, "E1672", {"start": v(7.27, 1.4) * mm, "end": v(7.38, 1.45) * mm});
            skLineSegment(sketch, "E1673", {"start": v(7.38, 1.45) * mm, "end": v(7.49, 1.5) * mm});
            skLineSegment(sketch, "E1674", {"start": v(7.49, 1.5) * mm, "end": v(7.6, 1.51) * mm});
            skLineSegment(sketch, "E1675", {"start": v(7.6, 1.51) * mm, "end": v(7.73, 1.52) * mm});
            skLineSegment(sketch, "E1676", {"start": v(10.51, 1.38) * mm, "end": v(10.44, 1.38) * mm});
            skLineSegment(sketch, "E1677", {"start": v(10.44, 1.38) * mm, "end": v(10.37, 1.36) * mm});
            skLineSegment(sketch, "E1678", {"start": v(10.37, 1.36) * mm, "end": v(10.3, 1.34) * mm});
            skLineSegment(sketch, "E1679", {"start": v(10.3, 1.34) * mm, "end": v(10.25, 1.3) * mm});
            skLineSegment(sketch, "E1680", {"start": v(10.25, 1.3) * mm, "end": v(10.2, 1.25) * mm});
            skLineSegment(sketch, "E1681", {"start": v(10.2, 1.25) * mm, "end": v(10.15, 1.2) * mm});
            skLineSegment(sketch, "E1682", {"start": v(10.15, 1.2) * mm, "end": v(10.11, 1.13) * mm});
            skLineSegment(sketch, "E1683", {"start": v(10.11, 1.13) * mm, "end": v(10.08, 1.05) * mm});
            skLineSegment(sketch, "E1684", {"start": v(10.08, 1.05) * mm, "end": v(10.05, 0.95) * mm});
            skLineSegment(sketch, "E1685", {"start": v(10.05, 0.95) * mm, "end": v(10.02, 0.84) * mm});
            skLineSegment(sketch, "E1686", {"start": v(10.02, 0.84) * mm, "end": v(9.98, 0.57) * mm});
            skLineSegment(sketch, "E1687", {"start": v(9.98, 0.57) * mm, "end": v(9.96, 0.24) * mm});
            skLineSegment(sketch, "E1688", {"start": v(9.96, 0.24) * mm, "end": v(9.95, -0.17) * mm});
            skLineSegment(sketch, "E1689", {"start": v(9.95, -0.17) * mm, "end": v(9.96, -0.58) * mm});
            skLineSegment(sketch, "E1690", {"start": v(9.96, -0.58) * mm, "end": v(9.98, -0.91) * mm});
            skLineSegment(sketch, "E1691", {"start": v(9.98, -0.91) * mm, "end": v(10.02, -1.19) * mm});
            skLineSegment(sketch, "E1692", {"start": v(10.02, -1.19) * mm, "end": v(10.05, -1.3) * mm});
            skLineSegment(sketch, "E1693", {"start": v(10.05, -1.3) * mm, "end": v(10.08, -1.39) * mm});
            skLineSegment(sketch, "E1694", {"start": v(10.08, -1.39) * mm, "end": v(10.11, -1.47) * mm});
            skLineSegment(sketch, "E1695", {"start": v(10.11, -1.47) * mm, "end": v(10.15, -1.54) * mm});
            skLineSegment(sketch, "E1696", {"start": v(10.15, -1.54) * mm, "end": v(10.2, -1.6) * mm});
            skLineSegment(sketch, "E1697", {"start": v(10.2, -1.6) * mm, "end": v(10.25, -1.65) * mm});
            skLineSegment(sketch, "E1698", {"start": v(10.25, -1.65) * mm, "end": v(10.3, -1.68) * mm});
            skLineSegment(sketch, "E1699", {"start": v(10.3, -1.68) * mm, "end": v(10.37, -1.7) * mm});
            skLineSegment(sketch, "E1700", {"start": v(10.37, -1.7) * mm, "end": v(10.44, -1.73) * mm});
            skLineSegment(sketch, "E1701", {"start": v(10.44, -1.73) * mm, "end": v(10.51, -1.73) * mm});
            skLineSegment(sketch, "E1702", {"start": v(10.51, -1.73) * mm, "end": v(10.59, -1.72) * mm});
            skLineSegment(sketch, "E1703", {"start": v(10.59, -1.72) * mm, "end": v(10.65, -1.7) * mm});
            skLineSegment(sketch, "E1704", {"start": v(10.65, -1.7) * mm, "end": v(10.72, -1.68) * mm});
            skLineSegment(sketch, "E1705", {"start": v(10.72, -1.68) * mm, "end": v(10.77, -1.64) * mm});
            skLineSegment(sketch, "E1706", {"start": v(10.77, -1.64) * mm, "end": v(10.83, -1.6) * mm});
            skLineSegment(sketch, "E1707", {"start": v(10.83, -1.6) * mm, "end": v(10.87, -1.54) * mm});
            skLineSegment(sketch, "E1708", {"start": v(10.87, -1.54) * mm, "end": v(10.91, -1.47) * mm});
            skLineSegment(sketch, "E1709", {"start": v(10.91, -1.47) * mm, "end": v(10.95, -1.39) * mm});
            skLineSegment(sketch, "E1710", {"start": v(10.95, -1.39) * mm, "end": v(10.98, -1.3) * mm});
            skLineSegment(sketch, "E1711", {"start": v(10.98, -1.3) * mm, "end": v(11, -1.18) * mm});
            skLineSegment(sketch, "E1712", {"start": v(11, -1.18) * mm, "end": v(11.05, -0.91) * mm});
            skLineSegment(sketch, "E1713", {"start": v(11.05, -0.91) * mm, "end": v(11.07, -0.57) * mm});
            skLineSegment(sketch, "E1714", {"start": v(11.07, -0.57) * mm, "end": v(11.08, -0.17) * mm});
            skLineSegment(sketch, "E1715", {"start": v(11.08, -0.17) * mm, "end": v(11.07, 0.23) * mm});
            skLineSegment(sketch, "E1716", {"start": v(11.07, 0.23) * mm, "end": v(11.05, 0.57) * mm});
            skLineSegment(sketch, "E1717", {"start": v(11.05, 0.57) * mm, "end": v(11, 0.84) * mm});
            skLineSegment(sketch, "E1718", {"start": v(11, 0.84) * mm, "end": v(10.98, 0.95) * mm});
            skLineSegment(sketch, "E1719", {"start": v(10.98, 0.95) * mm, "end": v(10.95, 1.04) * mm});
            skLineSegment(sketch, "E1720", {"start": v(10.95, 1.04) * mm, "end": v(10.91, 1.12) * mm});
            skLineSegment(sketch, "E1721", {"start": v(10.91, 1.12) * mm, "end": v(10.87, 1.2) * mm});
            skLineSegment(sketch, "E1722", {"start": v(10.87, 1.2) * mm, "end": v(10.83, 1.25) * mm});
            skLineSegment(sketch, "E1723", {"start": v(10.83, 1.25) * mm, "end": v(10.77, 1.3) * mm});
            skLineSegment(sketch, "E1724", {"start": v(10.77, 1.3) * mm, "end": v(10.72, 1.34) * mm});
            skLineSegment(sketch, "E1725", {"start": v(10.72, 1.34) * mm, "end": v(10.65, 1.36) * mm});
            skLineSegment(sketch, "E1726", {"start": v(10.65, 1.36) * mm, "end": v(10.59, 1.38) * mm});
            skLineSegment(sketch, "E1727", {"start": v(10.59, 1.38) * mm, "end": v(10.51, 1.38) * mm});
            skLineSegment(sketch, "E1728", {"start": v(10.51, 1.52) * mm, "end": v(10.63, 1.51) * mm});
            skLineSegment(sketch, "E1729", {"start": v(10.63, 1.51) * mm, "end": v(10.75, 1.5) * mm});
            skLineSegment(sketch, "E1730", {"start": v(10.75, 1.5) * mm, "end": v(10.86, 1.45) * mm});
            skLineSegment(sketch, "E1731", {"start": v(10.86, 1.45) * mm, "end": v(10.97, 1.4) * mm});
            skLineSegment(sketch, "E1732", {"start": v(10.97, 1.4) * mm, "end": v(11.07, 1.33) * mm});
            skLineSegment(sketch, "E1733", {"start": v(11.07, 1.33) * mm, "end": v(11.18, 1.25) * mm});
            skLineSegment(sketch, "E1734", {"start": v(11.18, 1.25) * mm, "end": v(11.27, 1.15) * mm});
            skLineSegment(sketch, "E1735", {"start": v(11.27, 1.15) * mm, "end": v(11.36, 1.03) * mm});
            skLineSegment(sketch, "E1736", {"start": v(11.36, 1.03) * mm, "end": v(11.45, 0.9) * mm});
            skLineSegment(sketch, "E1737", {"start": v(11.45, 0.9) * mm, "end": v(11.52, 0.77) * mm});
            skLineSegment(sketch, "E1738", {"start": v(11.52, 0.77) * mm, "end": v(11.59, 0.63) * mm});
            skLineSegment(sketch, "E1739", {"start": v(11.59, 0.63) * mm, "end": v(11.64, 0.48) * mm});
            skLineSegment(sketch, "E1740", {"start": v(11.64, 0.48) * mm, "end": v(11.68, 0.33) * mm});
            skLineSegment(sketch, "E1741", {"start": v(11.68, 0.33) * mm, "end": v(11.7, 0.17) * mm});
            skLineSegment(sketch, "E1742", {"start": v(11.7, 0.17) * mm, "end": v(11.72, 0) * mm});
            skLineSegment(sketch, "E1743", {"start": v(11.72, 0) * mm, "end": v(11.73, -0.17) * mm});
            skLineSegment(sketch, "E1744", {"start": v(11.73, -0.17) * mm, "end": v(11.72, -0.34) * mm});
            skLineSegment(sketch, "E1745", {"start": v(11.72, -0.34) * mm, "end": v(11.7, -0.51) * mm});
            skLineSegment(sketch, "E1746", {"start": v(11.7, -0.51) * mm, "end": v(11.68, -0.67) * mm});
            skLineSegment(sketch, "E1747", {"start": v(11.68, -0.67) * mm, "end": v(11.64, -0.82) * mm});
            skLineSegment(sketch, "E1748", {"start": v(11.64, -0.82) * mm, "end": v(11.59, -0.97) * mm});
            skLineSegment(sketch, "E1749", {"start": v(11.59, -0.97) * mm, "end": v(11.52, -1.11) * mm});
            skLineSegment(sketch, "E1750", {"start": v(11.52, -1.11) * mm, "end": v(11.45, -1.25) * mm});
            skLineSegment(sketch, "E1751", {"start": v(11.45, -1.25) * mm, "end": v(11.36, -1.37) * mm});
            skLineSegment(sketch, "E1752", {"start": v(11.36, -1.37) * mm, "end": v(11.27, -1.49) * mm});
            skLineSegment(sketch, "E1753", {"start": v(11.27, -1.49) * mm, "end": v(11.18, -1.6) * mm});
            skLineSegment(sketch, "E1754", {"start": v(11.18, -1.6) * mm, "end": v(11.07, -1.68) * mm});
            skLineSegment(sketch, "E1755", {"start": v(11.07, -1.68) * mm, "end": v(10.97, -1.74) * mm});
            skLineSegment(sketch, "E1756", {"start": v(10.97, -1.74) * mm, "end": v(10.86, -1.8) * mm});
            skLineSegment(sketch, "E1757", {"start": v(10.86, -1.8) * mm, "end": v(10.75, -1.84) * mm});
            skLineSegment(sketch, "E1758", {"start": v(10.75, -1.84) * mm, "end": v(10.63, -1.86) * mm});
            skLineSegment(sketch, "E1759", {"start": v(10.63, -1.86) * mm, "end": v(10.51, -1.87) * mm});
            skLineSegment(sketch, "E1760", {"start": v(10.51, -1.87) * mm, "end": v(10.39, -1.86) * mm});
            skLineSegment(sketch, "E1761", {"start": v(10.39, -1.86) * mm, "end": v(10.27, -1.84) * mm});
            skLineSegment(sketch, "E1762", {"start": v(10.27, -1.84) * mm, "end": v(10.16, -1.8) * mm});
            skLineSegment(sketch, "E1763", {"start": v(10.16, -1.8) * mm, "end": v(10.05, -1.74) * mm});
            skLineSegment(sketch, "E1764", {"start": v(10.05, -1.74) * mm, "end": v(9.95, -1.68) * mm});
            skLineSegment(sketch, "E1765", {"start": v(9.95, -1.68) * mm, "end": v(9.85, -1.6) * mm});
            skLineSegment(sketch, "E1766", {"start": v(9.85, -1.6) * mm, "end": v(9.75, -1.49) * mm});
            skLineSegment(sketch, "E1767", {"start": v(9.75, -1.49) * mm, "end": v(9.66, -1.37) * mm});
            skLineSegment(sketch, "E1768", {"start": v(9.66, -1.37) * mm, "end": v(9.57, -1.25) * mm});
            skLineSegment(sketch, "E1769", {"start": v(9.57, -1.25) * mm, "end": v(9.5, -1.11) * mm});
            skLineSegment(sketch, "E1770", {"start": v(9.5, -1.11) * mm, "end": v(9.44, -0.97) * mm});
            skLineSegment(sketch, "E1771", {"start": v(9.44, -0.97) * mm, "end": v(9.38, -0.82) * mm});
            skLineSegment(sketch, "E1772", {"start": v(9.38, -0.82) * mm, "end": v(9.35, -0.67) * mm});
            skLineSegment(sketch, "E1773", {"start": v(9.35, -0.67) * mm, "end": v(9.32, -0.51) * mm});
            skLineSegment(sketch, "E1774", {"start": v(9.32, -0.51) * mm, "end": v(9.3, -0.34) * mm});
            skLineSegment(sketch, "E1775", {"start": v(9.3, -0.34) * mm, "end": v(9.3, -0.17) * mm});
            skLineSegment(sketch, "E1776", {"start": v(9.3, -0.17) * mm, "end": v(9.3, 0) * mm});
            skLineSegment(sketch, "E1777", {"start": v(9.3, 0) * mm, "end": v(9.32, 0.17) * mm});
            skLineSegment(sketch, "E1778", {"start": v(9.32, 0.17) * mm, "end": v(9.35, 0.33) * mm});
            skLineSegment(sketch, "E1779", {"start": v(9.35, 0.33) * mm, "end": v(9.38, 0.48) * mm});
            skLineSegment(sketch, "E1780", {"start": v(9.38, 0.48) * mm, "end": v(9.44, 0.63) * mm});
            skLineSegment(sketch, "E1781", {"start": v(9.44, 0.63) * mm, "end": v(9.5, 0.77) * mm});
            skLineSegment(sketch, "E1782", {"start": v(9.5, 0.77) * mm, "end": v(9.57, 0.9) * mm});
            skLineSegment(sketch, "E1783", {"start": v(9.57, 0.9) * mm, "end": v(9.66, 1.03) * mm});
            skLineSegment(sketch, "E1784", {"start": v(9.66, 1.03) * mm, "end": v(9.75, 1.15) * mm});
            skLineSegment(sketch, "E1785", {"start": v(9.75, 1.15) * mm, "end": v(9.85, 1.25) * mm});
            skLineSegment(sketch, "E1786", {"start": v(9.85, 1.25) * mm, "end": v(9.95, 1.33) * mm});
            skLineSegment(sketch, "E1787", {"start": v(9.95, 1.33) * mm, "end": v(10.05, 1.4) * mm});
            skLineSegment(sketch, "E1788", {"start": v(10.05, 1.4) * mm, "end": v(10.16, 1.45) * mm});
            skLineSegment(sketch, "E1789", {"start": v(10.16, 1.45) * mm, "end": v(10.27, 1.5) * mm});
            skLineSegment(sketch, "E1790", {"start": v(10.27, 1.5) * mm, "end": v(10.39, 1.51) * mm});
            skLineSegment(sketch, "E1791", {"start": v(10.39, 1.51) * mm, "end": v(10.51, 1.52) * mm});
            skLineSegment(sketch, "E1792", {"start": v(13.24, -1.64) * mm, "end": v(13.31, -1.64) * mm});
            skLineSegment(sketch, "E1793", {"start": v(13.31, -1.64) * mm, "end": v(13.38, -1.62) * mm});
            skLineSegment(sketch, "E1794", {"start": v(13.38, -1.62) * mm, "end": v(13.44, -1.6) * mm});
            skLineSegment(sketch, "E1795", {"start": v(13.44, -1.6) * mm, "end": v(13.5, -1.55) * mm});
            skLineSegment(sketch, "E1796", {"start": v(13.5, -1.55) * mm, "end": v(13.54, -1.5) * mm});
            skLineSegment(sketch, "E1797", {"start": v(13.54, -1.5) * mm, "end": v(13.6, -1.43) * mm});
            skLineSegment(sketch, "E1798", {"start": v(13.6, -1.43) * mm, "end": v(13.63, -1.35) * mm});
            skLineSegment(sketch, "E1799", {"start": v(13.63, -1.35) * mm, "end": v(13.67, -1.27) * mm});
            skLineSegment(sketch, "E1800", {"start": v(13.67, -1.27) * mm, "end": v(13.73, -1.05) * mm});
            skLineSegment(sketch, "E1801", {"start": v(13.73, -1.05) * mm, "end": v(13.78, -0.8) * mm});
            skLineSegment(sketch, "E1802", {"start": v(13.78, -0.8) * mm, "end": v(13.8, -0.5) * mm});
            skLineSegment(sketch, "E1803", {"start": v(13.8, -0.5) * mm, "end": v(13.82, -0.15) * mm});
            skLineSegment(sketch, "E1804", {"start": v(13.82, -0.15) * mm, "end": v(13.8, 0.2) * mm});
            skLineSegment(sketch, "E1805", {"start": v(13.8, 0.2) * mm, "end": v(13.78, 0.5) * mm});
            skLineSegment(sketch, "E1806", {"start": v(13.78, 0.5) * mm, "end": v(13.74, 0.76) * mm});
            skLineSegment(sketch, "E1807", {"start": v(13.74, 0.76) * mm, "end": v(13.68, 0.96) * mm});
            skLineSegment(sketch, "E1808", {"start": v(13.68, 0.96) * mm, "end": v(13.64, 1.05) * mm});
            skLineSegment(sketch, "E1809", {"start": v(13.64, 1.05) * mm, "end": v(13.6, 1.13) * mm});
            skLineSegment(sketch, "E1810", {"start": v(13.6, 1.13) * mm, "end": v(13.55, 1.19) * mm});
            skLineSegment(sketch, "E1811", {"start": v(13.55, 1.19) * mm, "end": v(13.5, 1.24) * mm});
            skLineSegment(sketch, "E1812", {"start": v(13.5, 1.24) * mm, "end": v(13.45, 1.28) * mm});
            skLineSegment(sketch, "E1813", {"start": v(13.45, 1.28) * mm, "end": v(13.39, 1.3) * mm});
            skLineSegment(sketch, "E1814", {"start": v(13.39, 1.3) * mm, "end": v(13.32, 1.33) * mm});
            skLineSegment(sketch, "E1815", {"start": v(13.32, 1.33) * mm, "end": v(13.26, 1.33) * mm});
            skLineSegment(sketch, "E1816", {"start": v(13.26, 1.33) * mm, "end": v(13.19, 1.33) * mm});
            skLineSegment(sketch, "E1817", {"start": v(13.19, 1.33) * mm, "end": v(13.13, 1.31) * mm});
            skLineSegment(sketch, "E1818", {"start": v(13.13, 1.31) * mm, "end": v(13.07, 1.29) * mm});
            skLineSegment(sketch, "E1819", {"start": v(13.07, 1.29) * mm, "end": v(13.02, 1.26) * mm});
            skLineSegment(sketch, "E1820", {"start": v(13.02, 1.26) * mm, "end": v(12.97, 1.21) * mm});
            skLineSegment(sketch, "E1821", {"start": v(12.97, 1.21) * mm, "end": v(12.93, 1.16) * mm});
            skLineSegment(sketch, "E1822", {"start": v(12.93, 1.16) * mm, "end": v(12.9, 1.1) * mm});
            skLineSegment(sketch, "E1823", {"start": v(12.9, 1.1) * mm, "end": v(12.87, 1.03) * mm});
            skLineSegment(sketch, "E1824", {"start": v(12.87, 1.03) * mm, "end": v(12.82, 0.84) * mm});
            skLineSegment(sketch, "E1825", {"start": v(12.82, 0.84) * mm, "end": v(12.78, 0.6) * mm});
            skLineSegment(sketch, "E1826", {"start": v(12.78, 0.6) * mm, "end": v(12.76, 0.28) * mm});
            skLineSegment(sketch, "E1827", {"start": v(12.76, 0.28) * mm, "end": v(12.75, -0.1) * mm});
            skLineSegment(sketch, "E1828", {"start": v(12.75, -0.1) * mm, "end": v(12.76, -0.49) * mm});
            skLineSegment(sketch, "E1829", {"start": v(12.76, -0.49) * mm, "end": v(12.78, -0.82) * mm});
            skLineSegment(sketch, "E1830", {"start": v(12.78, -0.82) * mm, "end": v(12.82, -1.1) * mm});
            skLineSegment(sketch, "E1831", {"start": v(12.82, -1.1) * mm, "end": v(12.86, -1.3) * mm});
            skLineSegment(sketch, "E1832", {"start": v(12.86, -1.3) * mm, "end": v(12.9, -1.38) * mm});
            skLineSegment(sketch, "E1833", {"start": v(12.9, -1.38) * mm, "end": v(12.93, -1.45) * mm});
            skLineSegment(sketch, "E1834", {"start": v(12.93, -1.45) * mm, "end": v(12.97, -1.5) * mm});
            skLineSegment(sketch, "E1835", {"start": v(12.97, -1.5) * mm, "end": v(13.01, -1.56) * mm});
            skLineSegment(sketch, "E1836", {"start": v(13.01, -1.56) * mm, "end": v(13.06, -1.6) * mm});
            skLineSegment(sketch, "E1837", {"start": v(13.06, -1.6) * mm, "end": v(13.12, -1.62) * mm});
            skLineSegment(sketch, "E1838", {"start": v(13.12, -1.62) * mm, "end": v(13.18, -1.64) * mm});
            skLineSegment(sketch, "E1839", {"start": v(13.18, -1.64) * mm, "end": v(13.24, -1.64) * mm});
            skLineSegment(sketch, "E1840", {"start": v(13.8, 2.3) * mm, "end": v(13.8, 2.41) * mm});
            skLineSegment(sketch, "E1841", {"start": v(13.8, 2.41) * mm, "end": v(13.79, 2.5) * mm});
            skLineSegment(sketch, "E1842", {"start": v(13.79, 2.5) * mm, "end": v(13.77, 2.56) * mm});
            skLineSegment(sketch, "E1843", {"start": v(13.77, 2.56) * mm, "end": v(13.74, 2.6) * mm});
            skLineSegment(sketch, "E1844", {"start": v(13.74, 2.6) * mm, "end": v(13.7, 2.63) * mm});
            skLineSegment(sketch, "E1845", {"start": v(13.7, 2.63) * mm, "end": v(13.65, 2.65) * mm});
            skLineSegment(sketch, "E1846", {"start": v(13.65, 2.65) * mm, "end": v(13.57, 2.66) * mm});
            skLineSegment(sketch, "E1847", {"start": v(13.57, 2.66) * mm, "end": v(13.47, 2.67) * mm});
            skLineSegment(sketch, "E1848", {"start": v(13.47, 2.67) * mm, "end": v(13.38, 2.67) * mm});
            skLineSegment(sketch, "E1849", {"start": v(13.38, 2.67) * mm, "end": v(13.38, 2.82) * mm});
            skLineSegment(sketch, "E1850", {"start": v(13.38, 2.82) * mm, "end": v(14.4, 2.82) * mm});
            skLineSegment(sketch, "E1851", {"start": v(14.4, 2.82) * mm, "end": v(14.4, -1.29) * mm});
            skLineSegment(sketch, "E1852", {"start": v(14.4, -1.29) * mm, "end": v(14.4, -1.4) * mm});
            skLineSegment(sketch, "E1853", {"start": v(14.4, -1.4) * mm, "end": v(14.4, -1.49) * mm});
            skLineSegment(sketch, "E1854", {"start": v(14.4, -1.49) * mm, "end": v(14.42, -1.55) * mm});
            skLineSegment(sketch, "E1855", {"start": v(14.42, -1.55) * mm, "end": v(14.45, -1.6) * mm});
            skLineSegment(sketch, "E1856", {"start": v(14.45, -1.6) * mm, "end": v(14.49, -1.62) * mm});
            skLineSegment(sketch, "E1857", {"start": v(14.49, -1.62) * mm, "end": v(14.54, -1.64) * mm});
            skLineSegment(sketch, "E1858", {"start": v(14.54, -1.64) * mm, "end": v(14.62, -1.65) * mm});
            skLineSegment(sketch, "E1859", {"start": v(14.62, -1.65) * mm, "end": v(14.7, -1.66) * mm});
            skLineSegment(sketch, "E1860", {"start": v(14.7, -1.66) * mm, "end": v(14.81, -1.66) * mm});
            skLineSegment(sketch, "E1861", {"start": v(14.81, -1.66) * mm, "end": v(14.81, -1.8) * mm});
            skLineSegment(sketch, "E1862", {"start": v(14.81, -1.8) * mm, "end": v(13.84, -1.8) * mm});
            skLineSegment(sketch, "E1863", {"start": v(13.84, -1.8) * mm, "end": v(13.84, -1.24) * mm});
            skLineSegment(sketch, "E1864", {"start": v(13.84, -1.24) * mm, "end": v(13.77, -1.39) * mm});
            skLineSegment(sketch, "E1865", {"start": v(13.77, -1.39) * mm, "end": v(13.7, -1.51) * mm});
            skLineSegment(sketch, "E1866", {"start": v(13.7, -1.51) * mm, "end": v(13.61, -1.62) * mm});
            skLineSegment(sketch, "E1867", {"start": v(13.61, -1.62) * mm, "end": v(13.52, -1.7) * mm});
            skLineSegment(sketch, "E1868", {"start": v(13.52, -1.7) * mm, "end": v(13.43, -1.77) * mm});
            skLineSegment(sketch, "E1869", {"start": v(13.43, -1.77) * mm, "end": v(13.32, -1.82) * mm});
            skLineSegment(sketch, "E1870", {"start": v(13.32, -1.82) * mm, "end": v(13.2, -1.85) * mm});
            skLineSegment(sketch, "E1871", {"start": v(13.2, -1.85) * mm, "end": v(13.07, -1.86) * mm});
            skLineSegment(sketch, "E1872", {"start": v(13.07, -1.86) * mm, "end": v(12.97, -1.85) * mm});
            skLineSegment(sketch, "E1873", {"start": v(12.97, -1.85) * mm, "end": v(12.87, -1.83) * mm});
            skLineSegment(sketch, "E1874", {"start": v(12.87, -1.83) * mm, "end": v(12.78, -1.8) * mm});
            skLineSegment(sketch, "E1875", {"start": v(12.78, -1.8) * mm, "end": v(12.7, -1.74) * mm});
            skLineSegment(sketch, "E1876", {"start": v(12.7, -1.74) * mm, "end": v(12.6, -1.68) * mm});
            skLineSegment(sketch, "E1877", {"start": v(12.6, -1.68) * mm, "end": v(12.53, -1.6) * mm});
            skLineSegment(sketch, "E1878", {"start": v(12.53, -1.6) * mm, "end": v(12.45, -1.5) * mm});
            skLineSegment(sketch, "E1879", {"start": v(12.45, -1.5) * mm, "end": v(12.38, -1.4) * mm});
            skLineSegment(sketch, "E1880", {"start": v(12.38, -1.4) * mm, "end": v(12.32, -1.27) * mm});
            skLineSegment(sketch, "E1881", {"start": v(12.32, -1.27) * mm, "end": v(12.26, -1.14) * mm});
            skLineSegment(sketch, "E1882", {"start": v(12.26, -1.14) * mm, "end": v(12.22, -1) * mm});
            skLineSegment(sketch, "E1883", {"start": v(12.22, -1) * mm, "end": v(12.18, -0.85) * mm});
            skLineSegment(sketch, "E1884", {"start": v(12.18, -0.85) * mm, "end": v(12.15, -0.7) * mm});
            skLineSegment(sketch, "E1885", {"start": v(12.15, -0.7) * mm, "end": v(12.13, -0.53) * mm});
            skLineSegment(sketch, "E1886", {"start": v(12.13, -0.53) * mm, "end": v(12.12, -0.35) * mm});
            skLineSegment(sketch, "E1887", {"start": v(12.12, -0.35) * mm, "end": v(12.11, -0.17) * mm});
            skLineSegment(sketch, "E1888", {"start": v(12.11, -0.17) * mm, "end": v(12.12, 0.02) * mm});
            skLineSegment(sketch, "E1889", {"start": v(12.12, 0.02) * mm, "end": v(12.13, 0.2) * mm});
            skLineSegment(sketch, "E1890", {"start": v(12.13, 0.2) * mm, "end": v(12.15, 0.36) * mm});
            skLineSegment(sketch, "E1891", {"start": v(12.15, 0.36) * mm, "end": v(12.19, 0.52) * mm});
            skLineSegment(sketch, "E1892", {"start": v(12.19, 0.52) * mm, "end": v(12.23, 0.67) * mm});
            skLineSegment(sketch, "E1893", {"start": v(12.23, 0.67) * mm, "end": v(12.28, 0.8) * mm});
            skLineSegment(sketch, "E1894", {"start": v(12.28, 0.8) * mm, "end": v(12.34, 0.94) * mm});
            skLineSegment(sketch, "E1895", {"start": v(12.34, 0.94) * mm, "end": v(12.4, 1.06) * mm});
            skLineSegment(sketch, "E1896", {"start": v(12.4, 1.06) * mm, "end": v(12.48, 1.17) * mm});
            skLineSegment(sketch, "E1897", {"start": v(12.48, 1.17) * mm, "end": v(12.57, 1.27) * mm});
            skLineSegment(sketch, "E1898", {"start": v(12.57, 1.27) * mm, "end": v(12.65, 1.35) * mm});
            skLineSegment(sketch, "E1899", {"start": v(12.65, 1.35) * mm, "end": v(12.75, 1.41) * mm});
            skLineSegment(sketch, "E1900", {"start": v(12.75, 1.41) * mm, "end": v(12.84, 1.46) * mm});
            skLineSegment(sketch, "E1901", {"start": v(12.84, 1.46) * mm, "end": v(12.95, 1.5) * mm});
            skLineSegment(sketch, "E1902", {"start": v(12.95, 1.5) * mm, "end": v(13.05, 1.52) * mm});
            skLineSegment(sketch, "E1903", {"start": v(13.05, 1.52) * mm, "end": v(13.17, 1.53) * mm});
            skLineSegment(sketch, "E1904", {"start": v(13.17, 1.53) * mm, "end": v(13.26, 1.52) * mm});
            skLineSegment(sketch, "E1905", {"start": v(13.26, 1.52) * mm, "end": v(13.35, 1.5) * mm});
            skLineSegment(sketch, "E1906", {"start": v(13.35, 1.5) * mm, "end": v(13.44, 1.47) * mm});
            skLineSegment(sketch, "E1907", {"start": v(13.44, 1.47) * mm, "end": v(13.52, 1.42) * mm});
            skLineSegment(sketch, "E1908", {"start": v(13.52, 1.42) * mm, "end": v(13.6, 1.36) * mm});
            skLineSegment(sketch, "E1909", {"start": v(13.6, 1.36) * mm, "end": v(13.67, 1.28) * mm});
            skLineSegment(sketch, "E1910", {"start": v(13.67, 1.28) * mm, "end": v(13.74, 1.2) * mm});
            skLineSegment(sketch, "E1911", {"start": v(13.74, 1.2) * mm, "end": v(13.8, 1.08) * mm});
            skLineSegment(sketch, "E1912", {"start": v(13.8, 1.08) * mm, "end": v(13.8, 2.3) * mm});
            skLineSegment(sketch, "E1913", {"start": v(3.55, -5.5) * mm, "end": v(5.75, -5.5) * mm});
            skLineSegment(sketch, "E1914", {"start": v(5.75, -5.5) * mm, "end": v(4.66, -3.2) * mm});
            skLineSegment(sketch, "E1915", {"start": v(4.66, -3.2) * mm, "end": v(3.55, -5.5) * mm});
            skLineSegment(sketch, "E1916", {"start": v(1.59, -7.14) * mm, "end": v(1.59, -6.99) * mm});
            skLineSegment(sketch, "E1917", {"start": v(1.59, -6.99) * mm, "end": v(1.61, -6.99) * mm});
            skLineSegment(sketch, "E1918", {"start": v(1.61, -6.99) * mm, "end": v(1.83, -6.98) * mm});
            skLineSegment(sketch, "E1919", {"start": v(1.83, -6.98) * mm, "end": v(2.03, -6.94) * mm});
            skLineSegment(sketch, "E1920", {"start": v(2.03, -6.94) * mm, "end": v(2.2, -6.88) * mm});
            skLineSegment(sketch, "E1921", {"start": v(2.2, -6.88) * mm, "end": v(2.37, -6.8) * mm});
            skLineSegment(sketch, "E1922", {"start": v(2.37, -6.8) * mm, "end": v(2.52, -6.68) * mm});
            skLineSegment(sketch, "E1923", {"start": v(2.52, -6.68) * mm, "end": v(2.65, -6.55) * mm});
            skLineSegment(sketch, "E1924", {"start": v(2.65, -6.55) * mm, "end": v(2.77, -6.38) * mm});
            skLineSegment(sketch, "E1925", {"start": v(2.77, -6.38) * mm, "end": v(2.88, -6.19) * mm});
            skLineSegment(sketch, "E1926", {"start": v(2.88, -6.19) * mm, "end": v(4.65, -2.53) * mm});
            skLineSegment(sketch, "E1927", {"start": v(4.65, -2.53) * mm, "end": v(5.36, -2.53) * mm});
            skLineSegment(sketch, "E1928", {"start": v(5.36, -2.53) * mm, "end": v(7.24, -6.34) * mm});
            skLineSegment(sketch, "E1929", {"start": v(7.24, -6.34) * mm, "end": v(7.34, -6.52) * mm});
            skLineSegment(sketch, "E1930", {"start": v(7.34, -6.52) * mm, "end": v(7.43, -6.66) * mm});
            skLineSegment(sketch, "E1931", {"start": v(7.43, -6.66) * mm, "end": v(7.54, -6.77) * mm});
            skLineSegment(sketch, "E1932", {"start": v(7.54, -6.77) * mm, "end": v(7.64, -6.85) * mm});
            skLineSegment(sketch, "E1933", {"start": v(7.64, -6.85) * mm, "end": v(7.77, -6.9) * mm});
            skLineSegment(sketch, "E1934", {"start": v(7.77, -6.9) * mm, "end": v(7.92, -6.94) * mm});
            skLineSegment(sketch, "E1935", {"start": v(7.92, -6.94) * mm, "end": v(8.1, -6.97) * mm});
            skLineSegment(sketch, "E1936", {"start": v(8.1, -6.97) * mm, "end": v(8.3, -6.99) * mm});
            skLineSegment(sketch, "E1937", {"start": v(8.3, -6.99) * mm, "end": v(8.3, -7.14) * mm});
            skLineSegment(sketch, "E1938", {"start": v(8.3, -7.14) * mm, "end": v(5.52, -7.14) * mm});
            skLineSegment(sketch, "E1939", {"start": v(5.52, -7.14) * mm, "end": v(5.52, -6.99) * mm});
            skLineSegment(sketch, "E1940", {"start": v(5.52, -6.99) * mm, "end": v(5.7, -6.98) * mm});
            skLineSegment(sketch, "E1941", {"start": v(5.7, -6.98) * mm, "end": v(5.85, -6.97) * mm});
            skLineSegment(sketch, "E1942", {"start": v(5.85, -6.97) * mm, "end": v(5.98, -6.95) * mm});
            skLineSegment(sketch, "E1943", {"start": v(5.98, -6.95) * mm, "end": v(6.09, -6.92) * mm});
            skLineSegment(sketch, "E1944", {"start": v(6.09, -6.92) * mm, "end": v(6.17, -6.88) * mm});
            skLineSegment(sketch, "E1945", {"start": v(6.17, -6.88) * mm, "end": v(6.23, -6.83) * mm});
            skLineSegment(sketch, "E1946", {"start": v(6.23, -6.83) * mm, "end": v(6.26, -6.78) * mm});
            skLineSegment(sketch, "E1947", {"start": v(6.26, -6.78) * mm, "end": v(6.27, -6.71) * mm});
            skLineSegment(sketch, "E1948", {"start": v(6.27, -6.71) * mm, "end": v(6.27, -6.65) * mm});
            skLineSegment(sketch, "E1949", {"start": v(6.27, -6.65) * mm, "end": v(6.25, -6.58) * mm});
            skLineSegment(sketch, "E1950", {"start": v(6.25, -6.58) * mm, "end": v(6.18, -6.41) * mm});
            skLineSegment(sketch, "E1951", {"start": v(6.18, -6.41) * mm, "end": v(5.86, -5.73) * mm});
            skLineSegment(sketch, "E1952", {"start": v(5.86, -5.73) * mm, "end": v(3.43, -5.73) * mm});
            skLineSegment(sketch, "E1953", {"start": v(3.43, -5.73) * mm, "end": v(3.12, -6.38) * mm});
            skLineSegment(sketch, "E1954", {"start": v(3.12, -6.38) * mm, "end": v(3.07, -6.52) * mm});
            skLineSegment(sketch, "E1955", {"start": v(3.07, -6.52) * mm, "end": v(3.05, -6.65) * mm});
            skLineSegment(sketch, "E1956", {"start": v(3.05, -6.65) * mm, "end": v(3.06, -6.73) * mm});
            skLineSegment(sketch, "E1957", {"start": v(3.06, -6.73) * mm, "end": v(3.1, -6.8) * mm});
            skLineSegment(sketch, "E1958", {"start": v(3.1, -6.8) * mm, "end": v(3.16, -6.86) * mm});
            skLineSegment(sketch, "E1959", {"start": v(3.16, -6.86) * mm, "end": v(3.24, -6.9) * mm});
            skLineSegment(sketch, "E1960", {"start": v(3.24, -6.9) * mm, "end": v(3.35, -6.94) * mm});
            skLineSegment(sketch, "E1961", {"start": v(3.35, -6.94) * mm, "end": v(3.5, -6.96) * mm});
            skLineSegment(sketch, "E1962", {"start": v(3.5, -6.96) * mm, "end": v(3.67, -6.98) * mm});
            skLineSegment(sketch, "E1963", {"start": v(3.67, -6.98) * mm, "end": v(3.87, -6.99) * mm});
            skLineSegment(sketch, "E1964", {"start": v(3.87, -6.99) * mm, "end": v(3.87, -7.14) * mm});
            skLineSegment(sketch, "E1965", {"start": v(3.87, -7.14) * mm, "end": v(1.59, -7.14) * mm});
            skLineSegment(sketch, "E1966", {"start": v(8.5, -7.14) * mm, "end": v(8.5, -6.99) * mm});
            skLineSegment(sketch, "E1967", {"start": v(8.5, -6.99) * mm, "end": v(8.68, -6.99) * mm});
            skLineSegment(sketch, "E1968", {"start": v(8.68, -6.99) * mm, "end": v(8.84, -6.99) * mm});
            skLineSegment(sketch, "E1969", {"start": v(8.84, -6.99) * mm, "end": v(8.97, -6.97) * mm});
            skLineSegment(sketch, "E1970", {"start": v(8.97, -6.97) * mm, "end": v(9.07, -6.95) * mm});
            skLineSegment(sketch, "E1971", {"start": v(9.07, -6.95) * mm, "end": v(9.13, -6.93) * mm});
            skLineSegment(sketch, "E1972", {"start": v(9.13, -6.93) * mm, "end": v(9.18, -6.88) * mm});
            skLineSegment(sketch, "E1973", {"start": v(9.18, -6.88) * mm, "end": v(9.2, -6.82) * mm});
            skLineSegment(sketch, "E1974", {"start": v(9.2, -6.82) * mm, "end": v(9.23, -6.73) * mm});
            skLineSegment(sketch, "E1975", {"start": v(9.23, -6.73) * mm, "end": v(9.23, -6.62) * mm});
            skLineSegment(sketch, "E1976", {"start": v(9.23, -6.62) * mm, "end": v(9.23, -4.4) * mm});
            skLineSegment(sketch, "E1977", {"start": v(9.23, -4.4) * mm, "end": v(9.23, -4.3) * mm});
            skLineSegment(sketch, "E1978", {"start": v(9.23, -4.3) * mm, "end": v(9.2, -4.2) * mm});
            skLineSegment(sketch, "E1979", {"start": v(9.2, -4.2) * mm, "end": v(9.18, -4.14) * mm});
            skLineSegment(sketch, "E1980", {"start": v(9.18, -4.14) * mm, "end": v(9.13, -4.1) * mm});
            skLineSegment(sketch, "E1981", {"start": v(9.13, -4.1) * mm, "end": v(9.07, -4.07) * mm});
            skLineSegment(sketch, "E1982", {"start": v(9.07, -4.07) * mm, "end": v(8.97, -4.05) * mm});
            skLineSegment(sketch, "E1983", {"start": v(8.97, -4.05) * mm, "end": v(8.84, -4.04) * mm});
            skLineSegment(sketch, "E1984", {"start": v(8.84, -4.04) * mm, "end": v(8.68, -4.03) * mm});
            skLineSegment(sketch, "E1985", {"start": v(8.68, -4.03) * mm, "end": v(8.5, -4.03) * mm});
            skLineSegment(sketch, "E1986", {"start": v(8.5, -4.03) * mm, "end": v(8.5, -3.9) * mm});
            skLineSegment(sketch, "E1987", {"start": v(8.5, -3.9) * mm, "end": v(9.42, -3.88) * mm});
            skLineSegment(sketch, "E1988", {"start": v(9.42, -3.88) * mm, "end": v(9.81, -3.87) * mm});
            skLineSegment(sketch, "E1989", {"start": v(9.81, -3.87) * mm, "end": v(10.18, -3.84) * mm});
            skLineSegment(sketch, "E1990", {"start": v(10.18, -3.84) * mm, "end": v(10.18, -4.45) * mm});
            skLineSegment(sketch, "E1991", {"start": v(10.18, -4.45) * mm, "end": v(10.29, -4.32) * mm});
            skLineSegment(sketch, "E1992", {"start": v(10.29, -4.32) * mm, "end": v(10.42, -4.2) * mm});
            skLineSegment(sketch, "E1993", {"start": v(10.42, -4.2) * mm, "end": v(10.56, -4.09) * mm});
            skLineSegment(sketch, "E1994", {"start": v(10.56, -4.09) * mm, "end": v(10.73, -4) * mm});
            skLineSegment(sketch, "E1995", {"start": v(10.73, -4) * mm, "end": v(10.9, -3.92) * mm});
            skLineSegment(sketch, "E1996", {"start": v(10.9, -3.92) * mm, "end": v(11.08, -3.87) * mm});
            skLineSegment(sketch, "E1997", {"start": v(11.08, -3.87) * mm, "end": v(11.27, -3.84) * mm});
            skLineSegment(sketch, "E1998", {"start": v(11.27, -3.84) * mm, "end": v(11.47, -3.83) * mm});
            skLineSegment(sketch, "E1999", {"start": v(11.47, -3.83) * mm, "end": v(11.66, -3.84) * mm});
            skLineSegment(sketch, "E2000", {"start": v(11.66, -3.84) * mm, "end": v(11.83, -3.87) * mm});
            skLineSegment(sketch, "E2001", {"start": v(11.83, -3.87) * mm, "end": v(11.99, -3.91) * mm});
            skLineSegment(sketch, "E2002", {"start": v(11.99, -3.91) * mm, "end": v(12.13, -3.98) * mm});
            skLineSegment(sketch, "E2003", {"start": v(12.13, -3.98) * mm, "end": v(12.25, -4.05) * mm});
            skLineSegment(sketch, "E2004", {"start": v(12.25, -4.05) * mm, "end": v(12.33, -4.14) * mm});
            skLineSegment(sketch, "E2005", {"start": v(12.33, -4.14) * mm, "end": v(12.36, -4.18) * mm});
            skLineSegment(sketch, "E2006", {"start": v(12.36, -4.18) * mm, "end": v(12.38, -4.23) * mm});
            skLineSegment(sketch, "E2007", {"start": v(12.38, -4.23) * mm, "end": v(12.4, -4.28) * mm});
            skLineSegment(sketch, "E2008", {"start": v(12.4, -4.28) * mm, "end": v(12.4, -4.33) * mm});
            skLineSegment(sketch, "E2009", {"start": v(12.4, -4.33) * mm, "end": v(12.39, -4.42) * mm});
            skLineSegment(sketch, "E2010", {"start": v(12.39, -4.42) * mm, "end": v(12.34, -4.5) * mm});
            skLineSegment(sketch, "E2011", {"start": v(12.34, -4.5) * mm, "end": v(12.28, -4.58) * mm});
            skLineSegment(sketch, "E2012", {"start": v(12.28, -4.58) * mm, "end": v(12.18, -4.64) * mm});
            skLineSegment(sketch, "E2013", {"start": v(12.18, -4.64) * mm, "end": v(12.07, -4.7) * mm});
            skLineSegment(sketch, "E2014", {"start": v(12.07, -4.7) * mm, "end": v(11.94, -4.74) * mm});
            skLineSegment(sketch, "E2015", {"start": v(11.94, -4.74) * mm, "end": v(11.8, -4.76) * mm});
            skLineSegment(sketch, "E2016", {"start": v(11.8, -4.76) * mm, "end": v(11.65, -4.77) * mm});
            skLineSegment(sketch, "E2017", {"start": v(11.65, -4.77) * mm, "end": v(11.52, -4.77) * mm});
            skLineSegment(sketch, "E2018", {"start": v(11.52, -4.77) * mm, "end": v(11.4, -4.75) * mm});
            skLineSegment(sketch, "E2019", {"start": v(11.4, -4.75) * mm, "end": v(11.3, -4.72) * mm});
            skLineSegment(sketch, "E2020", {"start": v(11.3, -4.72) * mm, "end": v(11.2, -4.68) * mm});
            skLineSegment(sketch, "E2021", {"start": v(11.2, -4.68) * mm, "end": v(11.13, -4.63) * mm});
            skLineSegment(sketch, "E2022", {"start": v(11.13, -4.63) * mm, "end": v(11.08, -4.57) * mm});
            skLineSegment(sketch, "E2023", {"start": v(11.08, -4.57) * mm, "end": v(11.04, -4.51) * mm});
            skLineSegment(sketch, "E2024", {"start": v(11.04, -4.51) * mm, "end": v(11.03, -4.45) * mm});
            skLineSegment(sketch, "E2025", {"start": v(11.03, -4.45) * mm, "end": v(11.04, -4.4) * mm});
            skLineSegment(sketch, "E2026", {"start": v(11.04, -4.4) * mm, "end": v(11.08, -4.34) * mm});
            skLineSegment(sketch, "E2027", {"start": v(11.08, -4.34) * mm, "end": v(11.14, -4.29) * mm});
            skLineSegment(sketch, "E2028", {"start": v(11.14, -4.29) * mm, "end": v(11.22, -4.23) * mm});
            skLineSegment(sketch, "E2029", {"start": v(11.22, -4.23) * mm, "end": v(11.36, -4.15) * mm});
            skLineSegment(sketch, "E2030", {"start": v(11.36, -4.15) * mm, "end": v(11.4, -4.12) * mm});
            skLineSegment(sketch, "E2031", {"start": v(11.4, -4.12) * mm, "end": v(11.4, -4.1) * mm});
            skLineSegment(sketch, "E2032", {"start": v(11.4, -4.1) * mm, "end": v(11.4, -4.06) * mm});
            skLineSegment(sketch, "E2033", {"start": v(11.4, -4.06) * mm, "end": v(11.36, -4.04) * mm});
            skLineSegment(sketch, "E2034", {"start": v(11.36, -4.04) * mm, "end": v(11.31, -4.02) * mm});
            skLineSegment(sketch, "E2035", {"start": v(11.31, -4.02) * mm, "end": v(11.24, -4.02) * mm});
            skLineSegment(sketch, "E2036", {"start": v(11.24, -4.02) * mm, "end": v(11.14, -4.03) * mm});
            skLineSegment(sketch, "E2037", {"start": v(11.14, -4.03) * mm, "end": v(11.05, -4.04) * mm});
            skLineSegment(sketch, "E2038", {"start": v(11.05, -4.04) * mm, "end": v(10.95, -4.07) * mm});
            skLineSegment(sketch, "E2039", {"start": v(10.95, -4.07) * mm, "end": v(10.87, -4.1) * mm});
            skLineSegment(sketch, "E2040", {"start": v(10.87, -4.1) * mm, "end": v(10.78, -4.15) * mm});
            skLineSegment(sketch, "E2041", {"start": v(10.78, -4.15) * mm, "end": v(10.7, -4.2) * mm});
            skLineSegment(sketch, "E2042", {"start": v(10.7, -4.2) * mm, "end": v(10.62, -4.27) * mm});
            skLineSegment(sketch, "E2043", {"start": v(10.62, -4.27) * mm, "end": v(10.54, -4.34) * mm});
            skLineSegment(sketch, "E2044", {"start": v(10.54, -4.34) * mm, "end": v(10.47, -4.43) * mm});
            skLineSegment(sketch, "E2045", {"start": v(10.47, -4.43) * mm, "end": v(10.41, -4.52) * mm});
            skLineSegment(sketch, "E2046", {"start": v(10.41, -4.52) * mm, "end": v(10.36, -4.61) * mm});
            skLineSegment(sketch, "E2047", {"start": v(10.36, -4.61) * mm, "end": v(10.32, -4.72) * mm});
            skLineSegment(sketch, "E2048", {"start": v(10.32, -4.72) * mm, "end": v(10.29, -4.82) * mm});
            skLineSegment(sketch, "E2049", {"start": v(10.29, -4.82) * mm, "end": v(10.26, -4.94) * mm});
            skLineSegment(sketch, "E2050", {"start": v(10.26, -4.94) * mm, "end": v(10.25, -5.06) * mm});
            skLineSegment(sketch, "E2051", {"start": v(10.25, -5.06) * mm, "end": v(10.24, -5.18) * mm});
            skLineSegment(sketch, "E2052", {"start": v(10.24, -5.18) * mm, "end": v(10.24, -6.62) * mm});
            skLineSegment(sketch, "E2053", {"start": v(10.24, -6.62) * mm, "end": v(10.25, -6.73) * mm});
            skLineSegment(sketch, "E2054", {"start": v(10.25, -6.73) * mm, "end": v(10.27, -6.82) * mm});
            skLineSegment(sketch, "E2055", {"start": v(10.27, -6.82) * mm, "end": v(10.3, -6.88) * mm});
            skLineSegment(sketch, "E2056", {"start": v(10.3, -6.88) * mm, "end": v(10.35, -6.93) * mm});
            skLineSegment(sketch, "E2057", {"start": v(10.35, -6.93) * mm, "end": v(10.42, -6.95) * mm});
            skLineSegment(sketch, "E2058", {"start": v(10.42, -6.95) * mm, "end": v(10.51, -6.97) * mm});
            skLineSegment(sketch, "E2059", {"start": v(10.51, -6.97) * mm, "end": v(10.64, -6.99) * mm});
            skLineSegment(sketch, "E2060", {"start": v(10.64, -6.99) * mm, "end": v(10.8, -6.99) * mm});
            skLineSegment(sketch, "E2061", {"start": v(10.8, -6.99) * mm, "end": v(11.08, -6.99) * mm});
            skLineSegment(sketch, "E2062", {"start": v(11.08, -6.99) * mm, "end": v(11.08, -7.14) * mm});
            skLineSegment(sketch, "E2063", {"start": v(11.08, -7.14) * mm, "end": v(8.5, -7.14) * mm});
            skLineSegment(sketch, "E2064", {"start": v(13.3, -4.14) * mm, "end": v(12.6, -4.14) * mm});
            skLineSegment(sketch, "E2065", {"start": v(12.6, -4.14) * mm, "end": v(12.6, -3.9) * mm});
            skLineSegment(sketch, "E2066", {"start": v(12.6, -3.9) * mm, "end": v(12.75, -3.88) * mm});
            skLineSegment(sketch, "E2067", {"start": v(12.75, -3.88) * mm, "end": v(12.9, -3.86) * mm});
            skLineSegment(sketch, "E2068", {"start": v(12.9, -3.86) * mm, "end": v(13.04, -3.83) * mm});
            skLineSegment(sketch, "E2069", {"start": v(13.04, -3.83) * mm, "end": v(13.16, -3.79) * mm});
            skLineSegment(sketch, "E2070", {"start": v(13.16, -3.79) * mm, "end": v(13.28, -3.74) * mm});
            skLineSegment(sketch, "E2071", {"start": v(13.28, -3.74) * mm, "end": v(13.4, -3.68) * mm});
            skLineSegment(sketch, "E2072", {"start": v(13.4, -3.68) * mm, "end": v(13.5, -3.62) * mm});
            skLineSegment(sketch, "E2073", {"start": v(13.5, -3.62) * mm, "end": v(13.59, -3.54) * mm});
            skLineSegment(sketch, "E2074", {"start": v(13.59, -3.54) * mm, "end": v(13.67, -3.46) * mm});
            skLineSegment(sketch, "E2075", {"start": v(13.67, -3.46) * mm, "end": v(13.74, -3.37) * mm});
            skLineSegment(sketch, "E2076", {"start": v(13.74, -3.37) * mm, "end": v(13.81, -3.27) * mm});
            skLineSegment(sketch, "E2077", {"start": v(13.81, -3.27) * mm, "end": v(13.87, -3.16) * mm});
            skLineSegment(sketch, "E2078", {"start": v(13.87, -3.16) * mm, "end": v(13.92, -3.05) * mm});
            skLineSegment(sketch, "E2079", {"start": v(13.92, -3.05) * mm, "end": v(13.96, -2.92) * mm});
            skLineSegment(sketch, "E2080", {"start": v(13.96, -2.92) * mm, "end": v(14, -2.78) * mm});
            skLineSegment(sketch, "E2081", {"start": v(14, -2.78) * mm, "end": v(14.02, -2.64) * mm});
            skLineSegment(sketch, "E2082", {"start": v(14.02, -2.64) * mm, "end": v(14.32, -2.64) * mm});
            skLineSegment(sketch, "E2083", {"start": v(14.32, -2.64) * mm, "end": v(14.32, -3.9) * mm});
            skLineSegment(sketch, "E2084", {"start": v(14.32, -3.9) * mm, "end": v(15.38, -3.9) * mm});
            skLineSegment(sketch, "E2085", {"start": v(15.38, -3.9) * mm, "end": v(15.38, -4.14) * mm});
            skLineSegment(sketch, "E2086", {"start": v(15.38, -4.14) * mm, "end": v(14.32, -4.14) * mm});
            skLineSegment(sketch, "E2087", {"start": v(14.32, -4.14) * mm, "end": v(14.32, -6.4) * mm});
            skLineSegment(sketch, "E2088", {"start": v(14.32, -6.4) * mm, "end": v(14.33, -6.52) * mm});
            skLineSegment(sketch, "E2089", {"start": v(14.33, -6.52) * mm, "end": v(14.35, -6.63) * mm});
            skLineSegment(sketch, "E2090", {"start": v(14.35, -6.63) * mm, "end": v(14.37, -6.72) * mm});
            skLineSegment(sketch, "E2091", {"start": v(14.37, -6.72) * mm, "end": v(14.41, -6.8) * mm});
            skLineSegment(sketch, "E2092", {"start": v(14.41, -6.8) * mm, "end": v(14.47, -6.84) * mm});
            skLineSegment(sketch, "E2093", {"start": v(14.47, -6.84) * mm, "end": v(14.54, -6.88) * mm});
            skLineSegment(sketch, "E2094", {"start": v(14.54, -6.88) * mm, "end": v(14.62, -6.9) * mm});
            skLineSegment(sketch, "E2095", {"start": v(14.62, -6.9) * mm, "end": v(14.72, -6.9) * mm});
            skLineSegment(sketch, "E2096", {"start": v(14.72, -6.9) * mm, "end": v(14.83, -6.9) * mm});
            skLineSegment(sketch, "E2097", {"start": v(14.83, -6.9) * mm, "end": v(14.92, -6.87) * mm});
            skLineSegment(sketch, "E2098", {"start": v(14.92, -6.87) * mm, "end": v(15, -6.83) * mm});
            skLineSegment(sketch, "E2099", {"start": v(15, -6.83) * mm, "end": v(15.06, -6.76) * mm});
            skLineSegment(sketch, "E2100", {"start": v(15.06, -6.76) * mm, "end": v(15.1, -6.68) * mm});
            skLineSegment(sketch, "E2101", {"start": v(15.1, -6.68) * mm, "end": v(15.14, -6.57) * mm});
            skLineSegment(sketch, "E2102", {"start": v(15.14, -6.57) * mm, "end": v(15.16, -6.43) * mm});
            skLineSegment(sketch, "E2103", {"start": v(15.16, -6.43) * mm, "end": v(15.17, -6.27) * mm});
            skLineSegment(sketch, "E2104", {"start": v(15.17, -6.27) * mm, "end": v(15.17, -6.21) * mm});
            skLineSegment(sketch, "E2105", {"start": v(15.17, -6.21) * mm, "end": v(15.45, -6.21) * mm});
            skLineSegment(sketch, "E2106", {"start": v(15.45, -6.21) * mm, "end": v(15.45, -6.35) * mm});
            skLineSegment(sketch, "E2107", {"start": v(15.45, -6.35) * mm, "end": v(15.45, -6.45) * mm});
            skLineSegment(sketch, "E2108", {"start": v(15.45, -6.45) * mm, "end": v(15.43, -6.55) * mm});
            skLineSegment(sketch, "E2109", {"start": v(15.43, -6.55) * mm, "end": v(15.41, -6.64) * mm});
            skLineSegment(sketch, "E2110", {"start": v(15.41, -6.64) * mm, "end": v(15.38, -6.72) * mm});
            skLineSegment(sketch, "E2111", {"start": v(15.38, -6.72) * mm, "end": v(15.34, -6.8) * mm});
            skLineSegment(sketch, "E2112", {"start": v(15.34, -6.8) * mm, "end": v(15.3, -6.87) * mm});
            skLineSegment(sketch, "E2113", {"start": v(15.3, -6.87) * mm, "end": v(15.24, -6.94) * mm});
            skLineSegment(sketch, "E2114", {"start": v(15.24, -6.94) * mm, "end": v(15.17, -7) * mm});
            skLineSegment(sketch, "E2115", {"start": v(15.17, -7) * mm, "end": v(15.1, -7.05) * mm});
            skLineSegment(sketch, "E2116", {"start": v(15.1, -7.05) * mm, "end": v(15.01, -7.1) * mm});
            skLineSegment(sketch, "E2117", {"start": v(15.01, -7.1) * mm, "end": v(14.92, -7.13) * mm});
            skLineSegment(sketch, "E2118", {"start": v(14.92, -7.13) * mm, "end": v(14.82, -7.16) * mm});
            skLineSegment(sketch, "E2119", {"start": v(14.82, -7.16) * mm, "end": v(14.71, -7.19) * mm});
            skLineSegment(sketch, "E2120", {"start": v(14.71, -7.19) * mm, "end": v(14.6, -7.2) * mm});
            skLineSegment(sketch, "E2121", {"start": v(14.6, -7.2) * mm, "end": v(14.34, -7.22) * mm});
            skLineSegment(sketch, "E2122", {"start": v(14.34, -7.22) * mm, "end": v(14.21, -7.22) * mm});
            skLineSegment(sketch, "E2123", {"start": v(14.21, -7.22) * mm, "end": v(14.09, -7.2) * mm});
            skLineSegment(sketch, "E2124", {"start": v(14.09, -7.2) * mm, "end": v(13.97, -7.19) * mm});
            skLineSegment(sketch, "E2125", {"start": v(13.97, -7.19) * mm, "end": v(13.87, -7.16) * mm});
            skLineSegment(sketch, "E2126", {"start": v(13.87, -7.16) * mm, "end": v(13.77, -7.13) * mm});
            skLineSegment(sketch, "E2127", {"start": v(13.77, -7.13) * mm, "end": v(13.69, -7.09) * mm});
            skLineSegment(sketch, "E2128", {"start": v(13.69, -7.09) * mm, "end": v(13.61, -7.04) * mm});
            skLineSegment(sketch, "E2129", {"start": v(13.61, -7.04) * mm, "end": v(13.55, -6.98) * mm});
            skLineSegment(sketch, "E2130", {"start": v(13.55, -6.98) * mm, "end": v(13.5, -6.92) * mm});
            skLineSegment(sketch, "E2131", {"start": v(13.5, -6.92) * mm, "end": v(13.44, -6.84) * mm});
            skLineSegment(sketch, "E2132", {"start": v(13.44, -6.84) * mm, "end": v(13.4, -6.75) * mm});
            skLineSegment(sketch, "E2133", {"start": v(13.4, -6.75) * mm, "end": v(13.37, -6.65) * mm});
            skLineSegment(sketch, "E2134", {"start": v(13.37, -6.65) * mm, "end": v(13.34, -6.54) * mm});
            skLineSegment(sketch, "E2135", {"start": v(13.34, -6.54) * mm, "end": v(13.32, -6.41) * mm});
            skLineSegment(sketch, "E2136", {"start": v(13.32, -6.41) * mm, "end": v(13.31, -6.28) * mm});
            skLineSegment(sketch, "E2137", {"start": v(13.31, -6.28) * mm, "end": v(13.3, -6.13) * mm});
            skLineSegment(sketch, "E2138", {"start": v(13.3, -6.13) * mm, "end": v(13.3, -4.14) * mm});
            skLineSegment(sketch, "E2139", {"start": v(-2.58, -5.27) * mm, "end": v(-2.6, -5.63) * mm});
            skLineSegment(sketch, "E2140", {"start": v(-2.6, -5.63) * mm, "end": v(-2.61, -5.97) * mm});
            skLineSegment(sketch, "E2141", {"start": v(-2.61, -5.97) * mm, "end": v(-2.6, -6.3) * mm});
            skLineSegment(sketch, "E2142", {"start": v(-2.6, -6.3) * mm, "end": v(-2.57, -6.6) * mm});
            skLineSegment(sketch, "E2143", {"start": v(-2.57, -6.6) * mm, "end": v(-2.55, -6.74) * mm});
            skLineSegment(sketch, "E2144", {"start": v(-2.55, -6.74) * mm, "end": v(-2.52, -6.86) * mm});
            skLineSegment(sketch, "E2145", {"start": v(-2.52, -6.86) * mm, "end": v(-2.48, -6.96) * mm});
            skLineSegment(sketch, "E2146", {"start": v(-2.48, -6.96) * mm, "end": v(-2.44, -7.05) * mm});
            skLineSegment(sketch, "E2147", {"start": v(-2.44, -7.05) * mm, "end": v(-2.38, -7.12) * mm});
            skLineSegment(sketch, "E2148", {"start": v(-2.38, -7.12) * mm, "end": v(-2.32, -7.17) * mm});
            skLineSegment(sketch, "E2149", {"start": v(-2.32, -7.17) * mm, "end": v(-2.25, -7.2) * mm});
            skLineSegment(sketch, "E2150", {"start": v(-2.25, -7.2) * mm, "end": v(-2.17, -7.22) * mm});
            skLineSegment(sketch, "E2151", {"start": v(-2.17, -7.22) * mm, "end": v(-2.1, -7.2) * mm});
            skLineSegment(sketch, "E2152", {"start": v(-2.1, -7.2) * mm, "end": v(-2.02, -7.17) * mm});
            skLineSegment(sketch, "E2153", {"start": v(-2.02, -7.17) * mm, "end": v(-1.95, -7.12) * mm});
            skLineSegment(sketch, "E2154", {"start": v(-1.95, -7.12) * mm, "end": v(-1.89, -7.05) * mm});
            skLineSegment(sketch, "E2155", {"start": v(-1.89, -7.05) * mm, "end": v(-1.82, -6.97) * mm});
            skLineSegment(sketch, "E2156", {"start": v(-1.82, -6.97) * mm, "end": v(-1.76, -6.87) * mm});
            skLineSegment(sketch, "E2157", {"start": v(-1.76, -6.87) * mm, "end": v(-1.7, -6.75) * mm});
            skLineSegment(sketch, "E2158", {"start": v(-1.7, -6.75) * mm, "end": v(-1.65, -6.61) * mm});
            skLineSegment(sketch, "E2159", {"start": v(-1.65, -6.61) * mm, "end": v(-1.55, -6.35) * mm});
            skLineSegment(sketch, "E2160", {"start": v(-1.55, -6.35) * mm, "end": v(-1.47, -6.06) * mm});
            skLineSegment(sketch, "E2161", {"start": v(-1.47, -6.06) * mm, "end": v(-1.39, -5.76) * mm});
            skLineSegment(sketch, "E2162", {"start": v(-1.39, -5.76) * mm, "end": v(-1.32, -5.45) * mm});
            skLineSegment(sketch, "E2163", {"start": v(-1.32, -5.45) * mm, "end": v(-1.32, -5.68) * mm});
            skLineSegment(sketch, "E2164", {"start": v(-1.32, -5.68) * mm, "end": v(-1.3, -6.04) * mm});
            skLineSegment(sketch, "E2165", {"start": v(-1.3, -6.04) * mm, "end": v(-1.27, -6.36) * mm});
            skLineSegment(sketch, "E2166", {"start": v(-1.27, -6.36) * mm, "end": v(-1.22, -6.63) * mm});
            skLineSegment(sketch, "E2167", {"start": v(-1.22, -6.63) * mm, "end": v(-1.18, -6.75) * mm});
            skLineSegment(sketch, "E2168", {"start": v(-1.18, -6.75) * mm, "end": v(-1.14, -6.85) * mm});
            skLineSegment(sketch, "E2169", {"start": v(-1.14, -6.85) * mm, "end": v(-1.05, -7.03) * mm});
            skLineSegment(sketch, "E2170", {"start": v(-1.05, -7.03) * mm, "end": v(-1, -7.1) * mm});
            skLineSegment(sketch, "E2171", {"start": v(-1, -7.1) * mm, "end": v(-0.95, -7.15) * mm});
            skLineSegment(sketch, "E2172", {"start": v(-0.95, -7.15) * mm, "end": v(-0.9, -7.2) * mm});
            skLineSegment(sketch, "E2173", {"start": v(-0.9, -7.2) * mm, "end": v(-0.85, -7.23) * mm});
            skLineSegment(sketch, "E2174", {"start": v(-0.85, -7.23) * mm, "end": v(-0.8, -7.25) * mm});
            skLineSegment(sketch, "E2175", {"start": v(-0.8, -7.25) * mm, "end": v(-0.73, -7.25) * mm});
            skLineSegment(sketch, "E2176", {"start": v(-0.73, -7.25) * mm, "end": v(-0.65, -7.24) * mm});
            skLineSegment(sketch, "E2177", {"start": v(-0.65, -7.24) * mm, "end": v(-0.57, -7.21) * mm});
            skLineSegment(sketch, "E2178", {"start": v(-0.57, -7.21) * mm, "end": v(-0.5, -7.17) * mm});
            skLineSegment(sketch, "E2179", {"start": v(-0.5, -7.17) * mm, "end": v(-0.43, -7.11) * mm});
            skLineSegment(sketch, "E2180", {"start": v(-0.43, -7.11) * mm, "end": v(-0.36, -7.04) * mm});
            skLineSegment(sketch, "E2181", {"start": v(-0.36, -7.04) * mm, "end": v(-0.3, -6.95) * mm});
            skLineSegment(sketch, "E2182", {"start": v(-0.3, -6.95) * mm, "end": v(-0.23, -6.85) * mm});
            skLineSegment(sketch, "E2183", {"start": v(-0.23, -6.85) * mm, "end": v(-0.18, -6.73) * mm});
            skLineSegment(sketch, "E2184", {"start": v(-0.18, -6.73) * mm, "end": v(-0.07, -6.47) * mm});
            skLineSegment(sketch, "E2185", {"start": v(-0.07, -6.47) * mm, "end": v(0.02, -6.18) * mm});
            skLineSegment(sketch, "E2186", {"start": v(0.02, -6.18) * mm, "end": v(0.1, -5.86) * mm});
            skLineSegment(sketch, "E2187", {"start": v(0.1, -5.86) * mm, "end": v(0.19, -5.52) * mm});
            skLineSegment(sketch, "E2188", {"start": v(0.19, -5.52) * mm, "end": v(0.32, -4.8) * mm});
            skLineSegment(sketch, "E2189", {"start": v(0.32, -4.8) * mm, "end": v(0.44, -4.12) * mm});
            skLineSegment(sketch, "E2190", {"start": v(0.44, -4.12) * mm, "end": v(0.45, -4.01) * mm});
            skLineSegment(sketch, "E2191", {"start": v(0.45, -4.01) * mm, "end": v(0.45, -3.93) * mm});
            skLineSegment(sketch, "E2192", {"start": v(0.45, -3.93) * mm, "end": v(0.45, -3.89) * mm});
            skLineSegment(sketch, "E2193", {"start": v(0.45, -3.89) * mm, "end": v(0.44, -3.88) * mm});
            skLineSegment(sketch, "E2194", {"start": v(0.44, -3.88) * mm, "end": v(0.43, -3.87) * mm});
            skLineSegment(sketch, "E2195", {"start": v(0.43, -3.87) * mm, "end": v(0.4, -3.9) * mm});
            skLineSegment(sketch, "E2196", {"start": v(0.4, -3.9) * mm, "end": v(0.38, -3.94) * mm});
            skLineSegment(sketch, "E2197", {"start": v(0.38, -3.94) * mm, "end": v(0.35, -4) * mm});
            skLineSegment(sketch, "E2198", {"start": v(0.35, -4) * mm, "end": v(0.33, -4.1) * mm});
            skLineSegment(sketch, "E2199", {"start": v(0.33, -4.1) * mm, "end": v(0.24, -4.62) * mm});
            skLineSegment(sketch, "E2200", {"start": v(0.24, -4.62) * mm, "end": v(0.12, -5.22) * mm});
            skLineSegment(sketch, "E2201", {"start": v(0.12, -5.22) * mm, "end": v(0.05, -5.53) * mm});
            skLineSegment(sketch, "E2202", {"start": v(0.05, -5.53) * mm, "end": v(-0.03, -5.83) * mm});
            skLineSegment(sketch, "E2203", {"start": v(-0.03, -5.83) * mm, "end": v(-0.12, -6.11) * mm});
            skLineSegment(sketch, "E2204", {"start": v(-0.12, -6.11) * mm, "end": v(-0.21, -6.37) * mm});
            skLineSegment(sketch, "E2205", {"start": v(-0.21, -6.37) * mm, "end": v(-0.26, -6.5) * mm});
            skLineSegment(sketch, "E2206", {"start": v(-0.26, -6.5) * mm, "end": v(-0.32, -6.6) * mm});
            skLineSegment(sketch, "E2207", {"start": v(-0.32, -6.6) * mm, "end": v(-0.37, -6.69) * mm});
            skLineSegment(sketch, "E2208", {"start": v(-0.37, -6.69) * mm, "end": v(-0.43, -6.76) * mm});
            skLineSegment(sketch, "E2209", {"start": v(-0.43, -6.76) * mm, "end": v(-0.5, -6.82) * mm});
            skLineSegment(sketch, "E2210", {"start": v(-0.5, -6.82) * mm, "end": v(-0.55, -6.86) * mm});
            skLineSegment(sketch, "E2211", {"start": v(-0.55, -6.86) * mm, "end": v(-0.62, -6.9) * mm});
            skLineSegment(sketch, "E2212", {"start": v(-0.62, -6.9) * mm, "end": v(-0.68, -6.9) * mm});
            skLineSegment(sketch, "E2213", {"start": v(-0.68, -6.9) * mm, "end": v(-0.73, -6.9) * mm});
            skLineSegment(sketch, "E2214", {"start": v(-0.73, -6.9) * mm, "end": v(-0.77, -6.87) * mm});
            skLineSegment(sketch, "E2215", {"start": v(-0.77, -6.87) * mm, "end": v(-0.81, -6.83) * mm});
            skLineSegment(sketch, "E2216", {"start": v(-0.81, -6.83) * mm, "end": v(-0.85, -6.78) * mm});
            skLineSegment(sketch, "E2217", {"start": v(-0.85, -6.78) * mm, "end": v(-0.88, -6.72) * mm});
            skLineSegment(sketch, "E2218", {"start": v(-0.88, -6.72) * mm, "end": v(-0.9, -6.64) * mm});
            skLineSegment(sketch, "E2219", {"start": v(-0.9, -6.64) * mm, "end": v(-0.94, -6.46) * mm});
            skLineSegment(sketch, "E2220", {"start": v(-0.94, -6.46) * mm, "end": v(-0.96, -6.24) * mm});
            skLineSegment(sketch, "E2221", {"start": v(-0.96, -6.24) * mm, "end": v(-0.98, -6) * mm});
            skLineSegment(sketch, "E2222", {"start": v(-0.98, -6) * mm, "end": v(-0.98, -5.76) * mm});
            skLineSegment(sketch, "E2223", {"start": v(-0.98, -5.76) * mm, "end": v(-0.97, -5.5) * mm});
            skLineSegment(sketch, "E2224", {"start": v(-0.97, -5.5) * mm, "end": v(-0.94, -5.03) * mm});
            skLineSegment(sketch, "E2225", {"start": v(-0.94, -5.03) * mm, "end": v(-0.9, -4.66) * mm});
            skLineSegment(sketch, "E2226", {"start": v(-0.9, -4.66) * mm, "end": v(-0.82, -4.65) * mm});
            skLineSegment(sketch, "E2227", {"start": v(-0.82, -4.65) * mm, "end": v(-0.73, -4.6) * mm});
            skLineSegment(sketch, "E2228", {"start": v(-0.73, -4.6) * mm, "end": v(-0.63, -4.54) * mm});
            skLineSegment(sketch, "E2229", {"start": v(-0.63, -4.54) * mm, "end": v(-0.52, -4.44) * mm});
            skLineSegment(sketch, "E2230", {"start": v(-0.52, -4.44) * mm, "end": v(-0.41, -4.33) * mm});
            skLineSegment(sketch, "E2231", {"start": v(-0.41, -4.33) * mm, "end": v(-0.31, -4.21) * mm});
            skLineSegment(sketch, "E2232", {"start": v(-0.31, -4.21) * mm, "end": v(-0.22, -4.08) * mm});
            skLineSegment(sketch, "E2233", {"start": v(-0.22, -4.08) * mm, "end": v(-0.14, -3.94) * mm});
            skLineSegment(sketch, "E2234", {"start": v(-0.14, -3.94) * mm, "end": v(0, -3.62) * mm});
            skLineSegment(sketch, "E2235", {"start": v(0, -3.62) * mm, "end": v(0.11, -3.3) * mm});
            skLineSegment(sketch, "E2236", {"start": v(0.11, -3.3) * mm, "end": v(0.2, -2.96) * mm});
            skLineSegment(sketch, "E2237", {"start": v(0.2, -2.96) * mm, "end": v(0.27, -2.62) * mm});
            skLineSegment(sketch, "E2238", {"start": v(0.27, -2.62) * mm, "end": v(0.3, -2.3) * mm});
            skLineSegment(sketch, "E2239", {"start": v(0.3, -2.3) * mm, "end": v(0.3, -2.15) * mm});
            skLineSegment(sketch, "E2240", {"start": v(0.3, -2.15) * mm, "end": v(0.3, -2.01) * mm});
            skLineSegment(sketch, "E2241", {"start": v(0.3, -2.01) * mm, "end": v(0.29, -1.88) * mm});
            skLineSegment(sketch, "E2242", {"start": v(0.29, -1.88) * mm, "end": v(0.27, -1.76) * mm});
            skLineSegment(sketch, "E2243", {"start": v(0.27, -1.76) * mm, "end": v(0.24, -1.65) * mm});
            skLineSegment(sketch, "E2244", {"start": v(0.24, -1.65) * mm, "end": v(0.2, -1.55) * mm});
            skLineSegment(sketch, "E2245", {"start": v(0.2, -1.55) * mm, "end": v(0.15, -1.47) * mm});
            skLineSegment(sketch, "E2246", {"start": v(0.15, -1.47) * mm, "end": v(0.09, -1.4) * mm});
            skLineSegment(sketch, "E2247", {"start": v(0.09, -1.4) * mm, "end": v(0.03, -1.37) * mm});
            skLineSegment(sketch, "E2248", {"start": v(0.03, -1.37) * mm, "end": v(-0.03, -1.35) * mm});
            skLineSegment(sketch, "E2249", {"start": v(-0.03, -1.35) * mm, "end": v(-0.1, -1.36) * mm});
            skLineSegment(sketch, "E2250", {"start": v(-0.1, -1.36) * mm, "end": v(-0.17, -1.39) * mm});
            skLineSegment(sketch, "E2251", {"start": v(-0.17, -1.39) * mm, "end": v(-0.24, -1.44) * mm});
            skLineSegment(sketch, "E2252", {"start": v(-0.24, -1.44) * mm, "end": v(-0.3, -1.51) * mm});
            skLineSegment(sketch, "E2253", {"start": v(-0.3, -1.51) * mm, "end": v(-0.38, -1.6) * mm});
            skLineSegment(sketch, "E2254", {"start": v(-0.38, -1.6) * mm, "end": v(-0.45, -1.7) * mm});
            skLineSegment(sketch, "E2255", {"start": v(-0.45, -1.7) * mm, "end": v(-0.52, -1.83) * mm});
            skLineSegment(sketch, "E2256", {"start": v(-0.52, -1.83) * mm, "end": v(-0.6, -1.96) * mm});
            skLineSegment(sketch, "E2257", {"start": v(-0.6, -1.96) * mm, "end": v(-0.72, -2.26) * mm});
            skLineSegment(sketch, "E2258", {"start": v(-0.72, -2.26) * mm, "end": v(-0.85, -2.61) * mm});
            skLineSegment(sketch, "E2259", {"start": v(-0.85, -2.61) * mm, "end": v(-0.95, -2.95) * mm});
            skLineSegment(sketch, "E2260", {"start": v(-0.95, -2.95) * mm, "end": v(-1.04, -3.31) * mm});
            skLineSegment(sketch, "E2261", {"start": v(-1.04, -3.31) * mm, "end": v(-1.12, -3.7) * mm});
            skLineSegment(sketch, "E2262", {"start": v(-1.12, -3.7) * mm, "end": v(-1.2, -4.1) * mm});
            skLineSegment(sketch, "E2263", {"start": v(-1.2, -4.1) * mm, "end": v(-1.22, -4.32) * mm});
            skLineSegment(sketch, "E2264", {"start": v(-1.22, -4.32) * mm, "end": v(-1.35, -4.97) * mm});
            skLineSegment(sketch, "E2265", {"start": v(-1.35, -4.97) * mm, "end": v(-1.48, -5.55) * mm});
            skLineSegment(sketch, "E2266", {"start": v(-1.48, -5.55) * mm, "end": v(-1.62, -6.14) * mm});
            skLineSegment(sketch, "E2267", {"start": v(-1.62, -6.14) * mm, "end": v(-1.7, -6.4) * mm});
            skLineSegment(sketch, "E2268", {"start": v(-1.7, -6.4) * mm, "end": v(-1.8, -6.62) * mm});
            skLineSegment(sketch, "E2269", {"start": v(-1.8, -6.62) * mm, "end": v(-1.84, -6.7) * mm});
            skLineSegment(sketch, "E2270", {"start": v(-1.84, -6.7) * mm, "end": v(-1.88, -6.76) * mm});
            skLineSegment(sketch, "E2271", {"start": v(-1.88, -6.76) * mm, "end": v(-1.93, -6.81) * mm});
            skLineSegment(sketch, "E2272", {"start": v(-1.93, -6.81) * mm, "end": v(-1.97, -6.85) * mm});
            skLineSegment(sketch, "E2273", {"start": v(-1.97, -6.85) * mm, "end": v(-2.02, -6.86) * mm});
            skLineSegment(sketch, "E2274", {"start": v(-2.02, -6.86) * mm, "end": v(-2.06, -6.86) * mm});
            skLineSegment(sketch, "E2275", {"start": v(-2.06, -6.86) * mm, "end": v(-2.1, -6.85) * mm});
            skLineSegment(sketch, "E2276", {"start": v(-2.1, -6.85) * mm, "end": v(-2.13, -6.81) * mm});
            skLineSegment(sketch, "E2277", {"start": v(-2.13, -6.81) * mm, "end": v(-2.16, -6.76) * mm});
            skLineSegment(sketch, "E2278", {"start": v(-2.16, -6.76) * mm, "end": v(-2.2, -6.7) * mm});
            skLineSegment(sketch, "E2279", {"start": v(-2.2, -6.7) * mm, "end": v(-2.25, -6.52) * mm});
            skLineSegment(sketch, "E2280", {"start": v(-2.25, -6.52) * mm, "end": v(-2.27, -6.4) * mm});
            skLineSegment(sketch, "E2281", {"start": v(-2.27, -6.4) * mm, "end": v(-2.28, -6.27) * mm});
            skLineSegment(sketch, "E2282", {"start": v(-2.28, -6.27) * mm, "end": v(-2.3, -5.95) * mm});
            skLineSegment(sketch, "E2283", {"start": v(-2.3, -5.95) * mm, "end": v(-2.29, -5.56) * mm});
            skLineSegment(sketch, "E2284", {"start": v(-2.29, -5.56) * mm, "end": v(-2.26, -5.1) * mm});
            skLineSegment(sketch, "E2285", {"start": v(-2.26, -5.1) * mm, "end": v(-2.19, -4.52) * mm});
            skLineSegment(sketch, "E2286", {"start": v(-2.19, -4.52) * mm, "end": v(-2.13, -4.02) * mm});
            skLineSegment(sketch, "E2287", {"start": v(-2.13, -4.02) * mm, "end": v(-1.91, -3.46) * mm});
            skLineSegment(sketch, "E2288", {"start": v(-1.91, -3.46) * mm, "end": v(-1.72, -2.88) * mm});
            skLineSegment(sketch, "E2289", {"start": v(-1.72, -2.88) * mm, "end": v(-1.54, -2.28) * mm});
            skLineSegment(sketch, "E2290", {"start": v(-1.54, -2.28) * mm, "end": v(-1.38, -1.65) * mm});
            skLineSegment(sketch, "E2291", {"start": v(-1.38, -1.65) * mm, "end": v(-1.23, -1.02) * mm});
            skLineSegment(sketch, "E2292", {"start": v(-1.23, -1.02) * mm, "end": v(-1.1, -0.38) * mm});
            skLineSegment(sketch, "E2293", {"start": v(-1.1, -0.38) * mm, "end": v(-0.98, 0.25) * mm});
            skLineSegment(sketch, "E2294", {"start": v(-0.98, 0.25) * mm, "end": v(-0.87, 0.9) * mm});
            skLineSegment(sketch, "E2295", {"start": v(-0.87, 0.9) * mm, "end": v(-0.78, 1.5) * mm});
            skLineSegment(sketch, "E2296", {"start": v(-0.78, 1.5) * mm, "end": v(-0.73, 2) * mm});
            skLineSegment(sketch, "E2297", {"start": v(-0.73, 2) * mm, "end": v(-0.72, 2.22) * mm});
            skLineSegment(sketch, "E2298", {"start": v(-0.72, 2.22) * mm, "end": v(-0.72, 2.41) * mm});
            skLineSegment(sketch, "E2299", {"start": v(-0.72, 2.41) * mm, "end": v(-0.73, 2.58) * mm});
            skLineSegment(sketch, "E2300", {"start": v(-0.73, 2.58) * mm, "end": v(-0.75, 2.72) * mm});
            skLineSegment(sketch, "E2301", {"start": v(-0.75, 2.72) * mm, "end": v(-0.77, 2.84) * mm});
            skLineSegment(sketch, "E2302", {"start": v(-0.77, 2.84) * mm, "end": v(-0.8, 2.94) * mm});
            skLineSegment(sketch, "E2303", {"start": v(-0.8, 2.94) * mm, "end": v(-0.83, 3) * mm});
            skLineSegment(sketch, "E2304", {"start": v(-0.83, 3) * mm, "end": v(-0.87, 3.06) * mm});
            skLineSegment(sketch, "E2305", {"start": v(-0.87, 3.06) * mm, "end": v(-0.91, 3.08) * mm});
            skLineSegment(sketch, "E2306", {"start": v(-0.91, 3.08) * mm, "end": v(-0.96, 3.08) * mm});
            skLineSegment(sketch, "E2307", {"start": v(-0.96, 3.08) * mm, "end": v(-1, 3.06) * mm});
            skLineSegment(sketch, "E2308", {"start": v(-1, 3.06) * mm, "end": v(-1.06, 3) * mm});
            skLineSegment(sketch, "E2309", {"start": v(-1.06, 3) * mm, "end": v(-1.12, 2.94) * mm});
            skLineSegment(sketch, "E2310", {"start": v(-1.12, 2.94) * mm, "end": v(-1.18, 2.84) * mm});
            skLineSegment(sketch, "E2311", {"start": v(-1.18, 2.84) * mm, "end": v(-1.24, 2.73) * mm});
            skLineSegment(sketch, "E2312", {"start": v(-1.24, 2.73) * mm, "end": v(-1.3, 2.58) * mm});
            skLineSegment(sketch, "E2313", {"start": v(-1.3, 2.58) * mm, "end": v(-1.41, 2.23) * mm});
            skLineSegment(sketch, "E2314", {"start": v(-1.41, 2.23) * mm, "end": v(-1.53, 1.8) * mm});
            skLineSegment(sketch, "E2315", {"start": v(-1.53, 1.8) * mm, "end": v(-1.66, 1.16) * mm});
            skLineSegment(sketch, "E2316", {"start": v(-1.66, 1.16) * mm, "end": v(-1.8, 0.48) * mm});
            skLineSegment(sketch, "E2317", {"start": v(-1.8, 0.48) * mm, "end": v(-1.93, -0.24) * mm});
            skLineSegment(sketch, "E2318", {"start": v(-1.93, -0.24) * mm, "end": v(-2.05, -1) * mm});
            skLineSegment(sketch, "E2319", {"start": v(-2.05, -1) * mm, "end": v(-2.18, -1.78) * mm});
            skLineSegment(sketch, "E2320", {"start": v(-2.18, -1.78) * mm, "end": v(-2.28, -2.54) * mm});
            skLineSegment(sketch, "E2321", {"start": v(-2.28, -2.54) * mm, "end": v(-2.38, -3.27) * mm});
            skLineSegment(sketch, "E2322", {"start": v(-2.38, -3.27) * mm, "end": v(-2.46, -4) * mm});
            skLineSegment(sketch, "E2323", {"start": v(-2.46, -4) * mm, "end": v(-2.46, -4.03) * mm});
            skLineSegment(sketch, "E2324", {"start": v(-2.46, -4.03) * mm, "end": v(-2.47, -4.06) * mm});
            skLineSegment(sketch, "E2325", {"start": v(-2.47, -4.06) * mm, "end": v(-2.65, -4.97) * mm});
            skLineSegment(sketch, "E2326", {"start": v(-2.65, -4.97) * mm, "end": v(-2.78, -5.55) * mm});
            skLineSegment(sketch, "E2327", {"start": v(-2.78, -5.55) * mm, "end": v(-2.93, -6.14) * mm});
            skLineSegment(sketch, "E2328", {"start": v(-2.93, -6.14) * mm, "end": v(-3.01, -6.4) * mm});
            skLineSegment(sketch, "E2329", {"start": v(-3.01, -6.4) * mm, "end": v(-3.1, -6.62) * mm});
            skLineSegment(sketch, "E2330", {"start": v(-3.1, -6.62) * mm, "end": v(-3.14, -6.7) * mm});
            skLineSegment(sketch, "E2331", {"start": v(-3.14, -6.7) * mm, "end": v(-3.19, -6.76) * mm});
            skLineSegment(sketch, "E2332", {"start": v(-3.19, -6.76) * mm, "end": v(-3.23, -6.81) * mm});
            skLineSegment(sketch, "E2333", {"start": v(-3.23, -6.81) * mm, "end": v(-3.28, -6.85) * mm});
            skLineSegment(sketch, "E2334", {"start": v(-3.28, -6.85) * mm, "end": v(-3.32, -6.86) * mm});
            skLineSegment(sketch, "E2335", {"start": v(-3.32, -6.86) * mm, "end": v(-3.36, -6.86) * mm});
            skLineSegment(sketch, "E2336", {"start": v(-3.36, -6.86) * mm, "end": v(-3.4, -6.85) * mm});
            skLineSegment(sketch, "E2337", {"start": v(-3.4, -6.85) * mm, "end": v(-3.43, -6.81) * mm});
            skLineSegment(sketch, "E2338", {"start": v(-3.43, -6.81) * mm, "end": v(-3.47, -6.76) * mm});
            skLineSegment(sketch, "E2339", {"start": v(-3.47, -6.76) * mm, "end": v(-3.5, -6.7) * mm});
            skLineSegment(sketch, "E2340", {"start": v(-3.5, -6.7) * mm, "end": v(-3.55, -6.52) * mm});
            skLineSegment(sketch, "E2341", {"start": v(-3.55, -6.52) * mm, "end": v(-3.57, -6.4) * mm});
            skLineSegment(sketch, "E2342", {"start": v(-3.57, -6.4) * mm, "end": v(-3.58, -6.27) * mm});
            skLineSegment(sketch, "E2343", {"start": v(-3.58, -6.27) * mm, "end": v(-3.6, -5.95) * mm});
            skLineSegment(sketch, "E2344", {"start": v(-3.6, -5.95) * mm, "end": v(-3.59, -5.56) * mm});
            skLineSegment(sketch, "E2345", {"start": v(-3.59, -5.56) * mm, "end": v(-3.56, -5.1) * mm});
            skLineSegment(sketch, "E2346", {"start": v(-3.56, -5.1) * mm, "end": v(-3.5, -4.52) * mm});
            skLineSegment(sketch, "E2347", {"start": v(-3.5, -4.52) * mm, "end": v(-3.43, -4.02) * mm});
            skLineSegment(sketch, "E2348", {"start": v(-3.43, -4.02) * mm, "end": v(-3.22, -3.46) * mm});
            skLineSegment(sketch, "E2349", {"start": v(-3.22, -3.46) * mm, "end": v(-3.02, -2.88) * mm});
            skLineSegment(sketch, "E2350", {"start": v(-3.02, -2.88) * mm, "end": v(-2.84, -2.28) * mm});
            skLineSegment(sketch, "E2351", {"start": v(-2.84, -2.28) * mm, "end": v(-2.68, -1.65) * mm});
            skLineSegment(sketch, "E2352", {"start": v(-2.68, -1.65) * mm, "end": v(-2.54, -1.02) * mm});
            skLineSegment(sketch, "E2353", {"start": v(-2.54, -1.02) * mm, "end": v(-2.4, -0.38) * mm});
            skLineSegment(sketch, "E2354", {"start": v(-2.4, -0.38) * mm, "end": v(-2.28, 0.25) * mm});
            skLineSegment(sketch, "E2355", {"start": v(-2.28, 0.25) * mm, "end": v(-2.17, 0.9) * mm});
            skLineSegment(sketch, "E2356", {"start": v(-2.17, 0.9) * mm, "end": v(-2.08, 1.5) * mm});
            skLineSegment(sketch, "E2357", {"start": v(-2.08, 1.5) * mm, "end": v(-2.04, 2) * mm});
            skLineSegment(sketch, "E2358", {"start": v(-2.04, 2) * mm, "end": v(-2.02, 2.22) * mm});
            skLineSegment(sketch, "E2359", {"start": v(-2.02, 2.22) * mm, "end": v(-2.02, 2.41) * mm});
            skLineSegment(sketch, "E2360", {"start": v(-2.02, 2.41) * mm, "end": v(-2.03, 2.58) * mm});
            skLineSegment(sketch, "E2361", {"start": v(-2.03, 2.58) * mm, "end": v(-2.05, 2.72) * mm});
            skLineSegment(sketch, "E2362", {"start": v(-2.05, 2.72) * mm, "end": v(-2.07, 2.84) * mm});
            skLineSegment(sketch, "E2363", {"start": v(-2.07, 2.84) * mm, "end": v(-2.1, 2.94) * mm});
            skLineSegment(sketch, "E2364", {"start": v(-2.1, 2.94) * mm, "end": v(-2.13, 3) * mm});
            skLineSegment(sketch, "E2365", {"start": v(-2.13, 3) * mm, "end": v(-2.17, 3.06) * mm});
            skLineSegment(sketch, "E2366", {"start": v(-2.17, 3.06) * mm, "end": v(-2.21, 3.08) * mm});
            skLineSegment(sketch, "E2367", {"start": v(-2.21, 3.08) * mm, "end": v(-2.26, 3.08) * mm});
            skLineSegment(sketch, "E2368", {"start": v(-2.26, 3.08) * mm, "end": v(-2.3, 3.06) * mm});
            skLineSegment(sketch, "E2369", {"start": v(-2.3, 3.06) * mm, "end": v(-2.37, 3) * mm});
            skLineSegment(sketch, "E2370", {"start": v(-2.37, 3) * mm, "end": v(-2.42, 2.94) * mm});
            skLineSegment(sketch, "E2371", {"start": v(-2.42, 2.94) * mm, "end": v(-2.48, 2.84) * mm});
            skLineSegment(sketch, "E2372", {"start": v(-2.48, 2.84) * mm, "end": v(-2.54, 2.73) * mm});
            skLineSegment(sketch, "E2373", {"start": v(-2.54, 2.73) * mm, "end": v(-2.6, 2.58) * mm});
            skLineSegment(sketch, "E2374", {"start": v(-2.6, 2.58) * mm, "end": v(-2.71, 2.23) * mm});
            skLineSegment(sketch, "E2375", {"start": v(-2.71, 2.23) * mm, "end": v(-2.83, 1.8) * mm});
            skLineSegment(sketch, "E2376", {"start": v(-2.83, 1.8) * mm, "end": v(-2.96, 1.16) * mm});
            skLineSegment(sketch, "E2377", {"start": v(-2.96, 1.16) * mm, "end": v(-3.1, 0.48) * mm});
            skLineSegment(sketch, "E2378", {"start": v(-3.1, 0.48) * mm, "end": v(-3.23, -0.24) * mm});
            skLineSegment(sketch, "E2379", {"start": v(-3.23, -0.24) * mm, "end": v(-3.36, -1) * mm});
            skLineSegment(sketch, "E2380", {"start": v(-3.36, -1) * mm, "end": v(-3.48, -1.78) * mm});
            skLineSegment(sketch, "E2381", {"start": v(-3.48, -1.78) * mm, "end": v(-3.59, -2.54) * mm});
            skLineSegment(sketch, "E2382", {"start": v(-3.59, -2.54) * mm, "end": v(-3.68, -3.27) * mm});
            skLineSegment(sketch, "E2383", {"start": v(-3.68, -3.27) * mm, "end": v(-3.76, -4) * mm});
            skLineSegment(sketch, "E2384", {"start": v(-3.76, -4) * mm, "end": v(-3.76, -4) * mm});
            skLineSegment(sketch, "E2385", {"start": v(-3.76, -4) * mm, "end": v(-3.77, -4.04) * mm});
            skLineSegment(sketch, "E2386", {"start": v(-3.77, -4.04) * mm, "end": v(-3.9, -4.74) * mm});
            skLineSegment(sketch, "E2387", {"start": v(-3.9, -4.74) * mm, "end": v(-4.05, -5.42) * mm});
            skLineSegment(sketch, "E2388", {"start": v(-4.05, -5.42) * mm, "end": v(-4.12, -5.74) * mm});
            skLineSegment(sketch, "E2389", {"start": v(-4.12, -5.74) * mm, "end": v(-4.2, -6.03) * mm});
            skLineSegment(sketch, "E2390", {"start": v(-4.2, -6.03) * mm, "end": v(-4.27, -6.29) * mm});
            skLineSegment(sketch, "E2391", {"start": v(-4.27, -6.29) * mm, "end": v(-4.35, -6.51) * mm});
            skLineSegment(sketch, "E2392", {"start": v(-4.35, -6.51) * mm, "end": v(-4.4, -6.64) * mm});
            skLineSegment(sketch, "E2393", {"start": v(-4.4, -6.64) * mm, "end": v(-4.48, -6.74) * mm});
            skLineSegment(sketch, "E2394", {"start": v(-4.48, -6.74) * mm, "end": v(-4.52, -6.79) * mm});
            skLineSegment(sketch, "E2395", {"start": v(-4.52, -6.79) * mm, "end": v(-4.55, -6.81) * mm});
            skLineSegment(sketch, "E2396", {"start": v(-4.55, -6.81) * mm, "end": v(-4.6, -6.83) * mm});
            skLineSegment(sketch, "E2397", {"start": v(-4.6, -6.83) * mm, "end": v(-4.63, -6.83) * mm});
            skLineSegment(sketch, "E2398", {"start": v(-4.63, -6.83) * mm, "end": v(-4.66, -6.81) * mm});
            skLineSegment(sketch, "E2399", {"start": v(-4.66, -6.81) * mm, "end": v(-4.68, -6.8) * mm});
            skLineSegment(sketch, "E2400", {"start": v(-4.68, -6.8) * mm, "end": v(-4.73, -6.73) * mm});
            skLineSegment(sketch, "E2401", {"start": v(-4.73, -6.73) * mm, "end": v(-4.76, -6.63) * mm});
            skLineSegment(sketch, "E2402", {"start": v(-4.76, -6.63) * mm, "end": v(-4.78, -6.5) * mm});
            skLineSegment(sketch, "E2403", {"start": v(-4.78, -6.5) * mm, "end": v(-4.78, -6.35) * mm});
            skLineSegment(sketch, "E2404", {"start": v(-4.78, -6.35) * mm, "end": v(-4.78, -6.18) * mm});
            skLineSegment(sketch, "E2405", {"start": v(-4.78, -6.18) * mm, "end": v(-4.76, -5.8) * mm});
            skLineSegment(sketch, "E2406", {"start": v(-4.76, -5.8) * mm, "end": v(-4.71, -5.51) * mm});
            skLineSegment(sketch, "E2407", {"start": v(-4.71, -5.51) * mm, "end": v(-4.68, -5.32) * mm});
            skLineSegment(sketch, "E2408", {"start": v(-4.68, -5.32) * mm, "end": v(-4.2, -2.26) * mm});
            skLineSegment(sketch, "E2409", {"start": v(-4.2, -2.26) * mm, "end": v(-4.16, -2) * mm});
            skLineSegment(sketch, "E2410", {"start": v(-4.16, -2) * mm, "end": v(-4.15, -1.9) * mm});
            skLineSegment(sketch, "E2411", {"start": v(-4.15, -1.9) * mm, "end": v(-4.16, -1.82) * mm});
            skLineSegment(sketch, "E2412", {"start": v(-4.16, -1.82) * mm, "end": v(-4.17, -1.76) * mm});
            skLineSegment(sketch, "E2413", {"start": v(-4.17, -1.76) * mm, "end": v(-4.2, -1.72) * mm});
            skLineSegment(sketch, "E2414", {"start": v(-4.2, -1.72) * mm, "end": v(-4.26, -1.7) * mm});
            skLineSegment(sketch, "E2415", {"start": v(-4.26, -1.7) * mm, "end": v(-4.32, -1.68) * mm});
            skLineSegment(sketch, "E2416", {"start": v(-4.32, -1.68) * mm, "end": v(-4.66, -1.7) * mm});
            skLineSegment(sketch, "E2417", {"start": v(-4.66, -1.7) * mm, "end": v(-4.63, -1.8) * mm});
            skLineSegment(sketch, "E2418", {"start": v(-4.63, -1.8) * mm, "end": v(-4.6, -1.96) * mm});
            skLineSegment(sketch, "E2419", {"start": v(-4.6, -1.96) * mm, "end": v(-4.59, -2.06) * mm});
            skLineSegment(sketch, "E2420", {"start": v(-4.59, -2.06) * mm, "end": v(-4.58, -2.16) * mm});
            skLineSegment(sketch, "E2421", {"start": v(-4.58, -2.16) * mm, "end": v(-4.59, -2.27) * mm});
            skLineSegment(sketch, "E2422", {"start": v(-4.59, -2.27) * mm, "end": v(-4.6, -2.39) * mm});
            skLineSegment(sketch, "E2423", {"start": v(-4.6, -2.39) * mm, "end": v(-4.99, -5.06) * mm});
            skLineSegment(sketch, "E2424", {"start": v(-4.99, -5.06) * mm, "end": v(-5.02, -5.28) * mm});
            skLineSegment(sketch, "E2425", {"start": v(-5.02, -5.28) * mm, "end": v(-5.04, -5.51) * mm});
            skLineSegment(sketch, "E2426", {"start": v(-5.04, -5.51) * mm, "end": v(-5.06, -5.75) * mm});
            skLineSegment(sketch, "E2427", {"start": v(-5.06, -5.75) * mm, "end": v(-5.06, -5.99) * mm});
            skLineSegment(sketch, "E2428", {"start": v(-5.06, -5.99) * mm, "end": v(-5.06, -6.22) * mm});
            skLineSegment(sketch, "E2429", {"start": v(-5.06, -6.22) * mm, "end": v(-5.04, -6.44) * mm});
            skLineSegment(sketch, "E2430", {"start": v(-5.04, -6.44) * mm, "end": v(-5.02, -6.64) * mm});
            skLineSegment(sketch, "E2431", {"start": v(-5.02, -6.64) * mm, "end": v(-4.98, -6.82) * mm});
            skLineSegment(sketch, "E2432", {"start": v(-4.98, -6.82) * mm, "end": v(-4.92, -6.98) * mm});
            skLineSegment(sketch, "E2433", {"start": v(-4.92, -6.98) * mm, "end": v(-4.89, -7.04) * mm});
            skLineSegment(sketch, "E2434", {"start": v(-4.89, -7.04) * mm, "end": v(-4.85, -7.09) * mm});
            skLineSegment(sketch, "E2435", {"start": v(-4.85, -7.09) * mm, "end": v(-4.8, -7.13) * mm});
            skLineSegment(sketch, "E2436", {"start": v(-4.8, -7.13) * mm, "end": v(-4.76, -7.16) * mm});
            skLineSegment(sketch, "E2437", {"start": v(-4.76, -7.16) * mm, "end": v(-4.71, -7.18) * mm});
            skLineSegment(sketch, "E2438", {"start": v(-4.71, -7.18) * mm, "end": v(-4.66, -7.19) * mm});
            skLineSegment(sketch, "E2439", {"start": v(-4.66, -7.19) * mm, "end": v(-4.6, -7.17) * mm});
            skLineSegment(sketch, "E2440", {"start": v(-4.6, -7.17) * mm, "end": v(-4.55, -7.14) * mm});
            skLineSegment(sketch, "E2441", {"start": v(-4.55, -7.14) * mm, "end": v(-4.5, -7.1) * mm});
            skLineSegment(sketch, "E2442", {"start": v(-4.5, -7.1) * mm, "end": v(-4.44, -7.03) * mm});
            skLineSegment(sketch, "E2443", {"start": v(-4.44, -7.03) * mm, "end": v(-4.39, -6.95) * mm});
            skLineSegment(sketch, "E2444", {"start": v(-4.39, -6.95) * mm, "end": v(-4.34, -6.85) * mm});
            skLineSegment(sketch, "E2445", {"start": v(-4.34, -6.85) * mm, "end": v(-4.24, -6.61) * mm});
            skLineSegment(sketch, "E2446", {"start": v(-4.24, -6.61) * mm, "end": v(-4.15, -6.33) * mm});
            skLineSegment(sketch, "E2447", {"start": v(-4.15, -6.33) * mm, "end": v(-4.07, -6.03) * mm});
            skLineSegment(sketch, "E2448", {"start": v(-4.07, -6.03) * mm, "end": v(-3.99, -5.71) * mm});
            skLineSegment(sketch, "E2449", {"start": v(-3.99, -5.71) * mm, "end": v(-3.91, -5.37) * mm});
            skLineSegment(sketch, "E2450", {"start": v(-3.91, -5.37) * mm, "end": v(-3.88, -5.18) * mm});
            skLineSegment(sketch, "E2451", {"start": v(-3.88, -5.18) * mm, "end": v(-3.89, -5.27) * mm});
            skLineSegment(sketch, "E2452", {"start": v(-3.89, -5.27) * mm, "end": v(-3.9, -5.63) * mm});
            skLineSegment(sketch, "E2453", {"start": v(-3.9, -5.63) * mm, "end": v(-3.91, -5.97) * mm});
            skLineSegment(sketch, "E2454", {"start": v(-3.91, -5.97) * mm, "end": v(-3.9, -6.3) * mm});
            skLineSegment(sketch, "E2455", {"start": v(-3.9, -6.3) * mm, "end": v(-3.88, -6.6) * mm});
            skLineSegment(sketch, "E2456", {"start": v(-3.88, -6.6) * mm, "end": v(-3.85, -6.74) * mm});
            skLineSegment(sketch, "E2457", {"start": v(-3.85, -6.74) * mm, "end": v(-3.82, -6.86) * mm});
            skLineSegment(sketch, "E2458", {"start": v(-3.82, -6.86) * mm, "end": v(-3.79, -6.96) * mm});
            skLineSegment(sketch, "E2459", {"start": v(-3.79, -6.96) * mm, "end": v(-3.74, -7.05) * mm});
            skLineSegment(sketch, "E2460", {"start": v(-3.74, -7.05) * mm, "end": v(-3.69, -7.12) * mm});
            skLineSegment(sketch, "E2461", {"start": v(-3.69, -7.12) * mm, "end": v(-3.62, -7.17) * mm});
            skLineSegment(sketch, "E2462", {"start": v(-3.62, -7.17) * mm, "end": v(-3.55, -7.2) * mm});
            skLineSegment(sketch, "E2463", {"start": v(-3.55, -7.2) * mm, "end": v(-3.47, -7.22) * mm});
            skLineSegment(sketch, "E2464", {"start": v(-3.47, -7.22) * mm, "end": v(-3.4, -7.2) * mm});
            skLineSegment(sketch, "E2465", {"start": v(-3.4, -7.2) * mm, "end": v(-3.32, -7.17) * mm});
            skLineSegment(sketch, "E2466", {"start": v(-3.32, -7.17) * mm, "end": v(-3.25, -7.12) * mm});
            skLineSegment(sketch, "E2467", {"start": v(-3.25, -7.12) * mm, "end": v(-3.19, -7.05) * mm});
            skLineSegment(sketch, "E2468", {"start": v(-3.19, -7.05) * mm, "end": v(-3.12, -6.97) * mm});
            skLineSegment(sketch, "E2469", {"start": v(-3.12, -6.97) * mm, "end": v(-3.06, -6.87) * mm});
            skLineSegment(sketch, "E2470", {"start": v(-3.06, -6.87) * mm, "end": v(-3, -6.75) * mm});
            skLineSegment(sketch, "E2471", {"start": v(-3, -6.75) * mm, "end": v(-2.95, -6.61) * mm});
            skLineSegment(sketch, "E2472", {"start": v(-2.95, -6.61) * mm, "end": v(-2.84, -6.32) * mm});
            skLineSegment(sketch, "E2473", {"start": v(-2.84, -6.32) * mm, "end": v(-2.75, -6) * mm});
            skLineSegment(sketch, "E2474", {"start": v(-2.75, -6) * mm, "end": v(-2.67, -5.67) * mm});
            skLineSegment(sketch, "E2475", {"start": v(-2.67, -5.67) * mm, "end": v(-2.6, -5.32) * mm});
            skLineSegment(sketch, "E2476", {"start": v(-2.6, -5.32) * mm, "end": v(-2.58, -5.27) * mm});
            skLineSegment(sketch, "E2477", {"start": v(-39.7, -13.17) * mm, "end": v(37.62, -11.88) * mm});
            skLineSegment(sketch, "E2478", {"start": v(37.62, -11.88) * mm, "end": v(39.7, 13.17) * mm});
            skLineSegment(sketch, "E2479", {"start": v(39.7, 13.17) * mm, "end": v(-39.7, 9.6) * mm});
            skLineSegment(sketch, "E2480", {"start": v(-39.7, 9.6) * mm, "end": v(-39.7, -13.17) * mm});
            skSolve(sketch);
        }
        {
            var Q0;
            Q0=makeQuery(id+"F0.imprint","IMPRINT",FACE,{"disambiguationData":[TD([[makeQuery(id+"F0.imprint","IMPRINT",EDGE,{"derivedFrom":sQuery(id+"F0.wireOp",EDGE,"E0")}),-1.0]])]});
            var Q1;
            Q1=makeQuery(id+"F0.imprint","IMPRINT",FACE,{"disambiguationData":[TD([[makeQuery(id+"F0.imprint","IMPRINT",EDGE,{"derivedFrom":sQuery(id+"F0.wireOp",EDGE,"E0")}),1.0]])]});
            var Q2;
            Q2=makeQuery(id+"F0.imprint","IMPRINT",FACE,{"disambiguationData":[TD([[makeQuery(id+"F0.imprint","IMPRINT",EDGE,{"derivedFrom":sQuery(id+"F0.wireOp",EDGE,"E857")}),-1.0]])]});
            var Q3;
            Q3=makeQuery(id+"F0.imprint","IMPRINT",FACE,{"disambiguationData":[TD([[makeQuery(id+"F0.imprint","IMPRINT",EDGE,{"derivedFrom":sQuery(id+"F0.wireOp",EDGE,"E993")}),-1.0]])]});
            var Q4;
            Q4=makeQuery(id+"F0.imprint","IMPRINT",FACE,{"disambiguationData":[TD([[makeQuery(id+"F0.imprint","IMPRINT",EDGE,{"derivedFrom":sQuery(id+"F0.wireOp",EDGE,"E1913")}),1.0]])]});
            var Q5;
            Q5=makeQuery(id+"F0.imprint","IMPRINT",FACE,{"disambiguationData":[TD([[makeQuery(id+"F0.imprint","IMPRINT",EDGE,{"derivedFrom":sQuery(id+"F0.wireOp",EDGE,"E1560")}),1.0]])]});
            var Q6;
            Q6=makeQuery(id+"F0.imprint","IMPRINT",FACE,{"disambiguationData":[TD([[makeQuery(id+"F0.imprint","IMPRINT",EDGE,{"derivedFrom":sQuery(id+"F0.wireOp",EDGE,"E1676")}),1.0]])]});
            var Q7;
            Q7=makeQuery(id+"F0.imprint","IMPRINT",FACE,{"disambiguationData":[TD([[makeQuery(id+"F0.imprint","IMPRINT",EDGE,{"derivedFrom":sQuery(id+"F0.wireOp",EDGE,"E277")}),1.0]])]});
            var Q8;
            Q8=makeQuery(id+"F0.imprint","IMPRINT",FACE,{"disambiguationData":[TD([[makeQuery(id+"F0.imprint","IMPRINT",EDGE,{"derivedFrom":sQuery(id+"F0.wireOp",EDGE,"E1792")}),1.0]])]});
            var Q9;
            Q9 = qSketchRegion(id + "F0", true);
            extrude(context, id + "F1", {"entities" : qUnion([Q0, Q1, Q2, Q3, Q4, Q5, Q6, Q7, Q8, Q9]), "oppositeDirection" : true, "depth" : 1 * mm});
        }
    });
